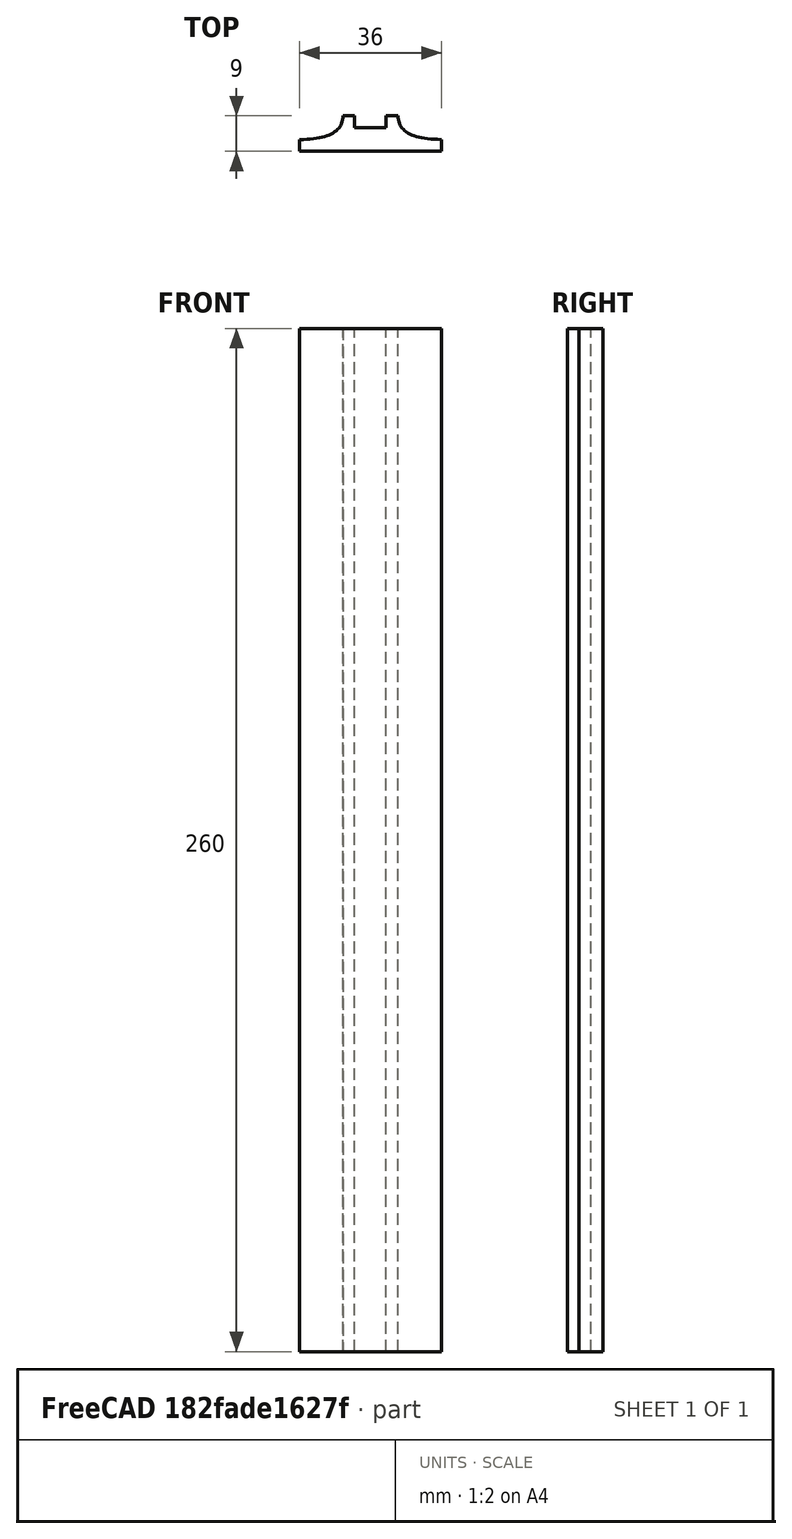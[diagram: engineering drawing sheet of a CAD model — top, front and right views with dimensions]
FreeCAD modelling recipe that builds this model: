
FCSTD DOCUMENT  (FreeCAD 0.19R0.19.2)
Label: laptopStand294.FCStd
License: All rights reserved
LicenseURL: http://en.wikipedia.org/wiki/All_rights_reserved
objects: Sketcher::SketchObject×10, Part::Extrusion×1
note: 11 computed .brp shape members not serialized (recipe doc carries the construction recipe); baked Part::Feature solids carry a one-line shape summary decoded from their .brp

FEATURE [Sketcher::SketchObject] Sketch001  label="legTop"
  FullyConstrained = false
  MapMode = 4
  Placement = pos=(0,0,0) rot=(0.57735,0.57735,0.57735;2.0944rad)
  sketch-geometry (59):
    g0: BSplineCurve PolesCount=3 KnotsCount=2 Degree=2 IsPeriodic=0
    g1: ArcOfCircle CenterX=73.1223 CenterY=-32.291 CenterZ=0 NormalX=0 NormalY=0 NormalZ=1 AngleXU=0 Radius=13 StartAngle=5.92268 EndAngle=9.06428
    g2: ArcOfCircle CenterX=66.7816 CenterY=-49.1439 CenterZ=0 NormalX=0 NormalY=0 NormalZ=1 AngleXU=0 Radius=13 StartAngle=2.78068 EndAngle=5.92131
    g3-g6: Circle x4 (B-spline internal-alignment scaffolding for g7; pole/knot coordinates omitted)
    g7: BSplineCurve PolesCount=4 KnotsCount=2 Degree=3 IsPeriodic=0
    g8: GeomPoint X=28.8094 Y=-19.0875 Z=0
    g9: GeomPoint X=47.0443 Y=-50.4712 Z=0
    g10: Circle CenterX=53.5586 CenterY=-23.2695 CenterZ=0 NormalX=0 NormalY=0 NormalZ=1 AngleXU=0 Radius=3.24518
    g11: LineSegment StartX=117.223 StartY=-19.0875 StartZ=0 EndX=117.223 EndY=-16.0875 EndZ=0
    g12: LineSegment StartX=117.223 StartY=-16.0875 StartZ=0 EndX=17.2232 EndY=-16.0875 EndZ=0
    g13: LineSegment StartX=17.2232 StartY=-16.0875 StartZ=0 EndX=17.2232 EndY=-19.0875 EndZ=0
    g14: LineSegment StartX=28.8094 StartY=-19.0875 StartZ=0 EndX=17.2232 EndY=-19.0875 EndZ=0
    g15: LineSegment StartX=85.2866 StartY=-36.8766 StartZ=0 EndX=78.9396 EndY=-53.7463 EndZ=0
    g16: LineSegment StartX=60.9579 StartY=-27.7053 StartZ=0 EndX=54.6191 EndY=-44.5532 EndZ=0
    g17: BSplineCurve PolesCount=3 KnotsCount=2 Degree=2 IsPeriodic=0
    g18: Circle CenterX=-199.665 CenterY=-138.314 CenterZ=0 NormalX=0 NormalY=0 NormalZ=1 AngleXU=0 Radius=1
    g19: GeomPoint X=-199.665 Y=-138.314 Z=0
    g20: LineSegment StartX=-199.665 StartY=-138.314 StartZ=0 EndX=-200.721 EndY=-141.122 EndZ=0
    g21: Circle CenterX=-17.0256 CenterY=-190.268 CenterZ=0 NormalX=0 NormalY=0 NormalZ=1 AngleXU=0 Radius=10.5072
    g22: Circle CenterX=-37.7758 CenterY=-187.672 CenterZ=0 NormalX=0 NormalY=0 NormalZ=1 AngleXU=0 Radius=5.64388
    g23: Circle CenterX=-51.4606 CenterY=-185.091 CenterZ=0 NormalX=0 NormalY=0 NormalZ=1 AngleXU=0 Radius=3.01653
    g24: Circle CenterX=-60.4835 CenterY=-182.688 CenterZ=0 NormalX=0 NormalY=0 NormalZ=1 AngleXU=0 Radius=2.12826
    g25: Circle CenterX=-3.29005 CenterY=-177.662 CenterZ=0 NormalX=0 NormalY=0 NormalZ=1 AngleXU=0 Radius=3.26661
    g26: ArcOfCircle CenterX=11.0205 CenterY=-198.019 CenterZ=0 NormalX=0 NormalY=0 NormalZ=1 AngleXU=0 Radius=13 StartAngle=2.78068 EndAngle=5.92131
    g27: LineSegment StartX=5.08312 StartY=-176.581 StartZ=0 EndX=-1.14188 EndY=-193.429 EndZ=0
    g28: LineSegment StartX=29.4118 StartY=-185.752 StartZ=0 EndX=23.1786 EndY=-202.622 EndZ=0
    g29: ArcOfCircle CenterX=17.2475 CenterY=-181.166 CenterZ=0 NormalX=0 NormalY=0 NormalZ=1 AngleXU=0 Radius=13 StartAngle=5.92268 EndAngle=9.06428
    g30: LineSegment StartX=38.8952 StartY=-231.233 StartZ=0 EndX=-200.721 EndY=-141.122 EndZ=0
    g31: LineSegment StartX=38.8952 StartY=-231.233 StartZ=0 EndX=39.9512 EndY=-228.425 EndZ=0
    g32: ArcOfCircle CenterX=46.9911 CenterY=-209.705 CenterZ=0 NormalX=0 NormalY=0 NormalZ=1 AngleXU=0 Radius=20 StartAngle=2.78766 EndAngle=4.35269
    g33: LineSegment StartX=23.7323 StartY=-126.969 StartZ=0 EndX=17.4091 EndY=-143.817 EndZ=0
    g34: ArcOfCircle CenterX=29.5716 CenterY=-148.408 CenterZ=0 NormalX=0 NormalY=0 NormalZ=1 AngleXU=0 Radius=13 StartAngle=2.78068 EndAngle=5.92131
    g35: ArcOfCircle CenterX=35.8967 CenterY=-131.555 CenterZ=0 NormalX=0 NormalY=0 NormalZ=1 AngleXU=0 Radius=13 StartAngle=5.92268 EndAngle=9.06428
    g36: ArcOfCircle CenterX=48.1805 CenterY=-98.7782 CenterZ=0 NormalX=0 NormalY=0 NormalZ=1 AngleXU=0 Radius=13 StartAngle=2.78068 EndAngle=5.92131
    g37: LineSegment StartX=42.354 StartY=-77.3391 StartZ=0 EndX=36.018 EndY=-94.1875 EndZ=0
    g38: ArcOfCircle CenterX=54.5183 CenterY=-81.9247 CenterZ=0 NormalX=0 NormalY=0 NormalZ=1 AngleXU=0 Radius=13 StartAngle=5.92268 EndAngle=9.06428
    g39: LineSegment StartX=66.6827 StartY=-86.5104 StartZ=0 EndX=60.3386 EndY=-103.381 EndZ=0
    g40: LineSegment StartX=48.061 StartY=-136.14 StartZ=0 EndX=41.7296 EndY=-153.01 EndZ=0
    g41: LineSegment StartX=28.2308 StartY=-202.773 StartZ=0 EndX=94.6579 EndY=-26.1359 EndZ=0
    g42: LineSegment StartX=47.0443 StartY=-50.4712 StartZ=0 EndX=8.65492 EndY=-152.553 EndZ=0
    g43: LineSegment StartX=23.1786 StartY=-202.622 StartZ=0 EndX=19.0195 EndY=-213.878 EndZ=0
    g44: ArcOfCircle CenterX=20.184 CenterY=-217.506 CenterZ=0 NormalX=0 NormalY=0 NormalZ=1 AngleXU=0 Radius=3.81084 StartAngle=1.88136 EndAngle=6.80465
    g45: LineSegment StartX=28.2308 StartY=-202.773 StartZ=0 EndX=23.4884 EndY=-215.608 EndZ=0
    g46: LineSegment StartX=41.2852 StartY=-117.017 StartZ=0 EndX=40.4092 EndY=-119.359 EndZ=0
    g47: LineSegment StartX=38.4753 StartY=-115.966 StartZ=0 EndX=41.2852 EndY=-117.017 EndZ=0
    g48: ArcOfCircle CenterX=36.3663 CenterY=-113.042 CenterZ=0 NormalX=0 NormalY=0 NormalZ=1 AngleXU=0 Radius=3.60555 StartAngle=0.230024 EndAngle=5.3372
    g49: LineSegment StartX=39.8769 StartY=-112.22 StartZ=0 EndX=42.6867 EndY=-113.271 EndZ=0
    g50: LineSegment StartX=42.6867 StartY=-113.271 StartZ=0 EndX=43.5628 EndY=-110.929 EndZ=0
    g51: LineSegment StartX=22.7134 StartY=-166.661 StartZ=0 EndX=21.8375 EndY=-169.003 EndZ=0
    g52: LineSegment StartX=19.9036 StartY=-165.61 StartZ=0 EndX=22.7134 EndY=-166.661 EndZ=0
    g53: ArcOfCircle CenterX=17.7945 CenterY=-162.686 CenterZ=0 NormalX=0 NormalY=0 NormalZ=1 AngleXU=0 Radius=3.60555 StartAngle=0.230024 EndAngle=5.3372
    g54: LineSegment StartX=21.3051 StartY=-161.864 StartZ=0 EndX=24.1149 EndY=-162.915 EndZ=0
    g55: LineSegment StartX=24.1149 StartY=-162.915 StartZ=0 EndX=24.991 EndY=-160.573 EndZ=0
    g56: LineSegment StartX=41.085 StartY=-66.3176 StartZ=0 EndX=46.0385 EndY=-62.5254 EndZ=0
    g57: LineSegment StartX=48.9563 StartY=-66.3367 StartZ=0 EndX=44.7488 EndY=-73.3482 EndZ=0
    g58: ArcOfCircle CenterX=49.8795 CenterY=-62.6074 CenterZ=0 NormalX=0 NormalY=0 NormalZ=1 AngleXU=0 Radius=3.84187 StartAngle=4.46973 EndAngle=9.40343
  constraints (101):
    c: Block(g0)
    c: Block(g1)
    c: Block(g2)
    c: Weight(g3) = 1
    c: Equal(g3,g4)
    c: Equal(g3,g5)
    c: Equal(g3,g6)
    c: InternalAlignment(g3-g6 -> g7) x4
    c: InternalAlignment(g8,g7)
    c: InternalAlignment(g9,g7)
    c: Block(g10)
    c: Block(g7)
    c: Coincident(g11,g0)
    c: Vertical(g11)
    c: Coincident(g12,g11)
    c: Horizontal(g12)
    c: Coincident(g13,g12)
    c: Vertical(g13)
    c: Block(g12)
    c: Coincident(g14,g7)
    c: Coincident(g14,g13)
    c: Horizontal(g14)
    c: Coincident(g15,g1)
    c: Coincident(g15,g2)
    c: Coincident(g16,g1)
    c: Coincident(g16,g2)
    c: Distance(g12) = 100
    c: Block(g26)
    c: Block(g29)
    c: InternalAlignment(g18,g17)
    c: InternalAlignment(g19,g17)
    c: Block(g17)
    c: Block(g21)
    c: Block(g25)
    c: Block(g22)
    c: Block(g23)
    c: Block(g24)
    c: Block(g32)
    c: Coincident(g31,g30)
    c: Coincident(g31,g32)
    c: Block(g31)
    c: Coincident(g20,g17)
    c: Coincident(g20,g30)
    c: Block(g30)
    c: Coincident(g27,g29)
    c: Coincident(g27,g26)
    c: Coincident(g28,g29)
    c: Coincident(g28,g26)
    c: Block(g34)
    c: Block(g35)
    c: Coincident(g33,g35)
    c: Coincident(g33,g34)
    c: Block(g36)
    c: Block(g38)
    c: Coincident(g37,g38)
    c: Coincident(g37,g36)
    c: Coincident(g39,g38)
    c: Coincident(g39,g36)
    c: Coincident(g40,g35)
    c: Coincident(g40,g34)
    c: Coincident(g41,g32)
    c: Coincident(g41,g0)
    c: Coincident(g42,g7)
    c: Coincident(g42,g17)
    c: Coincident(g43,g26)
    c: Parallel(g28,g43)
    c: Distance(g43) = 12
    c: Block(g28)
    c: Coincident(g44,g43)
    c: Block(g44)
    c: Coincident(g45,g32)
    c: Coincident(g45,g44)
    c: Tangent(g45,g32)
    c: Parallel(g45,g43)
    c: Block(g45)
    c: Block(g48)
    c: Coincident(g49,g48)
    c: Coincident(g47,g48)
    c: Parallel(g49,g47)
    c: Coincident(g46,g47)
    c: Coincident(g50,g49)
    c: Block(g50)
    c: Block(g46)
    c: Block(g47)
    c: Block(g49)
    c: Block(g53)
    c: Coincident(g54,g53)
    c: Coincident(g52,g53)
    c: Parallel(g54,g52)
    c: Coincident(g51,g52)
    c: Coincident(g55,g54)
    c: Block(g55)
    c: Block(g51)
    c: Block(g52)
    c: Block(g54)
    c: PointOnObject(g56,g42)
    c: Block(g56)
    c: PointOnObject(g57,g38)
    c: Coincident(g58,g56)
    c: Coincident(g58,g57)
    c: Block(g58)
FEATURE [Sketcher::SketchObject] Sketch002
  FullyConstrained = true
  sketch-geometry (20):
    g0: LineSegment StartX=-2.77179 StartY=-200.304 StartZ=0 EndX=5.22821 EndY=-200.304 EndZ=0
    g1: LineSegment StartX=5.22821 StartY=-200.304 StartZ=0 EndX=5.22821 EndY=-197.304 EndZ=0
    g2: LineSegment StartX=-2.77179 StartY=-200.304 StartZ=0 EndX=-2.77179 EndY=-197.304 EndZ=0
    g3: LineSegment StartX=5.22821 StartY=-197.304 StartZ=0 EndX=8.22821 EndY=-197.304 EndZ=0
    g4: LineSegment StartX=-2.77179 StartY=-197.304 StartZ=0 EndX=-5.77179 EndY=-197.304 EndZ=0
    g5: LineSegment StartX=19.2282 StartY=-203.304 StartZ=0 EndX=19.2282 EndY=-206.304 EndZ=0
    g6: LineSegment StartX=-16.7718 StartY=-203.304 StartZ=0 EndX=-16.7718 EndY=-206.304 EndZ=0
    g7: LineSegment StartX=-16.7718 StartY=-206.304 StartZ=0 EndX=19.2282 EndY=-206.304 EndZ=0
    g8: Circle CenterX=-16.7718 CenterY=-203.304 CenterZ=0 NormalX=0 NormalY=0 NormalZ=1 AngleXU=0 Radius=1
    g9: Circle CenterX=-5.77179 CenterY=-203.304 CenterZ=0 NormalX=0 NormalY=0 NormalZ=1 AngleXU=0 Radius=1
    g10: Circle CenterX=-5.77179 CenterY=-197.304 CenterZ=0 NormalX=0 NormalY=0 NormalZ=1 AngleXU=0 Radius=1
    g11: BSplineCurve PolesCount=3 KnotsCount=2 Degree=2 IsPeriodic=0
    g12: GeomPoint X=-16.7718 Y=-203.304 Z=0
    g13: GeomPoint X=-5.77179 Y=-197.304 Z=0
    g14: Circle CenterX=19.2282 CenterY=-203.304 CenterZ=0 NormalX=0 NormalY=0 NormalZ=1 AngleXU=0 Radius=1
    g15: Circle CenterX=8.22821 CenterY=-203.304 CenterZ=0 NormalX=0 NormalY=0 NormalZ=1 AngleXU=0 Radius=1
    g16: Circle CenterX=8.22821 CenterY=-197.304 CenterZ=0 NormalX=0 NormalY=0 NormalZ=1 AngleXU=0 Radius=1
    g17: BSplineCurve PolesCount=3 KnotsCount=2 Degree=2 IsPeriodic=0
    g18: GeomPoint X=19.2282 Y=-203.304 Z=0
    g19: GeomPoint X=8.22821 Y=-197.304 Z=0
  constraints (41):
    c: Horizontal(g0)
    c: Distance(g0) = 8
    c: Coincident(g1,g0)
    c: Vertical(g1)
    c: Distance(g1) = 3
    c: Coincident(g2,g0)
    c: Vertical(g2)
    c: Distance(g2) = 3
    c: Coincident(g3,g1)
    c: Horizontal(g3)
    c: Distance(g3) = 3
    c: Coincident(g4,g2)
    c: Horizontal(g4)
    c: Distance(g4) = 3
    c: Vertical(g5)
    c: Vertical(g6)
    c: Coincident(g7,g6)
    c: Coincident(g7,g5)
    c: Weight(g8) = 1
    c: Equal(g8,g9)
    c: Equal(g8,g10)
    c: Coincident(g11,g4)
    c: InternalAlignment(g8,g11)
    c: InternalAlignment(g9,g11)
    c: InternalAlignment(g10,g11)
    c: InternalAlignment(g12,g11)
    c: InternalAlignment(g13,g11)
    c: Coincident(g17,g5)
    c: Weight(g14) = 1
    c: Equal(g14,g15)
    c: Equal(g14,g16)
    c: Coincident(g17,g3)
    c: InternalAlignment(g14,g17)
    c: InternalAlignment(g15,g17)
    c: InternalAlignment(g16,g17)
    c: InternalAlignment(g18,g17)
    c: InternalAlignment(g19,g17)
    c: Block(g7)
    c: Block(g17)
    c: Block(g11)
    c: Block(g6)
FEATURE [Part::Extrusion] Extrude003
  Base = -> Sketch002
  Dir = (0,0,1)
  DirMode = 2
  FaceMakerClass = Part::FaceMakerBullseye
  LengthFwd = 260
  LengthRev = 0
  Solid = true
  Symmetric = false
FEATURE [Sketcher::SketchObject] Sketch003  label="original"
  FullyConstrained = false
  sketch-geometry (469):
    g0: LineSegment StartX=-42.9272 StartY=136.221 StartZ=0 EndX=-42.9272 EndY=-103.779 EndZ=0
    g1: LineSegment StartX=407.073 StartY=136.221 StartZ=0 EndX=407.073 EndY=-103.779 EndZ=0
    g2: ArcOfCircle CenterX=-26.9272 CenterY=-83.7794 CenterZ=0 NormalX=0 NormalY=0 NormalZ=1 AngleXU=0 Radius=8 StartAngle=3.14159 EndAngle=6.28319
    g3: ArcOfCircle CenterX=391.073 CenterY=-83.7794 CenterZ=0 NormalX=0 NormalY=0 NormalZ=1 AngleXU=0 Radius=8 StartAngle=3.14159 EndAngle=6.28319
    g4: Circle CenterX=175.022 CenterY=27.0628 CenterZ=0 NormalX=0 NormalY=0 NormalZ=1 AngleXU=0 Radius=1
    g5: Circle CenterX=179.022 CenterY=24.8665 CenterZ=0 NormalX=0 NormalY=0 NormalZ=1 AngleXU=0 Radius=1
    g6: Circle CenterX=179.022 CenterY=27.0628 CenterZ=0 NormalX=0 NormalY=0 NormalZ=1 AngleXU=0 Radius=1
    g7: BSplineCurve PolesCount=3 KnotsCount=2 Degree=2 IsPeriodic=0
    g8: GeomPoint X=175.022 Y=27.0628 Z=0
    g9: GeomPoint X=179.022 Y=27.0628 Z=0
    g10: Circle CenterX=189.124 CenterY=27.0628 CenterZ=0 NormalX=0 NormalY=0 NormalZ=1 AngleXU=0 Radius=1
    g11: Circle CenterX=185.124 CenterY=24.8665 CenterZ=0 NormalX=0 NormalY=0 NormalZ=1 AngleXU=0 Radius=1
    g12: Circle CenterX=185.124 CenterY=27.0628 CenterZ=0 NormalX=0 NormalY=0 NormalZ=1 AngleXU=0 Radius=1
    g13: BSplineCurve PolesCount=3 KnotsCount=2 Degree=2 IsPeriodic=0
    g14: GeomPoint X=189.124 Y=27.0628 Z=0
    g15: GeomPoint X=185.124 Y=27.0628 Z=0
    g16: Circle CenterX=175.022 CenterY=5.37834 CenterZ=0 NormalX=0 NormalY=0 NormalZ=1 AngleXU=0 Radius=1
    g17: Circle CenterX=179.022 CenterY=7.57463 CenterZ=0 NormalX=0 NormalY=0 NormalZ=1 AngleXU=0 Radius=1
    g18: Circle CenterX=179.022 CenterY=5.34704 CenterZ=0 NormalX=0 NormalY=0 NormalZ=1 AngleXU=0 Radius=1
    g19: BSplineCurve PolesCount=3 KnotsCount=2 Degree=2 IsPeriodic=0
    g20: GeomPoint X=175.022 Y=5.37834 Z=0
    g21: GeomPoint X=179.022 Y=5.34704 Z=0
    g22: Circle CenterX=189.124 CenterY=5.37834 CenterZ=0 NormalX=0 NormalY=0 NormalZ=1 AngleXU=0 Radius=1
    g23: Circle CenterX=185.124 CenterY=7.57463 CenterZ=0 NormalX=0 NormalY=0 NormalZ=1 AngleXU=0 Radius=1
    g24: Circle CenterX=185.124 CenterY=5.34704 CenterZ=0 NormalX=0 NormalY=0 NormalZ=1 AngleXU=0 Radius=1
    g25: BSplineCurve PolesCount=3 KnotsCount=2 Degree=2 IsPeriodic=0
    g26: GeomPoint X=189.124 Y=5.37834 Z=0
    g27: GeomPoint X=185.124 Y=5.34704 Z=0
    g28: Circle CenterX=165.871 CenterY=18.1458 CenterZ=0 NormalX=0 NormalY=0 NormalZ=1 AngleXU=0 Radius=1
    g29: Circle CenterX=169.377 CenterY=16.2206 CenterZ=0 NormalX=0 NormalY=0 NormalZ=1 AngleXU=0 Radius=1
    g30: Circle CenterX=165.871 CenterY=14.2956 CenterZ=0 NormalX=0 NormalY=0 NormalZ=1 AngleXU=0 Radius=1
    g31: BSplineCurve PolesCount=3 KnotsCount=2 Degree=2 IsPeriodic=0
    g32: GeomPoint X=165.871 Y=18.1458 Z=0
    g33: GeomPoint X=165.871 Y=14.2956 Z=0
    g34: Circle CenterX=198.275 CenterY=18.1318 CenterZ=0 NormalX=0 NormalY=0 NormalZ=1 AngleXU=0 Radius=1
    g35: Circle CenterX=194.768 CenterY=16.2206 CenterZ=0 NormalX=0 NormalY=0 NormalZ=1 AngleXU=0 Radius=1
    g36: Circle CenterX=198.264 CenterY=14.2963 CenterZ=0 NormalX=0 NormalY=0 NormalZ=1 AngleXU=0 Radius=1
    g37: BSplineCurve PolesCount=3 KnotsCount=2 Degree=2 IsPeriodic=0
    g38: GeomPoint X=198.275 Y=18.1318 Z=0
    g39: GeomPoint X=198.264 Y=14.2963 Z=0
    g40: LineSegment StartX=407.073 StartY=-103.779 StartZ=0 EndX=-42.9272 EndY=-103.779 EndZ=0
    g41: Circle CenterX=125.607 CenterY=54.1951 CenterZ=0 NormalX=0 NormalY=0 NormalZ=1 AngleXU=0 Radius=1
    g42: Circle CenterX=139.632 CenterY=46.4944 CenterZ=0 NormalX=0 NormalY=0 NormalZ=1 AngleXU=0 Radius=1
    g43: Circle CenterX=127.326 CenterY=56.7187 CenterZ=0 NormalX=0 NormalY=0 NormalZ=1 AngleXU=0 Radius=1
    g44: BSplineCurve PolesCount=3 KnotsCount=2 Degree=2 IsPeriodic=0
    g45: GeomPoint X=125.607 Y=54.1951 Z=0
    g46: GeomPoint X=127.326 Y=56.7187 Z=0
    g47: Circle CenterX=236.824 CenterY=56.7187 CenterZ=0 NormalX=0 NormalY=0 NormalZ=1 AngleXU=0 Radius=1
    g48: Circle CenterX=224.513 CenterY=46.4944 CenterZ=0 NormalX=0 NormalY=0 NormalZ=1 AngleXU=0 Radius=1
    g49: Circle CenterX=238.538 CenterY=54.1951 CenterZ=0 NormalX=0 NormalY=0 NormalZ=1 AngleXU=0 Radius=1
    g50: BSplineCurve PolesCount=3 KnotsCount=2 Degree=2 IsPeriodic=0
    g51: GeomPoint X=236.824 Y=56.7187 Z=0
    g52: GeomPoint X=238.538 Y=54.1951 Z=0
    g53: Circle CenterX=238.538 CenterY=-21.7516 CenterZ=0 NormalX=0 NormalY=0 NormalZ=1 AngleXU=0 Radius=1
    g54: Circle CenterX=224.513 CenterY=-14.0532 CenterZ=0 NormalX=0 NormalY=0 NormalZ=1 AngleXU=0 Radius=1
    g55: Circle CenterX=236.584 CenterY=-24.2775 CenterZ=0 NormalX=0 NormalY=0 NormalZ=1 AngleXU=0 Radius=1
    g56: BSplineCurve PolesCount=3 KnotsCount=2 Degree=2 IsPeriodic=0
    g57: GeomPoint X=238.538 Y=-21.7516 Z=0
    g58: GeomPoint X=236.584 Y=-24.2775 Z=0
    g59: Circle CenterX=125.607 CenterY=-21.7539 CenterZ=0 NormalX=0 NormalY=0 NormalZ=1 AngleXU=0 Radius=1
    g60: Circle CenterX=139.632 CenterY=-14.0532 CenterZ=0 NormalX=0 NormalY=0 NormalZ=1 AngleXU=0 Radius=1
    g61: Circle CenterX=127.325 CenterY=-24.2775 CenterZ=0 NormalX=0 NormalY=0 NormalZ=1 AngleXU=0 Radius=1
    g62: BSplineCurve PolesCount=3 KnotsCount=2 Degree=2 IsPeriodic=0
    g63: GeomPoint X=125.607 Y=-21.7539 Z=0
    g64: GeomPoint X=127.325 Y=-24.2775 Z=0
    g65: Circle CenterX=302.996 CenterY=111.695 CenterZ=0 NormalX=0 NormalY=0 NormalZ=1 AngleXU=0 Radius=1
    g66: Circle CenterX=306.073 CenterY=114.251 CenterZ=0 NormalX=0 NormalY=0 NormalZ=1 AngleXU=0 Radius=1
    g67: Circle CenterX=306.073 CenterY=110.251 CenterZ=0 NormalX=0 NormalY=0 NormalZ=1 AngleXU=0 Radius=1
    g68: BSplineCurve PolesCount=3 KnotsCount=2 Degree=2 IsPeriodic=0
    g69: GeomPoint X=302.996 Y=111.695 Z=0
    g70: GeomPoint X=306.073 Y=110.251 Z=0
    g71: Circle CenterX=306.073 CenterY=95.2763 CenterZ=0 NormalX=0 NormalY=0 NormalZ=1 AngleXU=0 Radius=1
    g72: Circle CenterX=306.073 CenterY=91.2763 CenterZ=0 NormalX=0 NormalY=0 NormalZ=1 AngleXU=0 Radius=1
    g73: Circle CenterX=302.567 CenterY=89.3511 CenterZ=0 NormalX=0 NormalY=0 NormalZ=1 AngleXU=0 Radius=1
    g74: BSplineCurve PolesCount=3 KnotsCount=2 Degree=2 IsPeriodic=0
    g75: GeomPoint X=306.073 Y=95.2763 Z=0
    g76: GeomPoint X=302.567 Y=89.3511 Z=0
    g77: LineSegment StartX=306.073 StartY=110.251 StartZ=0 EndX=306.073 EndY=95.2763 EndZ=0
    g78: LineSegment StartX=302.996 StartY=111.695 StartZ=0 EndX=236.824 EndY=56.7187 EndZ=0
    g79: LineSegment StartX=238.538 StartY=54.1951 StartZ=0 EndX=302.567 EndY=89.3511 EndZ=0
    g80: Circle CenterX=61.1496 CenterY=111.695 CenterZ=0 NormalX=0 NormalY=0 NormalZ=1 AngleXU=0 Radius=1
    g81: Circle CenterX=58.0728 CenterY=114.251 CenterZ=0 NormalX=0 NormalY=0 NormalZ=1 AngleXU=0 Radius=1
    g82: Circle CenterX=58.0728 CenterY=110.251 CenterZ=0 NormalX=0 NormalY=0 NormalZ=1 AngleXU=0 Radius=1
    g83: BSplineCurve PolesCount=3 KnotsCount=2 Degree=2 IsPeriodic=0
    g84: GeomPoint X=61.1496 Y=111.695 Z=0
    g85: GeomPoint X=58.0728 Y=110.251 Z=0
    g86: Circle CenterX=61.5791 CenterY=89.3511 CenterZ=0 NormalX=0 NormalY=0 NormalZ=1 AngleXU=0 Radius=1
    g87: Circle CenterX=58.0728 CenterY=91.2763 CenterZ=0 NormalX=0 NormalY=0 NormalZ=1 AngleXU=0 Radius=1
    g88: Circle CenterX=58.0728 CenterY=95.2763 CenterZ=0 NormalX=0 NormalY=0 NormalZ=1 AngleXU=0 Radius=1
    g89: BSplineCurve PolesCount=3 KnotsCount=2 Degree=2 IsPeriodic=0
    g90: GeomPoint X=61.5791 Y=89.3511 Z=0
    g91: GeomPoint X=58.0728 Y=95.2763 Z=0
    g92: LineSegment StartX=58.0728 StartY=110.251 StartZ=0 EndX=58.0728 EndY=95.2763 EndZ=0
    g93: LineSegment StartX=61.1496 StartY=111.695 StartZ=0 EndX=127.326 EndY=56.7187 EndZ=0
    g94: LineSegment StartX=125.607 StartY=54.1951 StartZ=0 EndX=61.5791 EndY=89.3511 EndZ=0
    g95: Circle CenterX=61.5791 CenterY=-56.9099 CenterZ=0 NormalX=0 NormalY=0 NormalZ=1 AngleXU=0 Radius=1
    g96: Circle CenterX=58.0728 CenterY=-58.8351 CenterZ=0 NormalX=0 NormalY=0 NormalZ=1 AngleXU=0 Radius=1
    g97: Circle CenterX=58.0728 CenterY=-62.8351 CenterZ=0 NormalX=0 NormalY=0 NormalZ=1 AngleXU=0 Radius=1
    g98: BSplineCurve PolesCount=3 KnotsCount=2 Degree=2 IsPeriodic=0
    g99: GeomPoint X=61.5791 Y=-56.9099 Z=0
    g100: GeomPoint X=58.0728 Y=-62.8351 Z=0
    g101: Circle CenterX=58.0728 CenterY=-77.8102 CenterZ=0 NormalX=0 NormalY=0 NormalZ=1 AngleXU=0 Radius=1
    g102: Circle CenterX=58.0728 CenterY=-81.8102 CenterZ=0 NormalX=0 NormalY=0 NormalZ=1 AngleXU=0 Radius=1
    g103: Circle CenterX=61.1496 CenterY=-79.2541 CenterZ=0 NormalX=0 NormalY=0 NormalZ=1 AngleXU=0 Radius=1
    g104: BSplineCurve PolesCount=3 KnotsCount=2 Degree=2 IsPeriodic=0
    g105: GeomPoint X=58.0728 Y=-77.8102 Z=0
    g106: GeomPoint X=61.1496 Y=-79.2541 Z=0
    g107: LineSegment StartX=58.0728 StartY=-62.8351 StartZ=0 EndX=58.0728 EndY=-77.8102 EndZ=0
    g108: LineSegment StartX=61.1496 StartY=-79.2541 StartZ=0 EndX=127.325 EndY=-24.2775 EndZ=0
    g109: LineSegment StartX=125.607 StartY=-21.7539 StartZ=0 EndX=61.5791 EndY=-56.9099 EndZ=0
    g110: Circle CenterX=302.567 CenterY=-56.9099 CenterZ=0 NormalX=0 NormalY=0 NormalZ=1 AngleXU=0 Radius=1
    g111: Circle CenterX=306.073 CenterY=-58.8351 CenterZ=0 NormalX=0 NormalY=0 NormalZ=1 AngleXU=0 Radius=1
    g112: Circle CenterX=306.073 CenterY=-62.8351 CenterZ=0 NormalX=0 NormalY=0 NormalZ=1 AngleXU=0 Radius=1
    g113: BSplineCurve PolesCount=3 KnotsCount=2 Degree=2 IsPeriodic=0
    g114: GeomPoint X=302.567 Y=-56.9099 Z=0
    g115: GeomPoint X=306.073 Y=-62.8351 Z=0
    g116: Circle CenterX=302.996 CenterY=-79.2541 CenterZ=0 NormalX=0 NormalY=0 NormalZ=1 AngleXU=0 Radius=1
    g117: Circle CenterX=306.073 CenterY=-81.8102 CenterZ=0 NormalX=0 NormalY=0 NormalZ=1 AngleXU=0 Radius=1
    g118: Circle CenterX=306.073 CenterY=-77.8102 CenterZ=0 NormalX=0 NormalY=0 NormalZ=1 AngleXU=0 Radius=1
    g119: BSplineCurve PolesCount=3 KnotsCount=2 Degree=2 IsPeriodic=0
    g120: GeomPoint X=302.996 Y=-79.2541 Z=0
    g121: GeomPoint X=306.073 Y=-77.8102 Z=0
    g122: LineSegment StartX=306.073 StartY=-62.8351 StartZ=0 EndX=306.073 EndY=-77.8102 EndZ=0
    g123: LineSegment StartX=302.996 StartY=-79.2541 StartZ=0 EndX=236.584 EndY=-24.2775 EndZ=0
    g124: LineSegment StartX=238.538 StartY=-21.7516 StartZ=0 EndX=302.567 EndY=-56.9099 EndZ=0
    g125: Circle CenterX=61.6457 CenterY=-88.8112 CenterZ=0 NormalX=0 NormalY=0 NormalZ=1 AngleXU=0 Radius=1
    g126: Circle CenterX=58.0728 CenterY=-91.7794 CenterZ=0 NormalX=0 NormalY=0 NormalZ=1 AngleXU=0 Radius=1
    g127: Circle CenterX=63.9135 CenterY=-91.7791 CenterZ=0 NormalX=0 NormalY=0 NormalZ=1 AngleXU=0 Radius=1
    g128: BSplineCurve PolesCount=3 KnotsCount=2 Degree=2 IsPeriodic=0
    g129: GeomPoint X=61.6457 Y=-88.8112 Z=0
    g130: GeomPoint X=63.9135 Y=-91.7791 Z=0
    g131: Circle CenterX=179.022 CenterY=-85.8163 CenterZ=0 NormalX=0 NormalY=0 NormalZ=1 AngleXU=0 Radius=1
    g132: Circle CenterX=179.022 CenterY=-91.7794 CenterZ=0 NormalX=0 NormalY=0 NormalZ=1 AngleXU=0 Radius=1
    g133: Circle CenterX=171.895 CenterY=-91.7791 CenterZ=0 NormalX=0 NormalY=0 NormalZ=1 AngleXU=0 Radius=1
    g134: BSplineCurve PolesCount=3 KnotsCount=2 Degree=2 IsPeriodic=0
    g135: GeomPoint X=179.022 Y=-85.8163 Z=0
    g136: GeomPoint X=171.895 Y=-91.7791 Z=0
    g137: Circle CenterX=185.124 CenterY=-86.2028 CenterZ=0 NormalX=0 NormalY=0 NormalZ=1 AngleXU=0 Radius=1
    g138: Circle CenterX=185.124 CenterY=-91.7794 CenterZ=0 NormalX=0 NormalY=0 NormalZ=1 AngleXU=0 Radius=1
    g139: Circle CenterX=191.747 CenterY=-91.7794 CenterZ=0 NormalX=0 NormalY=0 NormalZ=1 AngleXU=0 Radius=1
    g140: BSplineCurve PolesCount=3 KnotsCount=2 Degree=2 IsPeriodic=0
    g141: GeomPoint X=185.124 Y=-86.2028 Z=0
    g142: GeomPoint X=191.747 Y=-91.7794 Z=0
    g143: Circle CenterX=299.888 CenterY=-86.6413 CenterZ=0 NormalX=0 NormalY=0 NormalZ=1 AngleXU=0 Radius=1
    g144: Circle CenterX=306.073 CenterY=-91.7794 CenterZ=0 NormalX=0 NormalY=0 NormalZ=1 AngleXU=0 Radius=1
    g145: Circle CenterX=298.776 CenterY=-91.7794 CenterZ=0 NormalX=0 NormalY=0 NormalZ=1 AngleXU=0 Radius=1
    g146: BSplineCurve PolesCount=3 KnotsCount=2 Degree=2 IsPeriodic=0
    g147: GeomPoint X=299.888 Y=-86.6413 Z=0
    g148: GeomPoint X=298.776 Y=-91.7794 Z=0
    g149: LineSegment StartX=189.124 StartY=5.37834 StartZ=0 EndX=299.888 EndY=-86.6413 EndZ=0
    g150: LineSegment StartX=298.776 StartY=-91.7794 StartZ=0 EndX=191.747 EndY=-91.7794 EndZ=0
    g151: LineSegment StartX=185.124 StartY=-86.2028 StartZ=0 EndX=185.124 EndY=5.34704 EndZ=0
    g152: LineSegment StartX=179.022 StartY=5.34704 StartZ=0 EndX=179.022 EndY=-85.8163 EndZ=0
    g153: LineSegment StartX=171.895 StartY=-91.7791 StartZ=0 EndX=63.9135 EndY=-91.7791 EndZ=0
    g154: LineSegment StartX=61.6457 StartY=-88.8112 StartZ=0 EndX=175.022 EndY=5.37834 EndZ=0
    g155: Circle CenterX=302.073 CenterY=124.221 CenterZ=0 NormalX=0 NormalY=0 NormalZ=1 AngleXU=0 Radius=1
    g156: Circle CenterX=306.073 CenterY=124.221 CenterZ=0 NormalX=0 NormalY=0 NormalZ=1 AngleXU=0 Radius=1
    g157: Circle CenterX=302.996 CenterY=121.665 CenterZ=0 NormalX=0 NormalY=0 NormalZ=1 AngleXU=0 Radius=1
    g158: BSplineCurve PolesCount=3 KnotsCount=2 Degree=2 IsPeriodic=0
    g159: GeomPoint X=302.073 Y=124.221 Z=0
    g160: GeomPoint X=302.996 Y=121.665 Z=0
    g161: Circle CenterX=189.124 CenterY=124.221 CenterZ=0 NormalX=0 NormalY=0 NormalZ=1 AngleXU=0 Radius=1
    g162: Circle CenterX=185.124 CenterY=124.221 CenterZ=0 NormalX=0 NormalY=0 NormalZ=1 AngleXU=0 Radius=1
    g163: Circle CenterX=185.124 CenterY=120.221 CenterZ=0 NormalX=0 NormalY=0 NormalZ=1 AngleXU=0 Radius=1
    g164: BSplineCurve PolesCount=3 KnotsCount=2 Degree=2 IsPeriodic=0
    g165: GeomPoint X=189.124 Y=124.221 Z=0
    g166: GeomPoint X=185.124 Y=120.221 Z=0
    g167: Circle CenterX=175.022 CenterY=124.221 CenterZ=0 NormalX=0 NormalY=0 NormalZ=1 AngleXU=0 Radius=1
    g168: Circle CenterX=179.022 CenterY=124.221 CenterZ=0 NormalX=0 NormalY=0 NormalZ=1 AngleXU=0 Radius=1
    g169: Circle CenterX=179.022 CenterY=120.221 CenterZ=0 NormalX=0 NormalY=0 NormalZ=1 AngleXU=0 Radius=1
    g170: BSplineCurve PolesCount=3 KnotsCount=2 Degree=2 IsPeriodic=0
    g171: GeomPoint X=175.022 Y=124.221 Z=0
    g172: GeomPoint X=179.022 Y=120.221 Z=0
    g173: Circle CenterX=62.0728 CenterY=124.221 CenterZ=0 NormalX=0 NormalY=0 NormalZ=1 AngleXU=0 Radius=1
    g174: Circle CenterX=58.0728 CenterY=124.221 CenterZ=0 NormalX=0 NormalY=0 NormalZ=1 AngleXU=0 Radius=1
    g175: Circle CenterX=61.1496 CenterY=121.665 CenterZ=0 NormalX=0 NormalY=0 NormalZ=1 AngleXU=0 Radius=1
    g176: BSplineCurve PolesCount=3 KnotsCount=2 Degree=2 IsPeriodic=0
    g177: GeomPoint X=62.0728 Y=124.221 Z=0
    g178: GeomPoint X=61.1496 Y=121.665 Z=0
    g179: LineSegment StartX=179.022 StartY=120.221 StartZ=0 EndX=179.022 EndY=27.0628 EndZ=0
    g180: LineSegment StartX=185.124 StartY=27.0628 StartZ=0 EndX=185.124 EndY=120.221 EndZ=0
    g181: LineSegment StartX=302.996 StartY=121.665 StartZ=0 EndX=189.124 EndY=27.0628 EndZ=0
    g182: LineSegment StartX=175.022 StartY=27.0628 StartZ=0 EndX=61.1496 EndY=121.665 EndZ=0
    g183: Circle CenterX=61.5791 CenterY=75.4095 CenterZ=0 NormalX=0 NormalY=0 NormalZ=1 AngleXU=0 Radius=1
    g184: Circle CenterX=58.0728 CenterY=77.3346 CenterZ=0 NormalX=0 NormalY=0 NormalZ=1 AngleXU=0 Radius=1
    g185: Circle CenterX=58.0728 CenterY=73.3346 CenterZ=0 NormalX=0 NormalY=0 NormalZ=1 AngleXU=0 Radius=1
    g186: BSplineCurve PolesCount=3 KnotsCount=2 Degree=2 IsPeriodic=0
    g187: GeomPoint X=61.5791 Y=75.4095 Z=0
    g188: GeomPoint X=58.0728 Y=73.3346 Z=0
    g189: Circle CenterX=58.0728 CenterY=-40.8935 CenterZ=0 NormalX=0 NormalY=0 NormalZ=1 AngleXU=0 Radius=1
    g190: Circle CenterX=58.0728 CenterY=-44.8935 CenterZ=0 NormalX=0 NormalY=0 NormalZ=1 AngleXU=0 Radius=1
    g191: Circle CenterX=61.5791 CenterY=-42.9683 CenterZ=0 NormalX=0 NormalY=0 NormalZ=1 AngleXU=0 Radius=1
    g192: BSplineCurve PolesCount=3 KnotsCount=2 Degree=2 IsPeriodic=0
    g193: GeomPoint X=58.0728 Y=-40.8935 Z=0
    g194: GeomPoint X=61.5791 Y=-42.9683 Z=0
    g195: LineSegment StartX=61.5791 StartY=-42.9683 StartZ=0 EndX=165.871 EndY=14.2956 EndZ=0
    g196: LineSegment StartX=165.871 StartY=18.1458 StartZ=0 EndX=61.5791 EndY=75.4095 EndZ=0
    g197: LineSegment StartX=58.0728 StartY=73.3346 StartZ=0 EndX=58.0728 EndY=-40.8935 EndZ=0
    g198: Circle CenterX=302.567 CenterY=-42.9683 CenterZ=0 NormalX=0 NormalY=0 NormalZ=1 AngleXU=0 Radius=1
    g199: Circle CenterX=306.073 CenterY=-44.8935 CenterZ=0 NormalX=0 NormalY=0 NormalZ=1 AngleXU=0 Radius=1
    g200: Circle CenterX=306.073 CenterY=-40.8935 CenterZ=0 NormalX=0 NormalY=0 NormalZ=1 AngleXU=0 Radius=1
    g201: BSplineCurve PolesCount=3 KnotsCount=2 Degree=2 IsPeriodic=0
    g202: GeomPoint X=302.567 Y=-42.9683 Z=0
    g203: GeomPoint X=306.073 Y=-40.8935 Z=0
    g204: Circle CenterX=306.073 CenterY=73.3346 CenterZ=0 NormalX=0 NormalY=0 NormalZ=1 AngleXU=0 Radius=1
    g205: Circle CenterX=306.073 CenterY=77.3346 CenterZ=0 NormalX=0 NormalY=0 NormalZ=1 AngleXU=0 Radius=1
    g206: Circle CenterX=302.535 CenterY=75.4095 CenterZ=0 NormalX=0 NormalY=0 NormalZ=1 AngleXU=0 Radius=1
    g207: BSplineCurve PolesCount=3 KnotsCount=2 Degree=2 IsPeriodic=0
    g208: GeomPoint X=306.073 Y=73.3346 Z=0
    g209: GeomPoint X=302.535 Y=75.4095 Z=0
    g210: LineSegment StartX=302.567 StartY=-42.9683 StartZ=0 EndX=198.264 EndY=14.2963 EndZ=0
    g211: LineSegment StartX=198.275 StartY=18.1318 StartZ=0 EndX=302.535 EndY=75.4095 EndZ=0
    g212: LineSegment StartX=306.073 StartY=73.3346 StartZ=0 EndX=306.073 EndY=-40.8935 EndZ=0
    g213: LineSegment StartX=322.073 StartY=105.865 StartZ=0 EndX=328.643 EndY=105.865 EndZ=0
    g214: LineSegment StartX=318.073 StartY=120.221 StartZ=0 EndX=318.073 EndY=109.865 EndZ=0
    g215: LineSegment StartX=336.157 StartY=107.779 StartZ=0 EndX=362.567 EndY=122.294 EndZ=0
    g216: Circle CenterX=362.073 CenterY=124.221 CenterZ=0 NormalX=0 NormalY=0 NormalZ=1 AngleXU=0 Radius=1
    g217: Circle CenterX=366.073 CenterY=124.221 CenterZ=0 NormalX=0 NormalY=0 NormalZ=1 AngleXU=0 Radius=1
    g218: Circle CenterX=362.567 CenterY=122.294 CenterZ=0 NormalX=0 NormalY=0 NormalZ=1 AngleXU=0 Radius=1
    g219: BSplineCurve PolesCount=3 KnotsCount=2 Degree=2 IsPeriodic=0
    g220: GeomPoint X=362.073 Y=124.221 Z=0
    g221: GeomPoint X=362.567 Y=122.294 Z=0
    g222: Circle CenterX=322.073 CenterY=124.221 CenterZ=0 NormalX=0 NormalY=0 NormalZ=1 AngleXU=0 Radius=1
    g223: Circle CenterX=318.073 CenterY=124.221 CenterZ=0 NormalX=0 NormalY=0 NormalZ=1 AngleXU=0 Radius=1
    g224: Circle CenterX=318.073 CenterY=120.221 CenterZ=0 NormalX=0 NormalY=0 NormalZ=1 AngleXU=0 Radius=1
    g225: BSplineCurve PolesCount=3 KnotsCount=2 Degree=2 IsPeriodic=0
    g226: GeomPoint X=322.073 Y=124.221 Z=0
    g227: GeomPoint X=318.073 Y=120.221 Z=0
    g228: Circle CenterX=322.073 CenterY=105.865 CenterZ=0 NormalX=0 NormalY=0 NormalZ=1 AngleXU=0 Radius=1
    g229: Circle CenterX=318.073 CenterY=105.865 CenterZ=0 NormalX=0 NormalY=0 NormalZ=1 AngleXU=0 Radius=1
    g230: Circle CenterX=318.073 CenterY=109.865 CenterZ=0 NormalX=0 NormalY=0 NormalZ=1 AngleXU=0 Radius=1
    g231: BSplineCurve PolesCount=3 KnotsCount=2 Degree=2 IsPeriodic=0
    g232: GeomPoint X=322.073 Y=105.865 Z=0
    g233: GeomPoint X=318.073 Y=109.865 Z=0
    g234: Circle CenterX=336.157 CenterY=107.779 CenterZ=0 NormalX=0 NormalY=0 NormalZ=1 AngleXU=0 Radius=1
    g235: Circle CenterX=332.651 CenterY=105.853 CenterZ=0 NormalX=0 NormalY=0 NormalZ=1 AngleXU=0 Radius=1
    g236: Circle CenterX=328.643 CenterY=105.865 CenterZ=0 NormalX=0 NormalY=0 NormalZ=1 AngleXU=0 Radius=1
    g237: BSplineCurve PolesCount=3 KnotsCount=2 Degree=2 IsPeriodic=0
    g238: GeomPoint X=336.157 Y=107.779 Z=0
    g239: GeomPoint X=328.643 Y=105.865 Z=0
    g240: LineSegment StartX=322.073 StartY=124.221 StartZ=0 EndX=362.073 EndY=124.221 EndZ=0
    g241: Circle CenterX=371.567 CenterY=-80.8644 CenterZ=0 NormalX=0 NormalY=0 NormalZ=1 AngleXU=0 Radius=1
    g242: Circle CenterX=375.073 CenterY=-82.7896 CenterZ=0 NormalX=0 NormalY=0 NormalZ=1 AngleXU=0 Radius=1
    g243: Circle CenterX=375.073 CenterY=-78.7896 CenterZ=0 NormalX=0 NormalY=0 NormalZ=1 AngleXU=0 Radius=1
    g244: BSplineCurve PolesCount=3 KnotsCount=2 Degree=2 IsPeriodic=0
    g245: GeomPoint X=371.567 Y=-80.8644 Z=0
    g246: GeomPoint X=375.073 Y=-78.7896 Z=0
    g247: Circle CenterX=321.579 CenterY=-53.4075 CenterZ=0 NormalX=0 NormalY=0 NormalZ=1 AngleXU=0 Radius=1
    g248: Circle CenterX=318.073 CenterY=-51.4823 CenterZ=0 NormalX=0 NormalY=0 NormalZ=1 AngleXU=0 Radius=1
    g249: Circle CenterX=318.073 CenterY=-47.4805 CenterZ=0 NormalX=0 NormalY=0 NormalZ=1 AngleXU=0 Radius=1
    g250: BSplineCurve PolesCount=3 KnotsCount=2 Degree=2 IsPeriodic=0
    g251: GeomPoint X=321.579 Y=-53.4075 Z=0
    g252: GeomPoint X=318.073 Y=-47.4805 Z=0
    g253: LineSegment StartX=371.567 StartY=-80.8644 StartZ=0 EndX=321.579 EndY=-53.4075 EndZ=0
    g254: Circle CenterX=321.579 CenterY=-67.3492 CenterZ=0 NormalX=0 NormalY=0 NormalZ=1 AngleXU=0 Radius=1
    g255: Circle CenterX=318.073 CenterY=-65.424 CenterZ=0 NormalX=0 NormalY=0 NormalZ=1 AngleXU=0 Radius=1
    g256: Circle CenterX=318.073 CenterY=-69.424 CenterZ=0 NormalX=0 NormalY=0 NormalZ=1 AngleXU=0 Radius=1
    g257: BSplineCurve PolesCount=3 KnotsCount=2 Degree=2 IsPeriodic=0
    g258: GeomPoint X=321.579 Y=-67.3492 Z=0
    g259: GeomPoint X=318.073 Y=-69.424 Z=0
    g260: Circle CenterX=362.567 CenterY=-89.8542 CenterZ=0 NormalX=0 NormalY=0 NormalZ=1 AngleXU=0 Radius=1
    g261: Circle CenterX=366.073 CenterY=-91.7794 CenterZ=0 NormalX=0 NormalY=0 NormalZ=1 AngleXU=0 Radius=1
    g262: Circle CenterX=362.073 CenterY=-91.7794 CenterZ=0 NormalX=0 NormalY=0 NormalZ=1 AngleXU=0 Radius=1
    g263: BSplineCurve PolesCount=3 KnotsCount=2 Degree=2 IsPeriodic=0
    g264: GeomPoint X=362.567 Y=-89.8542 Z=0
    g265: GeomPoint X=362.073 Y=-91.7794 Z=0
    g266: Circle CenterX=322.073 CenterY=-91.7794 CenterZ=0 NormalX=0 NormalY=0 NormalZ=1 AngleXU=0 Radius=1
    g267: Circle CenterX=318.073 CenterY=-91.7794 CenterZ=0 NormalX=0 NormalY=0 NormalZ=1 AngleXU=0 Radius=1
    g268: Circle CenterX=318.073 CenterY=-87.7794 CenterZ=0 NormalX=0 NormalY=0 NormalZ=1 AngleXU=0 Radius=1
    g269: BSplineCurve PolesCount=3 KnotsCount=2 Degree=2 IsPeriodic=0
    g270: GeomPoint X=322.073 Y=-91.7794 Z=0
    g271: GeomPoint X=318.073 Y=-87.7794 Z=0
    g272: LineSegment StartX=362.567 StartY=-89.8542 StartZ=0 EndX=321.579 EndY=-67.3492 EndZ=0
    g273: LineSegment StartX=318.073 StartY=-69.424 StartZ=0 EndX=318.073 EndY=-87.7794 EndZ=0
    g274: LineSegment StartX=322.073 StartY=-91.7794 StartZ=0 EndX=362.073 EndY=-91.7794 EndZ=0
    g275: Circle CenterX=2.07281 CenterY=124.221 CenterZ=0 NormalX=0 NormalY=0 NormalZ=1 AngleXU=0 Radius=1
    g276: Circle CenterX=1.57905 CenterY=122.295 CenterZ=0 NormalX=0 NormalY=0 NormalZ=1 AngleXU=0 Radius=1
    g277: BSplineCurve PolesCount=3 KnotsCount=2 Degree=2 IsPeriodic=0
    g278: GeomPoint X=2.07281 Y=124.221 Z=0
    g279: GeomPoint X=1.57905 Y=122.295 Z=0
    g280: Circle CenterX=42.0728 CenterY=124.221 CenterZ=0 NormalX=0 NormalY=0 NormalZ=1 AngleXU=0 Radius=1
    g281: Circle CenterX=46.0728 CenterY=124.221 CenterZ=0 NormalX=0 NormalY=0 NormalZ=1 AngleXU=0 Radius=1
    g282: Circle CenterX=46.0728 CenterY=120.221 CenterZ=0 NormalX=0 NormalY=0 NormalZ=1 AngleXU=0 Radius=1
    g283: BSplineCurve PolesCount=3 KnotsCount=2 Degree=2 IsPeriodic=0
    g284: GeomPoint X=42.0728 Y=124.221 Z=0
    g285: GeomPoint X=46.0728 Y=120.221 Z=0
    g286: Circle CenterX=46.0728 CenterY=109.865 CenterZ=0 NormalX=0 NormalY=0 NormalZ=1 AngleXU=0 Radius=1
    g287: Circle CenterX=46.0728 CenterY=105.865 CenterZ=0 NormalX=0 NormalY=0 NormalZ=1 AngleXU=0 Radius=1
    g288: Circle CenterX=42.0728 CenterY=105.865 CenterZ=0 NormalX=0 NormalY=0 NormalZ=1 AngleXU=0 Radius=1
    g289: BSplineCurve PolesCount=3 KnotsCount=2 Degree=2 IsPeriodic=0
    g290: GeomPoint X=46.0728 Y=109.865 Z=0
    g291: GeomPoint X=42.0728 Y=105.865 Z=0
    g292: Circle CenterX=35.5028 CenterY=105.865 CenterZ=0 NormalX=0 NormalY=0 NormalZ=1 AngleXU=0 Radius=1
    g293: Circle CenterX=31.5028 CenterY=105.865 CenterZ=0 NormalX=0 NormalY=0 NormalZ=1 AngleXU=0 Radius=1
    g294: Circle CenterX=27.9965 CenterY=107.79 CenterZ=0 NormalX=0 NormalY=0 NormalZ=1 AngleXU=0 Radius=1
    g295: BSplineCurve PolesCount=3 KnotsCount=2 Degree=2 IsPeriodic=0
    g296: GeomPoint X=35.5028 Y=105.865 Z=0
    g297: GeomPoint X=27.9965 Y=107.79 Z=0
    g298: LineSegment StartX=2.07281 StartY=124.221 StartZ=0 EndX=42.0728 EndY=124.221 EndZ=0
    g299: LineSegment StartX=46.0728 StartY=120.221 StartZ=0 EndX=46.0728 EndY=109.865 EndZ=0
    g300: LineSegment StartX=42.0728 StartY=105.865 StartZ=0 EndX=35.5028 EndY=105.865 EndZ=0
    g301: LineSegment StartX=27.9965 StartY=107.79 StartZ=0 EndX=1.57905 EndY=122.295 EndZ=0
    g302: Circle CenterX=42.5666 CenterY=-67.3492 CenterZ=0 NormalX=0 NormalY=0 NormalZ=1 AngleXU=0 Radius=1
    g303: Circle CenterX=46.0728 CenterY=-65.424 CenterZ=0 NormalX=0 NormalY=0 NormalZ=1 AngleXU=0 Radius=1
    g304: Circle CenterX=46.0728 CenterY=-69.424 CenterZ=0 NormalX=0 NormalY=0 NormalZ=1 AngleXU=0 Radius=1
    g305: BSplineCurve PolesCount=3 KnotsCount=2 Degree=2 IsPeriodic=0
    g306: GeomPoint X=42.5666 Y=-67.3492 Z=0
    g307: GeomPoint X=46.0728 Y=-69.424 Z=0
    g308: Circle CenterX=46.0728 CenterY=-87.7794 CenterZ=0 NormalX=0 NormalY=0 NormalZ=1 AngleXU=0 Radius=1
    g309: Circle CenterX=46.0728 CenterY=-91.7794 CenterZ=0 NormalX=0 NormalY=0 NormalZ=1 AngleXU=0 Radius=1
    g310: Circle CenterX=42.0728 CenterY=-91.7794 CenterZ=0 NormalX=0 NormalY=0 NormalZ=1 AngleXU=0 Radius=1
    g311: BSplineCurve PolesCount=3 KnotsCount=2 Degree=2 IsPeriodic=0
    g312: GeomPoint X=46.0728 Y=-87.7794 Z=0
    g313: GeomPoint X=42.0728 Y=-91.7794 Z=0
    g314: Circle CenterX=2.07281 CenterY=-91.7794 CenterZ=0 NormalX=0 NormalY=0 NormalZ=1 AngleXU=0 Radius=1
    g315: Circle CenterX=-1.92719 CenterY=-91.7794 CenterZ=0 NormalX=0 NormalY=0 NormalZ=1 AngleXU=0 Radius=1
    g316: Circle CenterX=1.57905 CenterY=-89.8542 CenterZ=0 NormalX=0 NormalY=0 NormalZ=1 AngleXU=0 Radius=1
    g317: BSplineCurve PolesCount=3 KnotsCount=2 Degree=2 IsPeriodic=0
    g318: GeomPoint X=2.07281 Y=-91.7794 Z=0
    g319: GeomPoint X=1.57905 Y=-89.8542 Z=0
    g320: LineSegment StartX=2.07281 StartY=-91.7794 StartZ=0 EndX=42.0728 EndY=-91.7794 EndZ=0
    g321: LineSegment StartX=46.0728 StartY=-87.7794 StartZ=0 EndX=46.0728 EndY=-69.424 EndZ=0
    g322: LineSegment StartX=42.5666 StartY=-67.3492 StartZ=0 EndX=1.57905 EndY=-89.8542 EndZ=0
    g323: Circle CenterX=322.073 CenterY=76.4095 CenterZ=0 NormalX=0 NormalY=0 NormalZ=1 AngleXU=0 Radius=4
    g324: BSplineCurve PolesCount=3 KnotsCount=2 Degree=2 IsPeriodic=0
    g325: GeomPoint X=318.073 Y=72.4095 Z=0
    g326: GeomPoint X=322.073 Y=76.4095 Z=0
    g327: Circle CenterX=375.073 CenterY=72.4095 CenterZ=0 NormalX=0 NormalY=0 NormalZ=1 AngleXU=0 Radius=1
    g328: Circle CenterX=375.073 CenterY=76.4095 CenterZ=0 NormalX=0 NormalY=0 NormalZ=1 AngleXU=0 Radius=1
    g329: Circle CenterX=371.073 CenterY=76.4095 CenterZ=0 NormalX=0 NormalY=0 NormalZ=1 AngleXU=0 Radius=1
    g330: BSplineCurve PolesCount=3 KnotsCount=2 Degree=2 IsPeriodic=0
    g331: GeomPoint X=375.073 Y=72.4095 Z=0
    g332: GeomPoint X=371.073 Y=76.4095 Z=0
    g333: LineSegment StartX=322.073 StartY=76.4095 StartZ=0 EndX=371.073 EndY=76.4095 EndZ=0
    g334: LineSegment StartX=318.073 StartY=72.4095 StartZ=0 EndX=318.073 EndY=-47.4805 EndZ=0
    g335: LineSegment StartX=375.073 StartY=72.4095 StartZ=0 EndX=375.073 EndY=-78.7896 EndZ=0
    g336: ArcOfCircle CenterX=-26.9272 CenterY=22.1087 CenterZ=0 NormalX=0 NormalY=0 NormalZ=1 AngleXU=0 Radius=4 StartAngle=5e-16 EndAngle=3.14159
    g337: LineSegment StartX=-22.9272 StartY=22.1087 StartZ=0 EndX=-18.9272 EndY=-83.7794 EndZ=0
    g338: LineSegment StartX=-34.9272 StartY=-83.7794 StartZ=0 EndX=-30.9272 EndY=22.1087 EndZ=0
    g339: ArcOfCircle CenterX=391.073 CenterY=22.1087 CenterZ=0 NormalX=0 NormalY=0 NormalZ=1 AngleXU=0 Radius=4 StartAngle=0 EndAngle=3.14159
    g340: LineSegment StartX=387.073 StartY=22.1087 StartZ=0 EndX=383.073 EndY=-83.7794 EndZ=0
    g341: LineSegment StartX=395.073 StartY=22.1087 StartZ=0 EndX=399.073 EndY=-83.7794 EndZ=0
    g342: Circle CenterX=-10.9272 CenterY=-78.7794 CenterZ=0 NormalX=0 NormalY=0 NormalZ=1 AngleXU=0 Radius=1
    g343: Circle CenterX=-10.9272 CenterY=-82.7794 CenterZ=0 NormalX=0 NormalY=0 NormalZ=1 AngleXU=0 Radius=1
    g344: Circle CenterX=-7.42095 CenterY=-80.8542 CenterZ=0 NormalX=0 NormalY=0 NormalZ=1 AngleXU=0 Radius=1
    g345: BSplineCurve PolesCount=3 KnotsCount=2 Degree=2 IsPeriodic=0
    g346: GeomPoint X=-10.9272 Y=-78.7794 Z=0
    g347: GeomPoint X=-7.42095 Y=-80.8542 Z=0
    g348: Circle CenterX=42.5666 CenterY=-53.4075 CenterZ=0 NormalX=0 NormalY=0 NormalZ=1 AngleXU=0 Radius=1
    g349: Circle CenterX=46.0728 CenterY=-51.4823 CenterZ=0 NormalX=0 NormalY=0 NormalZ=1 AngleXU=0 Radius=1
    g350: Circle CenterX=46.0728 CenterY=-47.4823 CenterZ=0 NormalX=0 NormalY=0 NormalZ=1 AngleXU=0 Radius=1
    g351: BSplineCurve PolesCount=3 KnotsCount=2 Degree=2 IsPeriodic=0
    g352: GeomPoint X=42.5666 Y=-53.4075 Z=0
    g353: GeomPoint X=46.0728 Y=-47.4823 Z=0
    g354: Circle CenterX=46.0728 CenterY=72.4095 CenterZ=0 NormalX=0 NormalY=0 NormalZ=1 AngleXU=0 Radius=1
    g355: Circle CenterX=46.0728 CenterY=76.4095 CenterZ=0 NormalX=0 NormalY=0 NormalZ=1 AngleXU=0 Radius=1
    g356: Circle CenterX=42.0728 CenterY=76.4095 CenterZ=0 NormalX=0 NormalY=0 NormalZ=1 AngleXU=0 Radius=1
    g357: BSplineCurve PolesCount=3 KnotsCount=2 Degree=2 IsPeriodic=0
    g358: GeomPoint X=46.0728 Y=72.4095 Z=0
    g359: GeomPoint X=42.0728 Y=76.4095 Z=0
    g360: Circle CenterX=-6.92719 CenterY=76.4095 CenterZ=0 NormalX=0 NormalY=0 NormalZ=1 AngleXU=0 Radius=1
    g361: Circle CenterX=-10.9272 CenterY=76.4095 CenterZ=0 NormalX=0 NormalY=0 NormalZ=1 AngleXU=0 Radius=1
    g362: Circle CenterX=-10.9272 CenterY=72.4095 CenterZ=0 NormalX=0 NormalY=0 NormalZ=1 AngleXU=0 Radius=1
    g363: BSplineCurve PolesCount=3 KnotsCount=2 Degree=2 IsPeriodic=0
    g364: GeomPoint X=-6.92719 Y=76.4095 Z=0
    g365: GeomPoint X=-10.9272 Y=72.4095 Z=0
    g366: LineSegment StartX=-10.9272 StartY=72.4095 StartZ=0 EndX=-10.9272 EndY=-78.7794 EndZ=0
    g367: LineSegment StartX=-7.42095 StartY=-80.8542 StartZ=0 EndX=42.5666 EndY=-53.4075 EndZ=0
    g368: LineSegment StartX=46.0728 StartY=-47.4823 StartZ=0 EndX=46.0728 EndY=72.4095 EndZ=0
    g369: LineSegment StartX=42.0728 StartY=76.4095 StartZ=0 EndX=-6.92719 EndY=76.4095 EndZ=0
    g370: LineSegment StartX=-42.9272 StartY=136.221 StartZ=0 EndX=407.073 EndY=136.221 EndZ=0
    g371: LineSegment StartX=232.072 StartY=136.221 StartZ=0 EndX=220.072 EndY=136.221 EndZ=0
    g372: LineSegment StartX=232.072 StartY=136.221 StartZ=0 EndX=232.072 EndY=124.221 EndZ=0
    g373: LineSegment StartX=220.072 StartY=136.221 StartZ=0 EndX=220.072 EndY=124.221 EndZ=0
    g374: LineSegment StartX=220.072 StartY=136.221 StartZ=0 EndX=226.072 EndY=136.221 EndZ=0
    g375: LineSegment StartX=220.072 StartY=136.221 StartZ=0 EndX=220.072 EndY=130.221 EndZ=0
    g376: LineSegment StartX=220.072 StartY=124.221 StartZ=0 EndX=226.072 EndY=124.221 EndZ=0
    g377: LineSegment StartX=232.072 StartY=124.221 StartZ=0 EndX=232.072 EndY=127.221 EndZ=0
    g378: LineSegment StartX=232.072 StartY=136.221 StartZ=0 EndX=232.072 EndY=133.221 EndZ=0
    g379-g383: Circle x5 (B-spline internal-alignment scaffolding for g384; pole/knot coordinates omitted)
    g384: BSplineCurve PolesCount=5 KnotsCount=3 Degree=3 IsPeriodic=0
    g385: GeomPoint X=232.072 Y=133.221 Z=0
    g386: GeomPoint X=223.072 Y=130.221 Z=0
    g387: GeomPoint X=232.072 Y=127.221 Z=0
    g388: LineSegment StartX=189.124 StartY=124.221 StartZ=0 EndX=302.073 EndY=124.221 EndZ=0
    g389: LineSegment StartX=132.072 StartY=136.221 StartZ=0 EndX=132.072 EndY=124.221 EndZ=0
    g390: LineSegment StartX=132.072 StartY=136.221 StartZ=0 EndX=144.072 EndY=136.221 EndZ=0
    g391: LineSegment StartX=144.072 StartY=136.221 StartZ=0 EndX=144.072 EndY=124.221 EndZ=0
    g392: LineSegment StartX=144.072 StartY=136.221 StartZ=0 EndX=138.072 EndY=136.221 EndZ=0
    g393: LineSegment StartX=144.072 StartY=136.221 StartZ=0 EndX=144.072 EndY=130.221 EndZ=0
    g394: LineSegment StartX=132.072 StartY=136.221 StartZ=0 EndX=132.072 EndY=133.221 EndZ=0
    g395: LineSegment StartX=132.072 StartY=133.221 StartZ=0 EndX=132.072 EndY=127.221 EndZ=0
    g396-g400: Circle x5 (B-spline internal-alignment scaffolding for g401; pole/knot coordinates omitted)
    g401: BSplineCurve PolesCount=5 KnotsCount=3 Degree=3 IsPeriodic=0
    g402: GeomPoint X=132.072 Y=133.221 Z=0
    g403: GeomPoint X=141.072 Y=130.221 Z=0
    g404: GeomPoint X=132.072 Y=127.221 Z=0
    g405: LineSegment StartX=132.072 StartY=124.221 StartZ=0 EndX=175.022 EndY=124.221 EndZ=0
    g406: LineSegment StartX=62.0728 StartY=124.221 StartZ=0 EndX=132.072 EndY=124.221 EndZ=0
    g407: LineSegment StartX=132.072 StartY=136.221 StartZ=0 EndX=131.457 EndY=138.832 EndZ=0
    ... +61 more geometry lines
  constraints (808):
    c: Vertical(g0)
    c: Vertical(g1)
    c: Block(g1)
    c: Block(g0)
    c: Weight(g4) = 1
    c: Equal(g4,g5)
    c: Equal(g4,g6)
    c: InternalAlignment(g4,g7)
    c: InternalAlignment(g5,g7)
    c: InternalAlignment(g6,g7)
    c: InternalAlignment(g8,g7)
    c: InternalAlignment(g9,g7)
    c: Weight(g10) = 1
    c: Equal(g10,g11)
    c: Equal(g10,g12)
    c: InternalAlignment(g10,g13)
    c: InternalAlignment(g11,g13)
    c: InternalAlignment(g12,g13)
    c: InternalAlignment(g14,g13)
    c: InternalAlignment(g15,g13)
    c: Block(g13)
    c: Block(g7)
    c: Weight(g16) = 1
    c: Equal(g16,g17)
    c: Equal(g16,g18)
    c: InternalAlignment(g16,g19)
    c: InternalAlignment(g17,g19)
    c: InternalAlignment(g18,g19)
    c: InternalAlignment(g20,g19)
    c: InternalAlignment(g21,g19)
    c: Weight(g22) = 1
    c: Equal(g22,g23)
    c: Equal(g22,g24)
    c: InternalAlignment(g22,g25)
    c: InternalAlignment(g23,g25)
    c: InternalAlignment(g24,g25)
    c: InternalAlignment(g26,g25)
    c: InternalAlignment(g27,g25)
    c: Block(g25)
    c: Block(g19)
    c: Weight(g28) = 1
    c: Equal(g28,g29)
    c: Equal(g28,g30)
    c: InternalAlignment(g28,g31)
    c: InternalAlignment(g29,g31)
    c: InternalAlignment(g30,g31)
    c: InternalAlignment(g32,g31)
    c: InternalAlignment(g33,g31)
    c: Weight(g34) = 1
    c: Equal(g34,g35)
    c: Equal(g34,g36)
    c: InternalAlignment(g34,g37)
    c: InternalAlignment(g35,g37)
    c: InternalAlignment(g36,g37)
    c: InternalAlignment(g38,g37)
    c: InternalAlignment(g39,g37)
    c: Block(g31)
    c: Block(g37)
    c: Coincident(g40,g1)
    c: Coincident(g40,g0)
    c: Horizontal(g40)
    c: Distance(g40) = 450
    c: Weight(g41) = 1
    c: Equal(g41,g42)
    c: Equal(g41,g43)
    c: InternalAlignment(g41,g44)
    c: InternalAlignment(g42,g44)
    c: InternalAlignment(g43,g44)
    c: InternalAlignment(g45,g44)
    c: InternalAlignment(g46,g44)
    c: Block(g44)
    c: Weight(g47) = 1
    c: Equal(g47,g48)
    c: Equal(g47,g49)
    c: InternalAlignment(g47,g50)
    c: InternalAlignment(g48,g50)
    c: InternalAlignment(g49,g50)
    c: InternalAlignment(g51,g50)
    c: InternalAlignment(g52,g50)
    c: Block(g50)
    c: Weight(g53) = 1
    c: Equal(g53,g54)
    c: Equal(g53,g55)
    c: InternalAlignment(g53,g56)
    c: InternalAlignment(g54,g56)
    c: InternalAlignment(g55,g56)
    c: InternalAlignment(g57,g56)
    c: InternalAlignment(g58,g56)
    c: Block(g56)
    c: Weight(g59) = 1
    c: Equal(g59,g60)
    c: Equal(g59,g61)
    c: InternalAlignment(g59,g62)
    c: InternalAlignment(g60,g62)
    c: InternalAlignment(g61,g62)
    c: InternalAlignment(g63,g62)
    c: InternalAlignment(g64,g62)
    c: Block(g62)
    c: Weight(g65) = 1
    c: Equal(g65,g66)
    c: Equal(g65,g67)
    c: InternalAlignment(g65,g68)
    c: InternalAlignment(g66,g68)
    c: InternalAlignment(g67,g68)
    c: InternalAlignment(g69,g68)
    c: InternalAlignment(g70,g68)
    c: Weight(g71) = 1
    c: Equal(g71,g72)
    c: Equal(g71,g73)
    c: InternalAlignment(g71,g74)
    c: InternalAlignment(g72,g74)
    c: InternalAlignment(g73,g74)
    c: InternalAlignment(g75,g74)
    c: InternalAlignment(g76,g74)
    c: Block(g68)
    c: Block(g74)
    c: Coincident(g77,g68)
    c: Coincident(g77,g74)
    c: Vertical(g77)
    c: Coincident(g78,g68)
    c: Coincident(g78,g50)
    c: Coincident(g79,g50)
    c: Coincident(g79,g74)
    c: Weight(g80) = 1
    c: Equal(g80,g81)
    c: Equal(g80,g82)
    c: InternalAlignment(g80,g83)
    c: InternalAlignment(g81,g83)
    c: InternalAlignment(g82,g83)
    c: InternalAlignment(g84,g83)
    c: InternalAlignment(g85,g83)
    c: Weight(g86) = 1
    c: Equal(g86,g87)
    c: Equal(g86,g88)
    c: InternalAlignment(g86,g89)
    c: InternalAlignment(g87,g89)
    c: InternalAlignment(g88,g89)
    c: InternalAlignment(g90,g89)
    c: InternalAlignment(g91,g89)
    c: Block(g83)
    c: Block(g89)
    c: Coincident(g92,g83)
    c: Coincident(g92,g89)
    c: Vertical(g92)
    c: Coincident(g93,g83)
    c: Coincident(g93,g44)
    c: Coincident(g94,g44)
    c: Coincident(g94,g89)
    c: Weight(g95) = 1
    c: Equal(g95,g96)
    c: Equal(g95,g97)
    c: InternalAlignment(g95,g98)
    c: InternalAlignment(g96,g98)
    c: InternalAlignment(g97,g98)
    c: InternalAlignment(g99,g98)
    c: InternalAlignment(g100,g98)
    c: Weight(g101) = 1
    c: Equal(g101,g102)
    c: Equal(g101,g103)
    c: InternalAlignment(g101,g104)
    c: InternalAlignment(g102,g104)
    c: InternalAlignment(g103,g104)
    c: InternalAlignment(g105,g104)
    c: InternalAlignment(g106,g104)
    c: Block(g98)
    c: Block(g104)
    c: Coincident(g107,g98)
    c: Coincident(g107,g104)
    c: Vertical(g107)
    c: Coincident(g108,g104)
    c: Coincident(g108,g62)
    c: Coincident(g109,g62)
    c: Coincident(g109,g98)
    c: Weight(g110) = 1
    c: Equal(g110,g111)
    c: Equal(g110,g112)
    c: InternalAlignment(g110,g113)
    c: InternalAlignment(g111,g113)
    c: InternalAlignment(g112,g113)
    c: InternalAlignment(g114,g113)
    c: InternalAlignment(g115,g113)
    c: Weight(g116) = 1
    c: Equal(g116,g117)
    c: Equal(g116,g118)
    c: InternalAlignment(g116,g119)
    c: InternalAlignment(g117,g119)
    c: InternalAlignment(g118,g119)
    c: InternalAlignment(g120,g119)
    c: InternalAlignment(g121,g119)
    c: Block(g113)
    c: Block(g119)
    c: Coincident(g122,g113)
    c: Coincident(g122,g119)
    c: Vertical(g122)
    c: Coincident(g123,g119)
    c: Coincident(g123,g56)
    c: Coincident(g124,g56)
    c: Coincident(g124,g113)
    c: Weight(g125) = 1
    c: Equal(g125,g126)
    c: Equal(g125,g127)
    c: InternalAlignment(g125,g128)
    c: InternalAlignment(g126,g128)
    c: InternalAlignment(g127,g128)
    c: InternalAlignment(g129,g128)
    c: InternalAlignment(g130,g128)
    c: Weight(g131) = 1
    c: Equal(g131,g132)
    c: Equal(g131,g133)
    c: InternalAlignment(g131,g134)
    c: InternalAlignment(g132,g134)
    c: InternalAlignment(g133,g134)
    c: InternalAlignment(g135,g134)
    c: InternalAlignment(g136,g134)
    c: Weight(g137) = 1
    c: Equal(g137,g138)
    c: Equal(g137,g139)
    c: InternalAlignment(g137,g140)
    c: InternalAlignment(g138,g140)
    c: InternalAlignment(g139,g140)
    c: InternalAlignment(g141,g140)
    c: InternalAlignment(g142,g140)
    c: Weight(g143) = 1
    c: Equal(g143,g144)
    c: Equal(g143,g145)
    c: InternalAlignment(g143,g146)
    c: InternalAlignment(g144,g146)
    c: InternalAlignment(g145,g146)
    c: InternalAlignment(g147,g146)
    c: InternalAlignment(g148,g146)
    c: Block(g146)
    c: Block(g140)
    c: Block(g134)
    c: Block(g128)
    c: Coincident(g149,g25)
    c: Coincident(g149,g146)
    c: Coincident(g150,g146)
    c: Coincident(g150,g140)
    c: Horizontal(g150)
    c: Coincident(g151,g140)
    c: Coincident(g151,g25)
    c: Vertical(g151)
    c: Coincident(g152,g19)
    c: Coincident(g152,g134)
    c: Vertical(g152)
    c: Coincident(g153,g134)
    c: Coincident(g153,g128)
    c: Horizontal(g153)
    c: Coincident(g154,g128)
    c: Coincident(g154,g19)
    c: Weight(g155) = 1
    c: Equal(g155,g156)
    c: Equal(g155,g157)
    c: InternalAlignment(g155,g158)
    c: InternalAlignment(g156,g158)
    c: InternalAlignment(g157,g158)
    c: InternalAlignment(g159,g158)
    c: InternalAlignment(g160,g158)
    c: Weight(g161) = 1
    c: Equal(g161,g162)
    c: Equal(g161,g163)
    c: InternalAlignment(g161,g164)
    c: InternalAlignment(g162,g164)
    c: InternalAlignment(g163,g164)
    c: InternalAlignment(g165,g164)
    c: InternalAlignment(g166,g164)
    c: Weight(g167) = 1
    c: Equal(g167,g168)
    c: Equal(g167,g169)
    c: InternalAlignment(g167,g170)
    c: InternalAlignment(g168,g170)
    c: InternalAlignment(g169,g170)
    c: InternalAlignment(g171,g170)
    c: InternalAlignment(g172,g170)
    c: Weight(g173) = 1
    c: Equal(g173,g174)
    c: Equal(g173,g175)
    c: InternalAlignment(g173,g176)
    c: InternalAlignment(g174,g176)
    c: InternalAlignment(g175,g176)
    c: InternalAlignment(g177,g176)
    c: InternalAlignment(g178,g176)
    c: Block(g176)
    c: Block(g170)
    c: Block(g164)
    c: Block(g158)
    c: Coincident(g179,g170)
    c: Coincident(g179,g7)
    c: Vertical(g179)
    c: Coincident(g180,g13)
    c: Coincident(g180,g164)
    c: Vertical(g180)
    c: Coincident(g181,g158)
    c: Coincident(g181,g13)
    c: Coincident(g182,g7)
    c: Weight(g183) = 1
    c: Equal(g183,g184)
    c: Equal(g183,g185)
    c: InternalAlignment(g183,g186)
    c: InternalAlignment(g184,g186)
    c: InternalAlignment(g185,g186)
    c: InternalAlignment(g187,g186)
    c: InternalAlignment(g188,g186)
    c: Weight(g189) = 1
    c: Equal(g189,g190)
    c: Equal(g189,g191)
    c: InternalAlignment(g189,g192)
    c: InternalAlignment(g190,g192)
    c: InternalAlignment(g191,g192)
    c: InternalAlignment(g193,g192)
    c: InternalAlignment(g194,g192)
    c: Block(g192)
    c: Block(g186)
    c: Coincident(g195,g192)
    c: Coincident(g195,g31)
    c: Coincident(g196,g31)
    c: Coincident(g196,g186)
    c: Coincident(g197,g186)
    c: Coincident(g197,g192)
    c: Vertical(g197)
    c: Weight(g198) = 1
    c: Equal(g198,g199)
    c: Equal(g198,g200)
    c: InternalAlignment(g198,g201)
    c: InternalAlignment(g199,g201)
    c: InternalAlignment(g200,g201)
    c: InternalAlignment(g202,g201)
    c: InternalAlignment(g203,g201)
    c: Weight(g204) = 1
    c: Equal(g204,g205)
    c: Equal(g204,g206)
    c: InternalAlignment(g204,g207)
    c: InternalAlignment(g205,g207)
    c: InternalAlignment(g206,g207)
    c: InternalAlignment(g208,g207)
    c: InternalAlignment(g209,g207)
    c: Block(g207)
    c: Block(g201)
    c: Coincident(g210,g201)
    c: Coincident(g210,g37)
    c: Coincident(g211,g37)
    c: Coincident(g211,g207)
    c: Coincident(g212,g207)
    c: Coincident(g212,g201)
    c: Vertical(g212)
    c: Horizontal(g213)
    c: Block(g213)
    c: Vertical(g214)
    c: Block(g214)
    c: Block(g215)
    c: Weight(g216) = 1
    c: Equal(g216,g217)
    c: Equal(g216,g218)
    c: InternalAlignment(g216,g219)
    c: InternalAlignment(g217,g219)
    c: InternalAlignment(g218,g219)
    c: InternalAlignment(g220,g219)
    c: InternalAlignment(g221,g219)
    c: Weight(g222) = 1
    c: Equal(g222,g223)
    c: Equal(g222,g224)
    c: InternalAlignment(g222,g225)
    c: InternalAlignment(g223,g225)
    c: InternalAlignment(g224,g225)
    c: InternalAlignment(g226,g225)
    c: InternalAlignment(g227,g225)
    c: Weight(g228) = 1
    c: Equal(g228,g229)
    c: Equal(g228,g230)
    c: InternalAlignment(g228,g231)
    c: InternalAlignment(g229,g231)
    c: InternalAlignment(g230,g231)
    c: InternalAlignment(g232,g231)
    c: InternalAlignment(g233,g231)
    c: Weight(g234) = 1
    c: Equal(g234,g235)
    c: Equal(g234,g236)
    c: InternalAlignment(g234,g237)
    c: InternalAlignment(g235,g237)
    c: InternalAlignment(g236,g237)
    c: InternalAlignment(g238,g237)
    c: InternalAlignment(g239,g237)
    c: Block(g219)
    c: Block(g225)
    c: Block(g231)
    c: Block(g237)
    c: Coincident(g240,g225)
    c: Coincident(g240,g219)
    c: Horizontal(g240)
    c: Block(g182)
    c: Weight(g241) = 1
    c: Equal(g241,g242)
    c: Equal(g241,g243)
    c: InternalAlignment(g241,g244)
    c: InternalAlignment(g242,g244)
    c: InternalAlignment(g243,g244)
    c: InternalAlignment(g245,g244)
    c: InternalAlignment(g246,g244)
    c: Weight(g247) = 1
    c: Equal(g247,g248)
    c: Equal(g247,g249)
    c: InternalAlignment(g247,g250)
    c: InternalAlignment(g248,g250)
    c: InternalAlignment(g249,g250)
    c: InternalAlignment(g251,g250)
    c: InternalAlignment(g252,g250)
    c: Block(g244)
    c: Block(g250)
    c: Coincident(g253,g244)
    c: Coincident(g253,g250)
    c: Weight(g254) = 1
    c: Equal(g254,g255)
    c: Equal(g254,g256)
    c: InternalAlignment(g254,g257)
    c: InternalAlignment(g255,g257)
    c: InternalAlignment(g256,g257)
    c: InternalAlignment(g258,g257)
    c: InternalAlignment(g259,g257)
    c: Weight(g260) = 1
    c: Equal(g260,g261)
    c: Equal(g260,g262)
    c: InternalAlignment(g260,g263)
    c: InternalAlignment(g261,g263)
    c: InternalAlignment(g262,g263)
    c: InternalAlignment(g264,g263)
    c: InternalAlignment(g265,g263)
    c: Weight(g266) = 1
    c: Equal(g266,g267)
    c: Equal(g266,g268)
    c: InternalAlignment(g266,g269)
    c: InternalAlignment(g267,g269)
    c: InternalAlignment(g268,g269)
    c: InternalAlignment(g270,g269)
    c: InternalAlignment(g271,g269)
    c: Block(g269)
    c: Block(g263)
    c: Block(g257)
    c: Coincident(g272,g263)
    c: Coincident(g272,g257)
    c: Coincident(g273,g257)
    c: Coincident(g273,g269)
    c: Vertical(g273)
    c: Coincident(g274,g269)
    c: Coincident(g274,g263)
    c: Horizontal(g274)
    c: Weight(g275) = 1
    c: Equal(g275,g276)
    c: InternalAlignment(g275,g277)
    c: InternalAlignment(g276,g277)
    c: InternalAlignment(g278,g277)
    c: InternalAlignment(g279,g277)
    c: Weight(g280) = 1
    c: InternalAlignment(g281,g283)
    c: InternalAlignment(g282,g283)
    c: InternalAlignment(g284,g283)
    c: InternalAlignment(g285,g283)
    c: Weight(g286) = 1
    c: Equal(g286,g287)
    c: Equal(g286,g288)
    c: InternalAlignment(g286,g289)
    c: InternalAlignment(g287,g289)
    c: InternalAlignment(g288,g289)
    c: InternalAlignment(g290,g289)
    c: InternalAlignment(g291,g289)
    c: Equal(g292,g293)
    c: Equal(g292,g294)
    c: InternalAlignment(g292,g295)
    c: InternalAlignment(g293,g295)
    c: InternalAlignment(g294,g295)
    c: InternalAlignment(g296,g295)
    c: InternalAlignment(g297,g295)
    c: Block(g283)
    c: Block(g289)
    c: Block(g295)
    c: Block(g277)
    c: Coincident(g298,g277)
    c: Coincident(g298,g283)
    c: Horizontal(g298)
    c: Coincident(g299,g283)
    c: Coincident(g299,g289)
    c: Vertical(g299)
    c: Coincident(g300,g289)
    c: Coincident(g300,g295)
    c: Horizontal(g300)
    c: Coincident(g301,g295)
    c: Coincident(g301,g277)
    c: Weight(g302) = 1
    c: Equal(g302,g303)
    c: Equal(g302,g304)
    c: InternalAlignment(g302,g305)
    c: InternalAlignment(g303,g305)
    c: InternalAlignment(g304,g305)
    c: InternalAlignment(g306,g305)
    c: InternalAlignment(g307,g305)
    c: Weight(g308) = 1
    c: Equal(g308,g309)
    c: Equal(g308,g310)
    c: InternalAlignment(g308,g311)
    c: InternalAlignment(g309,g311)
    c: InternalAlignment(g310,g311)
    c: InternalAlignment(g312,g311)
    c: Weight(g314) = 1
    c: Equal(g314,g315)
    c: Equal(g314,g316)
    c: InternalAlignment(g314,g317)
    c: InternalAlignment(g315,g317)
    c: InternalAlignment(g316,g317)
    c: InternalAlignment(g318,g317)
    c: InternalAlignment(g319,g317)
    c: Block(g317)
    c: Block(g311)
    c: Block(g305)
    c: Coincident(g320,g317)
    c: Coincident(g320,g311)
    c: Horizontal(g320)
    c: Coincident(g321,g311)
    c: Coincident(g321,g305)
    c: Vertical(g321)
    c: Coincident(g322,g305)
    c: Coincident(g322,g317)
    c: InternalAlignment(g323,g324)
    c: InternalAlignment(g325,g324)
    c: InternalAlignment(g326,g324)
    c: Block(g324)
    c: Equal(g327,g328)
    c: Equal(g327,g329)
    c: InternalAlignment(g327,g330)
    c: InternalAlignment(g328,g330)
    c: InternalAlignment(g329,g330)
    c: InternalAlignment(g331,g330)
    c: InternalAlignment(g332,g330)
    c: Block(g330)
    c: Coincident(g333,g324)
    c: Horizontal(g333)
    c: Block(g333)
    c: Coincident(g334,g324)
    c: Coincident(g334,g250)
    c: Vertical(g334)
    c: Coincident(g335,g330)
    c: Coincident(g335,g244)
    c: Vertical(g335)
    c: Block(g336)
    c: Block(g2)
    c: Distance(g334) = 119.89
    c: Coincident(g337,g336)
    c: Coincident(g337,g2)
    c: Coincident(g338,g2)
    c: Coincident(g338,g336)
    c: Block(g3)
    c: Block(g339)
    c: Coincident(g340,g339)
    c: Coincident(g340,g3)
    c: Coincident(g341,g339)
    c: Coincident(g341,g3)
    c: Block(g341)
    c: Block(g340)
    c: Weight(g342) = 1
    c: Equal(g342,g344)
    c: InternalAlignment(g342,g345)
    c: InternalAlignment(g343,g345)
    c: InternalAlignment(g344,g345)
    c: InternalAlignment(g346,g345)
    c: InternalAlignment(g347,g345)
    c: InternalAlignment(g352,g351)
    c: InternalAlignment(g353,g351)
    c: InternalAlignment(g355,g357)
    c: Horizontal(g369)
    c: Coincident(g370,g0)
    c: Horizontal(g370)
    c: Block(g370)
    c: Distance(g370) = 450
    c: Horizontal(g371)
    c: Distance(g371) = 12
    c: Coincident(g373,g371)
    c: Vertical(g373)
    c: Horizontal(g374)
    c: Vertical(g375)
    c: Distance(g375) = 6
    c: Coincident(g375,g371)
    c: Coincident(g374,g371)
    c: Block(g373)
    c: Coincident(g376,g373)
    c: Horizontal(g376)
    c: Distance(g376) = 6
    c: Vertical(g377)
    c: Distance(g377) = 3
    c: Vertical(g378)
    c: Distance(g378) = 3
    c: Coincident(g372,g377)
    c: Coincident(g384,g378)
    c: Weight(g379) = 1
    c: Equal(g379,g380)
    c: Coincident(g380,g374)
    c: Equal(g379,g381)
    c: Coincident(g381,g375)
    c: Equal(g379,g382)
    c: Coincident(g382,g376)
    c: Equal(g379,g383)
    c: Coincident(g384,g377)
    c: InternalAlignment(g379-g383 -> g384) x5
    c: InternalAlignment(g385,g384)
    c: InternalAlignment(g386,g384)
    c: InternalAlignment(g387,g384)
    c: Coincident(g388,g164)
    c: Coincident(g388,g158)
    c: Coincident(g392,g390)
    c: Vertical(g393)
    c: Distance(g393) = 6
    c: Coincident(g393,g390)
    c: Vertical(g394)
    c: Distance(g394) = 3
    c: Vertical(g395)
    c: Distance(g395) = 6
    c: Coincident(g395,g394)
    c: Coincident(g401,g394)
    c: Weight(g396) = 1
    c: Equal(g396,g397)
    c: Coincident(g397,g392)
    c: Equal(g396,g398)
    c: Coincident(g398,g393)
    c: Equal(g396,g399)
    c: Equal(g396,g400)
    c: Coincident(g401,g395)
    c: InternalAlignment(g396-g400 -> g401) x5
    c: InternalAlignment(g402,g401)
    c: InternalAlignment(g403,g401)
    c: InternalAlignment(g404,g401)
    c: Coincident(g405,g389)
    c: Coincident(g405,g170)
    c: Horizontal(g405)
    c: Block(g401)
    c: Coincident(g406,g176)
    c: Coincident(g406,g389)
    c: Horizontal(g406)
    c: Block(g405)
    c: Coincident(g408,g389)
    c: PointOnObject(g408,g153)
    c: Vertical(g408)
    c: Block(g409)
    c: Coincident(g410,g409)
    c: Vertical(g410)
    c: PointOnObject(g410,g40)
    c: Block(g410)
    c: Coincident(g411,g409)
    c: Vertical(g411)
    c: Block(g411)
    c: Vertical(g412)
    c: Distance(g412) = 3
    c: Equal(g379,g415) = 1
    c: Equal(g415,g416)
    c: InternalAlignment(g415,g417)
    c: InternalAlignment(g416,g417)
    c: InternalAlignment(g413,g417)
    c: InternalAlignment(g414,g417)
    c: InternalAlignment(g418,g417)
    c: Block(g417)
    c: Coincident(g418,g412)
    c: Coincident(g419,g417)
    c: PointOnObject(g419,g150)
    c: Vertical(g419)
    c: Distance(g420) = 3
    c: Block(g420)
    c: Distance(g421) = 3
    c: Parallel(g421,g420)
    c: Coincident(g421,g420)
    c: Coincident(g422,g420)
    c: Perpendicular(g422,g420)
    c: Distance(g422) = 3
    c: Coincident(g423,g421)
    c: Perpendicular(g423,g421)
    c: Distance(g423) = 3
    c: Coincident(g424,g420)
    c: Perpendicular(g424,g421)
    c: Distance(g424) = 6
    c: Coincident(g425,g424)
    c: PointOnObject(g423,g425)
    c: Coincident(g426,g420)
    c: PointOnObject(g426,g79)
    c: Block(g426)
    c: Distance(g427) = 2.76
    c: Coincident(g428,g427)
    c: Parallel(g427,g428)
    c: PointOnObject(g428,g181)
    c: Distance(g428) = 2.41
    c: Block(g428)
    c: Coincident(g429,g427)
    c: Distance(g429) = 6.6
    c: Perpendicular(g429,g428)
    c: Distance(g430) = 6.6
    c: Coincident(g431,g429)
    c: Coincident(g431,g430)
    c: Block(g432)
    c: Coincident(g433,g432)
    c: Vertical(g433)
    c: Distance(g433) = 3.6
    c: Coincident(g434,g427)
    c: Parallel(g427,g434)
    c: PointOnObject(g434,g78)
    c: Block(g434)
    c: Coincident(g435,g421)
    c: Parallel(g435,g421)
    c: PointOnObject(g435,g211)
    c: Block(g435)
    c: Coincident(g436,g435)
    c: Vertical(g436)
    c: PointOnObject(g436,g210)
    c: Coincident(g437,g436)
    c: Perpendicular(g437,g210)
    c: Distance(g437) = 3
    c: Coincident(g438,g437)
    c: Block(g437)
    c: Distance(g438) = 3
    c: Parallel(g437,g438)
    c: Coincident(g439,g438)
    c: Distance(g439) = 3
    c: Parallel(g438,g439)
    c: Coincident(g440,g439)
    c: Parallel(g440,g437)
    c: PointOnObject(g440,g124)
    c: PointOnObject(g441,g53)
    c: Tangent(g440,g441)
    c: Coincident(g442,g439)
    c: Perpendicular(g442,g439)
    c: Coincident(g443,g437)
    c: Parallel(g443,g442)
    c: Distance(g443) = 3
    c: Distance(g442) = 3
    c: PointOnObject(g442,g444)
    c: Block(g444)
    c: PointOnObject(g445,g123)
    c: Perpendicular(g123,g445)
    c: Distance(g445) = 2.41
    c: Block(g445)
    c: Coincident(g446,g445)
    c: Perpendicular(g123,g446)
    c: Distance(g446) = 2.76
    c: Coincident(g447,g446)
    c: Perpendicular(g123,g447)
    c: PointOnObject(g447,g149)
    c: Coincident(g448,g445)
    c: Parallel(g123,g448)
    c: Distance(g448) = 6.6
    c: Coincident(g449,g446)
    c: Parallel(g123,g449)
    c: Coincident(g450,g448)
    c: Distance(g449) = 6.6
    c: Coincident(g449,g450)
    c: Block(g149)
    c: Block(g124)
    c: Block(g211)
    c: Block(g181)
    c: Block(g78)
    c: Block(g79)
    c: Block(g430)
    c: Coincident(g451,g447)
    c: Distance(g451) = 46
    c: Parallel(g149,g451)
    c: Coincident(g452,g451)
    c: Horizontal(g452)
    c: PointOnObject(g452,g154)
    c: Coincident(g453,g451)
    c: Vertical(g453)
    c: Distance(g453) = 9
    c: Block(g452)
    c: PointOnObject(g454,g93)
    c: Distance(g455) = 6.6
    c: Distance(g456) = 6.6
    c: Block(g454)
    c: Coincident(g457,g456)
    c: Coincident(g457,g455)
    c: Perpendicular(g457,g182)
    c: Coincident(g458,g455)
    c: Perpendicular(g458,g182)
    c: PointOnObject(g458,g182)
    c: Block(g458)
    c: Block(g457)
    c: Block(g456)
    c: PointOnObject(g459,g196)
    c: Perpendicular(g196,g459)
    c: Distance(g459) = 3
    c: Coincident(g460,g459)
    c: Perpendicular(g196,g460)
    c: Distance(g460) = 3
    c: Coincident(g461,g460)
    c: Perpendicular(g196,g461)
    c: Distance(g461) = 3
    c: Coincident(g462,g461)
    c: Tangent(g462,g41)
    c: PointOnObject(g462,g94)
    c: Block(g462)
    c: Block(g459)
    c: Coincident(g463,g459)
    c: Parallel(g196,g463)
    c: Distance(g463) = 3
    c: Coincident(g464,g461)
    c: Distance(g464) = 3
    c: Parallel(g196,g464)
    c: Coincident(g465,g460)
    c: Distance(g465) = 6
    c: Parallel(g465,g196)
    c: Coincident(g466,g465)
    c: PointOnObject(g464,g466)
    c: Block(g466)
    c: Coincident(g467,g458)
    c: Vertical(g467)
    c: PointOnObject(g467,g195)
    c: Coincident(g468,g467)
    c: Perpendicular(g195,g468)
FEATURE [Sketcher::SketchObject] Sketch004  label="rightSideBottom"
  FullyConstrained = false
  sketch-geometry (91):
    g0: ArcOfCircle CenterX=391.073 CenterY=-83.7794 CenterZ=0 NormalX=0 NormalY=0 NormalZ=1 AngleXU=0 Radius=8 StartAngle=3.14159 EndAngle=6.28319
    g1: Circle CenterX=306.073 CenterY=-81.8102 CenterZ=0 NormalX=0 NormalY=0 NormalZ=1 AngleXU=0 Radius=1
    g2: Circle CenterX=306.073 CenterY=-77.8102 CenterZ=0 NormalX=0 NormalY=0 NormalZ=1 AngleXU=0 Radius=1
    g3: Circle CenterX=302.567 CenterY=-42.9683 CenterZ=0 NormalX=0 NormalY=0 NormalZ=1 AngleXU=0 Radius=1
    g4: Circle CenterX=306.073 CenterY=-44.8935 CenterZ=0 NormalX=0 NormalY=0 NormalZ=1 AngleXU=0 Radius=1
    g5: Circle CenterX=306.073 CenterY=-40.8935 CenterZ=0 NormalX=0 NormalY=0 NormalZ=1 AngleXU=0 Radius=1
    g6: BSplineCurve PolesCount=3 KnotsCount=2 Degree=2 IsPeriodic=0
    g7: GeomPoint X=302.567 Y=-42.9683 Z=0
    g8: GeomPoint X=306.073 Y=-40.8935 Z=0
    g9: Circle CenterX=371.567 CenterY=-80.8644 CenterZ=0 NormalX=0 NormalY=0 NormalZ=1 AngleXU=0 Radius=1
    g10: Circle CenterX=375.073 CenterY=-82.7896 CenterZ=0 NormalX=0 NormalY=0 NormalZ=1 AngleXU=0 Radius=1
    g11: Circle CenterX=375.073 CenterY=-78.7896 CenterZ=0 NormalX=0 NormalY=0 NormalZ=1 AngleXU=0 Radius=1
    g12: GeomPoint X=371.567 Y=-80.8644 Z=0
    g13: GeomPoint X=375.073 Y=-78.7896 Z=0
    g14: Circle CenterX=318.073 CenterY=-51.4823 CenterZ=0 NormalX=0 NormalY=0 NormalZ=1 AngleXU=0 Radius=1
    g15: Circle CenterX=318.073 CenterY=-47.4805 CenterZ=0 NormalX=0 NormalY=0 NormalZ=1 AngleXU=0 Radius=1
    g16: GeomPoint X=321.579 Y=-53.4075 Z=0
    g17: GeomPoint X=318.073 Y=-47.4805 Z=0
    g18: Circle CenterX=321.579 CenterY=-67.3492 CenterZ=0 NormalX=0 NormalY=0 NormalZ=1 AngleXU=0 Radius=1
    g19: Circle CenterX=318.073 CenterY=-65.424 CenterZ=0 NormalX=0 NormalY=0 NormalZ=1 AngleXU=0 Radius=1
    g20: Circle CenterX=318.073 CenterY=-69.424 CenterZ=0 NormalX=0 NormalY=0 NormalZ=1 AngleXU=0 Radius=1
    g21: GeomPoint X=321.579 Y=-67.3492 Z=0
    g22: GeomPoint X=318.073 Y=-69.424 Z=0
    g23: Circle CenterX=362.567 CenterY=-89.8542 CenterZ=0 NormalX=0 NormalY=0 NormalZ=1 AngleXU=0 Radius=1
    g24: Circle CenterX=366.073 CenterY=-91.7794 CenterZ=0 NormalX=0 NormalY=0 NormalZ=1 AngleXU=0 Radius=1
    g25: Circle CenterX=362.073 CenterY=-91.7794 CenterZ=0 NormalX=0 NormalY=0 NormalZ=1 AngleXU=0 Radius=1
    g26: GeomPoint X=362.567 Y=-89.8542 Z=0
    g27: GeomPoint X=362.073 Y=-91.7794 Z=0
    g28: Circle CenterX=322.073 CenterY=-91.7794 CenterZ=0 NormalX=0 NormalY=0 NormalZ=1 AngleXU=0 Radius=1
    g29: Circle CenterX=318.073 CenterY=-91.7794 CenterZ=0 NormalX=0 NormalY=0 NormalZ=1 AngleXU=0 Radius=1
    g30: Circle CenterX=318.073 CenterY=-87.7794 CenterZ=0 NormalX=0 NormalY=0 NormalZ=1 AngleXU=0 Radius=1
    g31: GeomPoint X=322.073 Y=-91.7794 Z=0
    g32: GeomPoint X=318.073 Y=-87.7794 Z=0
    g33: ArcOfCircle CenterX=391.073 CenterY=22.1087 CenterZ=0 NormalX=0 NormalY=0 NormalZ=1 AngleXU=0 Radius=4 StartAngle=0 EndAngle=3.14159
    g34: LineSegment StartX=387.073 StartY=22.1087 StartZ=0 EndX=383.073 EndY=-83.7794 EndZ=0
    g35: LineSegment StartX=395.073 StartY=22.1087 StartZ=0 EndX=399.073 EndY=-83.7794 EndZ=0
    g36: LineSegment StartX=232.072 StartY=-103.779 StartZ=0 EndX=232.072 EndY=-100.779 EndZ=0
    g37: GeomPoint X=232.072 Y=-94.7794 Z=0
    g38: GeomPoint X=223.072 Y=-97.7794 Z=0
    g39: Circle CenterX=232.072 CenterY=-94.7794 CenterZ=0 NormalX=0 NormalY=0 NormalZ=1 AngleXU=0 Radius=1
    g40: Circle CenterX=232.072 CenterY=-100.779 CenterZ=0 NormalX=0 NormalY=0 NormalZ=1 AngleXU=0 Radius=1
    g41: BSplineCurve PolesCount=5 KnotsCount=3 Degree=3 IsPeriodic=0
    g42: GeomPoint X=232.072 Y=-100.779 Z=0
    g43: LineSegment StartX=232.072 StartY=-94.7794 StartZ=0 EndX=232.072 EndY=-91.7794 EndZ=0
    g44: LineSegment StartX=245.072 StartY=-31.3037 StartZ=0 EndX=243.535 EndY=-33.1602 EndZ=0
    g45: LineSegment StartX=241.775 StartY=-35.2862 StartZ=0 EndX=240.266 EndY=-37.1092 EndZ=0
    g46: LineSegment StartX=243.535 StartY=-33.1602 StartZ=0 EndX=248.619 EndY=-37.3688 EndZ=0
    g47: LineSegment StartX=241.775 StartY=-35.2862 StartZ=0 EndX=246.859 EndY=-39.4949 EndZ=0
    g48: LineSegment StartX=248.619 StartY=-37.3688 StartZ=0 EndX=246.859 EndY=-39.4949 EndZ=0
    g49: LineSegment StartX=232.072 StartY=-103.779 StartZ=0 EndX=407.073 EndY=-103.779 EndZ=0
    g50: LineSegment StartX=299.888 StartY=-86.6413 StartZ=0 EndX=240.266 EndY=-37.1092 EndZ=0
    g51: LineSegment StartX=245.072 StartY=-11.4025 StartZ=0 EndX=302.567 EndY=-42.9683 EndZ=0
    g52: BSplineCurve PolesCount=3 KnotsCount=2 Degree=2 IsPeriodic=0
    g53: BSplineCurve PolesCount=3 KnotsCount=2 Degree=2 IsPeriodic=0
    g54: LineSegment StartX=321.579 StartY=-53.4075 StartZ=0 EndX=371.567 EndY=-80.8644 EndZ=0
    g55: BSplineCurve PolesCount=3 KnotsCount=2 Degree=2 IsPeriodic=0
    g56: BSplineCurve PolesCount=3 KnotsCount=2 Degree=2 IsPeriodic=0
    g57: BSplineCurve PolesCount=3 KnotsCount=2 Degree=2 IsPeriodic=0
    g58: LineSegment StartX=318.073 StartY=-69.424 StartZ=0 EndX=318.073 EndY=-87.7794 EndZ=0
    g59: LineSegment StartX=321.579 StartY=-67.3492 StartZ=0 EndX=362.567 EndY=-89.8542 EndZ=0
    g60: LineSegment StartX=362.073 StartY=-91.7794 StartZ=0 EndX=322.073 EndY=-91.7794 EndZ=0
    g61: BSplineCurve PolesCount=3 KnotsCount=2 Degree=2 IsPeriodic=0
    g62: BSplineCurve PolesCount=3 KnotsCount=2 Degree=2 IsPeriodic=0
    g63: LineSegment StartX=245.072 StartY=-31.3037 StartZ=0 EndX=302.996 EndY=-79.2541 EndZ=0
    g64: LineSegment StartX=302.567 StartY=-56.9099 StartZ=0 EndX=239.193 EndY=-22.1109 EndZ=0
    g65: LineSegment StartX=306.073 StartY=-62.8351 StartZ=0 EndX=306.073 EndY=-77.8102 EndZ=0
    g66: BSplineCurve PolesCount=3 KnotsCount=2 Degree=2 IsPeriodic=0
    g67: LineSegment StartX=298.776 StartY=-91.7794 StartZ=0 EndX=232.072 EndY=-91.7794 EndZ=0
    g68: LineSegment StartX=245.072 StartY=-11.4025 StartZ=0 EndX=243.628 EndY=-14.0323 EndZ=0
    g69: LineSegment StartX=240.741 StartY=-19.2917 StartZ=0 EndX=239.193 EndY=-22.1109 EndZ=0
    g70: LineSegment StartX=243.628 StartY=-14.0323 StartZ=0 EndX=246.258 EndY=-15.476 EndZ=0
    g71: LineSegment StartX=240.741 StartY=-19.2917 StartZ=0 EndX=243.37 EndY=-20.7355 EndZ=0
    g72: ArcOfCircle CenterX=247.444 CenterY=-19.5495 CenterZ=0 NormalX=0 NormalY=0 NormalZ=1 AngleXU=0 Radius=4.24264 StartAngle=3.4249 EndAngle=8.13729
    g73: LineSegment StartX=407.073 StartY=-103.779 StartZ=0 EndX=407.073 EndY=48.2206 EndZ=0
    g74: LineSegment StartX=375.073 StartY=48.2206 StartZ=0 EndX=375.073 EndY=-78.7896 EndZ=0
    g75: LineSegment StartX=375.073 StartY=48.2206 StartZ=0 EndX=382.073 EndY=48.2206 EndZ=0
    g76: LineSegment StartX=407.073 StartY=48.2206 StartZ=0 EndX=400.073 EndY=48.2206 EndZ=0
    g77: LineSegment StartX=394.073 StartY=48.2206 StartZ=0 EndX=394.073 EndY=52.2206 EndZ=0
    g78: LineSegment StartX=388.073 StartY=48.2206 StartZ=0 EndX=388.073 EndY=58.2206 EndZ=0
    g79: ArcOfCircle CenterX=385.073 CenterY=61.2206 CenterZ=0 NormalX=0 NormalY=0 NormalZ=1 AngleXU=0 Radius=4.24264 StartAngle=5.49779 EndAngle=10.2102
    g80: ArcOfCircle CenterX=397.073 CenterY=55.2206 CenterZ=0 NormalX=0 NormalY=0 NormalZ=1 AngleXU=0 Radius=4.24264 StartAngle=5.49779 EndAngle=10.2102
    g81: LineSegment StartX=382.073 StartY=58.2206 StartZ=0 EndX=382.073 EndY=48.2206 EndZ=0
    g82: LineSegment StartX=400.073 StartY=52.2206 StartZ=0 EndX=400.073 EndY=48.2206 EndZ=0
    g83: LineSegment StartX=394.073 StartY=48.2206 StartZ=0 EndX=388.073 EndY=48.2206 EndZ=0
    g84: LineSegment StartX=306.073 StartY=-40.8935 StartZ=0 EndX=306.073 EndY=-27.5935 EndZ=0
    g85: LineSegment StartX=318.073 StartY=-27.5935 StartZ=0 EndX=318.073 EndY=-47.4805 EndZ=0
    g86: LineSegment StartX=306.073 StartY=-27.5935 StartZ=0 EndX=310.073 EndY=-27.5935 EndZ=0
    g87: LineSegment StartX=318.073 StartY=-27.5935 StartZ=0 EndX=314.073 EndY=-27.5935 EndZ=0
    g88: LineSegment StartX=310.073 StartY=-27.5935 StartZ=0 EndX=310.073 EndY=-31.5935 EndZ=0
    g89: LineSegment StartX=314.073 StartY=-27.5935 StartZ=0 EndX=314.073 EndY=-31.5935 EndZ=0
    g90: ArcOfCircle CenterX=312.073 CenterY=-33.5935 CenterZ=0 NormalX=0 NormalY=0 NormalZ=1 AngleXU=0 Radius=2.82843 StartAngle=2.35619 EndAngle=7.06858
  constraints (121):
    c: Distance(g44) = 2.41
    c: Block(g44)
    c: Coincident(g46,g44)
    c: Coincident(g49,g36)
    c: Horizontal(g49)
    c: Block(g49)
    c: Coincident(g50,g45)
    c: Block(g50)
    c: Coincident(g51,g6)
    c: Block(g51)
    c: Coincident(g54,g52)
    c: Coincident(g54,g53)
    c: Coincident(g58,g56)
    c: Coincident(g58,g57)
    c: Vertical(g58)
    c: Coincident(g59,g56)
    c: Coincident(g59,g55)
    c: Coincident(g60,g55)
    c: Coincident(g60,g57)
    c: Horizontal(g60)
    c: Block(g61)
    c: Block(g62)
    c: Coincident(g63,g44)
    c: Coincident(g63,g62)
    c: Coincident(g64,g61)
    c: Coincident(g65,g61)
    c: Coincident(g65,g62)
    c: Vertical(g65)
    c: Block(g66)
    c: Coincident(g66,g50)
    c: Coincident(g67,g66)
    c: Coincident(g67,g43)
    c: Horizontal(g67)
    c: Coincident(g68,g51)
    c: Perpendicular(g68,g51)
    c: Coincident(g69,g64)
    c: Coincident(g70,g68)
    c: Distance(g70) = 3
    c: Distance(g71) = 3
    c: Perpendicular(g68,g70)
    c: Coincident(g72,g70)
    c: Coincident(g72,g71)
    c: Block(g72)
    c: Block(g69)
    c: Block(g71)
    c: Block(g54)
    c: Block(g59)
    c: Block(g58)
    c: Block(g60)
    c: Block(g67)
    c: Block(g43)
    c: Block(g36)
    c: Block(g48)
    c: Block(g46)
    c: Block(g47)
    c: Block(g45)
    c: Block(g35)
    c: Block(g34)
    c: Block(g0)
    c: Block(g33)
    c: Block(g52)
    c: Block(g6)
    c: Block(g41)
    c: Block(g57)
    c: Block(g55)
    c: Block(g53)
    c: Block(g68)
    c: Distance(g48) = 2.76
    c: Distance(g47) = 6.6
    c: Distance(g45) = 2.36657
    c: Coincident(g73,g49)
    c: Vertical(g73)
    c: Distance(g73) = 152
    c: Coincident(g74,g53)
    c: Vertical(g74)
    c: Block(g74)
    c: Coincident(g75,g74)
    c: Horizontal(g75)
    c: Distance(g75) = 7
    c: Horizontal(g76)
    c: Distance(g76) = 7
    c: Coincident(g76,g73)
    c: Vertical(g77)
    c: Distance(g77) = 4
    c: Vertical(g78)
    c: Distance(g78) = 10
    c: Coincident(g79,g78)
    c: Coincident(g80,g77)
    c: Block(g80)
    c: Block(g79)
    c: Coincident(g81,g79)
    c: Coincident(g81,g75)
    c: Vertical(g81)
    c: Coincident(g82,g80)
    c: Coincident(g82,g76)
    c: Vertical(g82)
    c: Coincident(g83,g77)
    c: Coincident(g83,g78)
    c: Horizontal(g83)
    c: Coincident(g84,g6)
    c: Vertical(g84)
    c: Distance(g84) = 13.3
    c: Coincident(g85,g52)
    c: Vertical(g85)
    c: Block(g85)
    c: Coincident(g86,g84)
    c: Horizontal(g86)
    c: Distance(g86) = 4
    c: Coincident(g87,g85)
    c: Horizontal(g87)
    c: Distance(g87) = 4
    c: Coincident(g88,g86)
    c: Vertical(g88)
    c: Coincident(g89,g87)
    c: Vertical(g89)
    c: Distance(g88) = 4
    c: Distance(g89) = 4
    c: Coincident(g90,g88)
    c: Coincident(g90,g89)
    c: Block(g90)
    c: Block(g56)
FEATURE [Sketcher::SketchObject] Sketch005  label="middleTop"
  FullyConstrained = true
  sketch-geometry (133):
    g0: Circle CenterX=175.025 CenterY=27.0667 CenterZ=0 NormalX=0 NormalY=0 NormalZ=1 AngleXU=0 Radius=1
    g1: Circle CenterX=179.022 CenterY=24.8665 CenterZ=0 NormalX=0 NormalY=0 NormalZ=1 AngleXU=0 Radius=1
    g2: Circle CenterX=179.022 CenterY=27.0606 CenterZ=0 NormalX=0 NormalY=0 NormalZ=1 AngleXU=0 Radius=1
    g3: BSplineCurve PolesCount=3 KnotsCount=2 Degree=2 IsPeriodic=0
    g4: GeomPoint X=175.025 Y=27.0667 Z=0
    g5: GeomPoint X=179.022 Y=27.0606 Z=0
    g6: Circle CenterX=189.124 CenterY=27.0628 CenterZ=0 NormalX=0 NormalY=0 NormalZ=1 AngleXU=0 Radius=1
    g7: Circle CenterX=185.124 CenterY=24.8665 CenterZ=0 NormalX=0 NormalY=0 NormalZ=1 AngleXU=0 Radius=1
    g8: Circle CenterX=185.124 CenterY=27.0606 CenterZ=0 NormalX=0 NormalY=0 NormalZ=1 AngleXU=0 Radius=1
    g9: BSplineCurve PolesCount=3 KnotsCount=2 Degree=2 IsPeriodic=0
    g10: GeomPoint X=189.124 Y=27.0628 Z=0
    g11: GeomPoint X=185.124 Y=27.0606 Z=0
    g12: Circle CenterX=165.871 CenterY=18.1458 CenterZ=0 NormalX=0 NormalY=0 NormalZ=1 AngleXU=0 Radius=1
    g13: Circle CenterX=169.377 CenterY=16.2206 CenterZ=0 NormalX=0 NormalY=0 NormalZ=1 AngleXU=0 Radius=1
    g14: Circle CenterX=165.871 CenterY=14.2956 CenterZ=0 NormalX=0 NormalY=0 NormalZ=1 AngleXU=0 Radius=1
    g15: BSplineCurve PolesCount=3 KnotsCount=2 Degree=2 IsPeriodic=0
    g16: GeomPoint X=165.871 Y=18.1458 Z=0
    g17: GeomPoint X=165.871 Y=14.2956 Z=0
    g18: Circle CenterX=198.275 CenterY=18.1318 CenterZ=0 NormalX=0 NormalY=0 NormalZ=1 AngleXU=0 Radius=1
    g19: Circle CenterX=194.768 CenterY=16.2206 CenterZ=0 NormalX=0 NormalY=0 NormalZ=1 AngleXU=0 Radius=1
    g20: Circle CenterX=198.264 CenterY=14.2963 CenterZ=0 NormalX=0 NormalY=0 NormalZ=1 AngleXU=0 Radius=1
    g21: BSplineCurve PolesCount=3 KnotsCount=2 Degree=2 IsPeriodic=0
    g22: GeomPoint X=198.275 Y=18.1318 Z=0
    g23: GeomPoint X=198.264 Y=14.2963 Z=0
    g24: Circle CenterX=125.607 CenterY=54.1951 CenterZ=0 NormalX=0 NormalY=0 NormalZ=1 AngleXU=0 Radius=1
    g25: Circle CenterX=139.632 CenterY=46.4944 CenterZ=0 NormalX=0 NormalY=0 NormalZ=1 AngleXU=0 Radius=1
    g26: Circle CenterX=127.326 CenterY=56.7187 CenterZ=0 NormalX=0 NormalY=0 NormalZ=1 AngleXU=0 Radius=1
    g27: BSplineCurve PolesCount=3 KnotsCount=2 Degree=2 IsPeriodic=0
    g28: GeomPoint X=125.607 Y=54.1951 Z=0
    g29: GeomPoint X=127.326 Y=56.7187 Z=0
    g30: Circle CenterX=236.824 CenterY=56.7187 CenterZ=0 NormalX=0 NormalY=0 NormalZ=1 AngleXU=0 Radius=1
    g31: Circle CenterX=224.513 CenterY=46.4944 CenterZ=0 NormalX=0 NormalY=0 NormalZ=1 AngleXU=0 Radius=1
    g32: Circle CenterX=238.538 CenterY=54.1951 CenterZ=0 NormalX=0 NormalY=0 NormalZ=1 AngleXU=0 Radius=1
    g33: BSplineCurve PolesCount=3 KnotsCount=2 Degree=2 IsPeriodic=0
    g34: GeomPoint X=236.824 Y=56.7187 Z=0
    g35: GeomPoint X=238.538 Y=54.1951 Z=0
    g36: Circle CenterX=189.121 CenterY=124.221 CenterZ=0 NormalX=0 NormalY=0 NormalZ=1 AngleXU=0 Radius=1
    g37: Circle CenterX=185.124 CenterY=124.221 CenterZ=0 NormalX=0 NormalY=0 NormalZ=1 AngleXU=0 Radius=1
    g38: Circle CenterX=185.124 CenterY=120.221 CenterZ=0 NormalX=0 NormalY=0 NormalZ=1 AngleXU=0 Radius=1
    g39: BSplineCurve PolesCount=3 KnotsCount=2 Degree=2 IsPeriodic=0
    g40: GeomPoint X=189.121 Y=124.221 Z=0
    g41: GeomPoint X=185.124 Y=120.221 Z=0
    g42: Circle CenterX=175.022 CenterY=124.221 CenterZ=0 NormalX=0 NormalY=0 NormalZ=1 AngleXU=0 Radius=1
    g43: Circle CenterX=179.022 CenterY=124.221 CenterZ=0 NormalX=0 NormalY=0 NormalZ=1 AngleXU=0 Radius=1
    g44: Circle CenterX=179.022 CenterY=120.221 CenterZ=0 NormalX=0 NormalY=0 NormalZ=1 AngleXU=0 Radius=1
    g45: BSplineCurve PolesCount=3 KnotsCount=2 Degree=2 IsPeriodic=0
    g46: GeomPoint X=175.022 Y=124.221 Z=0
    g47: GeomPoint X=179.022 Y=120.221 Z=0
    g48: LineSegment StartX=232.071 StartY=124.221 StartZ=0 EndX=232.071 EndY=127.221 EndZ=0
    g49-g52: Circle x4 (B-spline internal-alignment scaffolding for g53; pole/knot coordinates omitted)
    g53: BSplineCurve PolesCount=5 KnotsCount=3 Degree=3 IsPeriodic=0
    g54: GeomPoint X=232.072 Y=133.221 Z=0
    g55: GeomPoint X=223.072 Y=130.221 Z=0
    g56: GeomPoint X=232.071 Y=127.221 Z=0
    g57-g61: Circle x5 (B-spline internal-alignment scaffolding for g62; pole/knot coordinates omitted)
    g62: BSplineCurve PolesCount=5 KnotsCount=3 Degree=3 IsPeriodic=0
    g63: GeomPoint X=132.072 Y=133.221 Z=0
    g64: GeomPoint X=141.072 Y=130.221 Z=0
    g65: GeomPoint X=132.072 Y=127.221 Z=0
    g66: ArcOfCircle CenterX=247.391 CenterY=52.0843 CenterZ=0 NormalX=0 NormalY=0 NormalZ=1 AngleXU=0 Radius=4.24264 StartAngle=4.42912 EndAngle=9.14151
    g67: LineSegment StartX=240.687 StartY=51.8263 StartZ=0 EndX=239.192 EndY=54.5542 EndZ=0
    g68: LineSegment StartX=243.575 StartY=46.5669 StartZ=0 EndX=245.072 EndY=43.8408 EndZ=0
    g69: LineSegment StartX=240.168 StartY=69.471 StartZ=0 EndX=241.708 EndY=67.6172 EndZ=0
    g70: LineSegment StartX=246.783 StartY=71.8328 StartZ=0 EndX=248.546 EndY=69.7098 EndZ=0
    g71: LineSegment StartX=245.073 StartY=63.5726 StartZ=0 EndX=243.476 EndY=65.4955 EndZ=0
    g72: LineSegment StartX=123.967 StartY=69.4706 StartZ=0 EndX=122.37 EndY=67.5474 EndZ=0
    g73: LineSegment StartX=232.072 StartY=133.221 StartZ=0 EndX=232.072 EndY=136.221 EndZ=0
    g74: LineSegment StartX=232.072 StartY=136.221 StartZ=0 EndX=132.072 EndY=136.221 EndZ=0
    g75: LineSegment StartX=132.072 StartY=136.221 StartZ=0 EndX=132.072 EndY=133.221 EndZ=0
    g76: LineSegment StartX=132.072 StartY=127.221 StartZ=0 EndX=132.072 EndY=124.221 EndZ=0
    g77: LineSegment StartX=132.072 StartY=124.221 StartZ=0 EndX=175.022 EndY=124.221 EndZ=0
    g78: LineSegment StartX=189.121 StartY=124.221 StartZ=0 EndX=232.071 EndY=124.221 EndZ=0
    g79: LineSegment StartX=185.124 StartY=120.221 StartZ=0 EndX=185.124 EndY=27.0606 EndZ=0
    g80: LineSegment StartX=189.124 StartY=27.0628 StartZ=0 EndX=240.168 EndY=69.471 EndZ=0
    g81: LineSegment StartX=241.708 StartY=67.6172 StartZ=0 EndX=246.783 EndY=71.8328 EndZ=0
    g82: LineSegment StartX=248.546 StartY=69.7098 StartZ=0 EndX=243.476 EndY=65.4955 EndZ=0
    g83: LineSegment StartX=245.073 StartY=63.5726 StartZ=0 EndX=236.824 EndY=56.7187 EndZ=0
    g84: LineSegment StartX=238.538 StartY=54.1951 StartZ=0 EndX=239.192 EndY=54.5542 EndZ=0
    g85: LineSegment StartX=240.687 StartY=51.8263 StartZ=0 EndX=243.317 EndY=53.2701 EndZ=0
    g86: LineSegment StartX=246.205 StartY=48.0108 StartZ=0 EndX=243.575 EndY=46.5669 EndZ=0
    g87: LineSegment StartX=245.072 StartY=43.8408 StartZ=0 EndX=198.275 EndY=18.1318 EndZ=0
    g88: LineSegment StartX=165.871 StartY=18.1458 StartZ=0 EndX=118.934 EndY=43.9178 EndZ=0
    g89: LineSegment StartX=118.934 StartY=43.9178 StartZ=0 EndX=120.377 EndY=46.5474 EndZ=0
    g90: LineSegment StartX=117.748 StartY=47.9913 StartZ=0 EndX=120.377 EndY=46.5474 EndZ=0
    g91: LineSegment StartX=120.635 StartY=53.2507 StartZ=0 EndX=123.265 EndY=51.8068 EndZ=0
    g92: LineSegment StartX=123.265 StartY=51.8068 StartZ=0 EndX=124.73 EndY=54.6766 EndZ=0
    g93: ArcOfCircle CenterX=116.562 CenterY=52.0649 CenterZ=0 NormalX=0 NormalY=0 NormalZ=1 AngleXU=0 Radius=4.24264 StartAngle=0.283267 EndAngle=4.99566
    g94: LineSegment StartX=124.73 StartY=54.6766 StartZ=0 EndX=125.607 EndY=54.1951 EndZ=0
    g95: LineSegment StartX=127.326 StartY=56.7187 StartZ=0 EndX=119.072 EndY=63.5741 EndZ=0
    g96: LineSegment StartX=119.072 StartY=63.5741 StartZ=0 EndX=120.669 EndY=65.4973 EndZ=0
    g97: LineSegment StartX=120.669 StartY=65.4973 StartZ=0 EndX=115.591 EndY=69.7147 EndZ=0
    g98: LineSegment StartX=115.591 StartY=69.7147 StartZ=0 EndX=117.293 EndY=71.7641 EndZ=0
    g99: LineSegment StartX=117.293 StartY=71.7641 StartZ=0 EndX=122.37 EndY=67.5474 EndZ=0
    g100: LineSegment StartX=123.967 StartY=69.4706 StartZ=0 EndX=175.025 EndY=27.0667 EndZ=0
    g101: LineSegment StartX=179.022 StartY=27.0606 StartZ=0 EndX=179.022 EndY=120.221 EndZ=0
    g102-g117: Circle x16 (B-spline internal-alignment scaffolding for g118; pole/knot coordinates omitted)
    g118: BSplineCurve PolesCount=16 KnotsCount=14 Degree=3 IsPeriodic=0
    g119-g132: GeomPoint x14 (B-spline internal-alignment scaffolding for g118; pole/knot coordinates omitted)
  constraints (180):
    c: Weight(g0) = 1
    c: Equal(g0,g1)
    c: Equal(g0,g2)
    c: InternalAlignment(g0,g3)
    c: InternalAlignment(g1,g3)
    c: InternalAlignment(g2,g3)
    c: InternalAlignment(g4,g3)
    c: InternalAlignment(g5,g3)
    c: Weight(g6) = 1
    c: Equal(g6,g7)
    c: Equal(g6,g8)
    c: InternalAlignment(g6,g9)
    c: InternalAlignment(g7,g9)
    c: InternalAlignment(g8,g9)
    c: InternalAlignment(g10,g9)
    c: InternalAlignment(g11,g9)
    c: Block(g9)
    c: Block(g3)
    c: Weight(g12) = 1
    c: Equal(g12,g13)
    c: Equal(g12,g14)
    c: InternalAlignment(g12,g15)
    c: InternalAlignment(g13,g15)
    c: InternalAlignment(g14,g15)
    c: InternalAlignment(g16,g15)
    c: InternalAlignment(g17,g15)
    c: Weight(g18) = 1
    c: Equal(g18,g19)
    c: Equal(g18,g20)
    c: InternalAlignment(g18,g21)
    c: InternalAlignment(g19,g21)
    c: InternalAlignment(g20,g21)
    c: InternalAlignment(g22,g21)
    c: InternalAlignment(g23,g21)
    c: Block(g15)
    c: Block(g21)
    c: Weight(g24) = 1
    c: Equal(g24,g25)
    c: Equal(g24,g26)
    c: InternalAlignment(g24,g27)
    c: InternalAlignment(g25,g27)
    c: InternalAlignment(g26,g27)
    c: InternalAlignment(g28,g27)
    c: InternalAlignment(g29,g27)
    c: Block(g27)
    c: Weight(g30) = 1
    c: Equal(g30,g31)
    c: Equal(g30,g32)
    c: InternalAlignment(g30,g33)
    c: InternalAlignment(g31,g33)
    c: InternalAlignment(g32,g33)
    c: InternalAlignment(g34,g33)
    c: InternalAlignment(g35,g33)
    c: Block(g33)
    c: Weight(g36) = 1
    c: Equal(g36,g37)
    c: Equal(g36,g38)
    c: InternalAlignment(g36,g39)
    c: InternalAlignment(g37,g39)
    c: InternalAlignment(g38,g39)
    c: InternalAlignment(g40,g39)
    c: InternalAlignment(g41,g39)
    c: Weight(g42) = 1
    c: Equal(g42,g43)
    c: Equal(g42,g44)
    c: InternalAlignment(g42,g45)
    c: InternalAlignment(g43,g45)
    c: InternalAlignment(g44,g45)
    c: InternalAlignment(g46,g45)
    c: InternalAlignment(g47,g45)
    c: Block(g45)
    c: Block(g39)
    c: Vertical(g48)
    c: Distance(g48) = 3
    c: Weight(g49) = 1
    c: Equal(g49,g50)
    c: Equal(g49,g51)
    c: Equal(g49,g52)
    c: Coincident(g53,g48)
    c: InternalAlignment(g49-g52 -> g53) x4
    c: InternalAlignment(g54,g53)
    c: InternalAlignment(g55,g53)
    c: InternalAlignment(g56,g53)
    c: Weight(g57) = 1
    c: Equal(g57, g58-g61) x4
    c: InternalAlignment(g57-g61 -> g62) x5
    c: InternalAlignment(g63,g62)
    c: InternalAlignment(g64,g62)
    c: InternalAlignment(g65,g62)
    c: Block(g62)
    c: Block(g67)
    c: Block(g68)
    c: Distance(g69) = 2.41
    c: Distance(g70) = 2.76
    c: Distance(g71) = 2.5
    c: Distance(g72) = 2.5
    c: Block(g66)
    c: Block(g48)
    c: Block(g53)
    c: Coincident(g73,g53)
    c: Vertical(g73)
    c: Distance(g73) = 3
    c: Coincident(g74,g73)
    c: Horizontal(g74)
    c: Distance(g74) = 100
    c: Coincident(g75,g74)
    c: Coincident(g75,g62)
    c: Vertical(g75)
    c: Distance(g75) = 3
    c: Coincident(g76,g62)
    c: Vertical(g76)
    c: Distance(g76) = 3
    c: Coincident(g77,g76)
    c: Coincident(g77,g45)
    c: Horizontal(g77)
    c: Distance(g77) = 42.95
    c: Coincident(g78,g39)
    c: Coincident(g78,g48)
    c: Horizontal(g78)
    c: Distance(g78) = 42.95
    c: Coincident(g79,g39)
    c: Coincident(g79,g9)
    c: Vertical(g79)
    c: Distance(g79) = 93.16
    c: Coincident(g80,g9)
    c: Coincident(g80,g69)
    c: Angle(g80) = 0.693245
    c: Block(g80)
    c: Coincident(g81,g69)
    c: Coincident(g81,g70)
    c: Block(g81)
    c: Coincident(g82,g70)
    c: Coincident(g82,g71)
    c: Block(g82)
    c: Coincident(g83,g71)
    c: Coincident(g83,g33)
    c: Block(g71)
    c: Coincident(g84,g33)
    c: Coincident(g84,g67)
    c: Coincident(g85,g67)
    c: Coincident(g85,g66)
    c: Coincident(g86,g66)
    c: Coincident(g86,g68)
    c: Coincident(g87,g68)
    c: Coincident(g87,g21)
    c: Coincident(g88,g15)
    c: Coincident(g89,g88)
    c: Block(g89)
    c: Coincident(g90,g89)
    c: Block(g90)
    c: Block(g91)
    c: Coincident(g92,g91)
    c: Block(g92)
    c: Coincident(g93,g91)
    c: Coincident(g93,g90)
    c: Block(g93)
    c: Coincident(g94,g92)
    c: Coincident(g94,g27)
    c: Coincident(g95,g27)
    c: Block(g95)
    c: Coincident(g96,g95)
    c: Coincident(g97,g96)
    c: Coincident(g98,g97)
    c: Coincident(g99,g98)
    c: Coincident(g99,g72)
    c: Block(g98)
    c: Block(g96)
    c: Block(g72)
    c: Coincident(g100,g72)
    c: Coincident(g100,g3)
    c: Coincident(g101,g3)
    c: Coincident(g101,g45)
    c: Vertical(g101)
    c: Coincident(g118,g21)
    c: Weight(g102) = 1
    c: Equal(g102, g103-g117) x15
    c: Coincident(g118,g15)
    c: InternalAlignment(g102-g117 -> g118) x16
    c: InternalAlignment(g119-g132 -> g118) x14
    c: Block(g118)
FEATURE [Sketcher::SketchObject] Sketch006  label="leftSideTop"
  FullyConstrained = true
  sketch-geometry (99):
    g0: Circle CenterX=61.1495 CenterY=111.695 CenterZ=0 NormalX=0 NormalY=0 NormalZ=1 AngleXU=0 Radius=1
    g1: Circle CenterX=58.0728 CenterY=114.251 CenterZ=0 NormalX=0 NormalY=0 NormalZ=1 AngleXU=0 Radius=1
    g2: Circle CenterX=58.0728 CenterY=110.251 CenterZ=0 NormalX=0 NormalY=0 NormalZ=1 AngleXU=0 Radius=1
    g3: BSplineCurve PolesCount=3 KnotsCount=2 Degree=2 IsPeriodic=0
    g4: GeomPoint X=61.1495 Y=111.695 Z=0
    g5: GeomPoint X=58.0728 Y=110.251 Z=0
    g6: Circle CenterX=61.5791 CenterY=89.3511 CenterZ=0 NormalX=0 NormalY=0 NormalZ=1 AngleXU=0 Radius=1
    g7: Circle CenterX=58.0728 CenterY=91.2763 CenterZ=0 NormalX=0 NormalY=0 NormalZ=1 AngleXU=0 Radius=1
    g8: Circle CenterX=58.0728 CenterY=95.2763 CenterZ=0 NormalX=0 NormalY=0 NormalZ=1 AngleXU=0 Radius=1
    g9: BSplineCurve PolesCount=3 KnotsCount=2 Degree=2 IsPeriodic=0
    g10: GeomPoint X=61.5791 Y=89.3511 Z=0
    g11: GeomPoint X=58.0728 Y=95.2763 Z=0
    g12: Circle CenterX=62.0728 CenterY=124.221 CenterZ=0 NormalX=0 NormalY=0 NormalZ=1 AngleXU=0 Radius=1
    g13: Circle CenterX=58.0728 CenterY=124.221 CenterZ=0 NormalX=0 NormalY=0 NormalZ=1 AngleXU=0 Radius=1
    g14: Circle CenterX=61.1496 CenterY=121.665 CenterZ=0 NormalX=0 NormalY=0 NormalZ=1 AngleXU=0 Radius=1
    g15: BSplineCurve PolesCount=3 KnotsCount=2 Degree=2 IsPeriodic=0
    g16: GeomPoint X=62.0728 Y=124.221 Z=0
    g17: GeomPoint X=61.1496 Y=121.665 Z=0
    g18: Circle CenterX=61.5791 CenterY=75.4095 CenterZ=0 NormalX=0 NormalY=0 NormalZ=1 AngleXU=0 Radius=1
    g19: Circle CenterX=58.0728 CenterY=77.3346 CenterZ=0 NormalX=0 NormalY=0 NormalZ=1 AngleXU=0 Radius=1
    g20: Circle CenterX=58.0728 CenterY=73.3346 CenterZ=0 NormalX=0 NormalY=0 NormalZ=1 AngleXU=0 Radius=1
    g21: BSplineCurve PolesCount=3 KnotsCount=2 Degree=2 IsPeriodic=0
    g22: GeomPoint X=61.5791 Y=75.4095 Z=0
    g23: GeomPoint X=58.0728 Y=73.3346 Z=0
    g24: Circle CenterX=2.07281 CenterY=124.221 CenterZ=0 NormalX=0 NormalY=0 NormalZ=1 AngleXU=0 Radius=1
    g25: Circle CenterX=1.57905 CenterY=122.295 CenterZ=0 NormalX=0 NormalY=0 NormalZ=1 AngleXU=0 Radius=1
    g26: BSplineCurve PolesCount=3 KnotsCount=2 Degree=2 IsPeriodic=0
    g27: GeomPoint X=2.07281 Y=124.221 Z=0
    g28: GeomPoint X=1.57905 Y=122.295 Z=0
    g29: Circle CenterX=46.0728 CenterY=124.221 CenterZ=0 NormalX=0 NormalY=0 NormalZ=1 AngleXU=0 Radius=1
    g30: Circle CenterX=46.0728 CenterY=120.221 CenterZ=0 NormalX=0 NormalY=0 NormalZ=1 AngleXU=0 Radius=1
    g31: BSplineCurve PolesCount=3 KnotsCount=2 Degree=2 IsPeriodic=0
    g32: GeomPoint X=42.0728 Y=124.221 Z=0
    g33: GeomPoint X=46.0728 Y=120.221 Z=0
    g34: Circle CenterX=46.0728 CenterY=109.865 CenterZ=0 NormalX=0 NormalY=0 NormalZ=1 AngleXU=0 Radius=1
    g35: Circle CenterX=46.0728 CenterY=105.865 CenterZ=0 NormalX=0 NormalY=0 NormalZ=1 AngleXU=0 Radius=1
    g36: Circle CenterX=42.0728 CenterY=105.865 CenterZ=0 NormalX=0 NormalY=0 NormalZ=1 AngleXU=0 Radius=1
    g37: BSplineCurve PolesCount=3 KnotsCount=2 Degree=2 IsPeriodic=0
    g38: GeomPoint X=46.0728 Y=109.865 Z=0
    g39: GeomPoint X=42.0728 Y=105.865 Z=0
    g40: Circle CenterX=35.5028 CenterY=105.865 CenterZ=0 NormalX=0 NormalY=0 NormalZ=1 AngleXU=0 Radius=1
    g41: Circle CenterX=31.5028 CenterY=105.865 CenterZ=0 NormalX=0 NormalY=0 NormalZ=1 AngleXU=0 Radius=1
    g42: Circle CenterX=27.9965 CenterY=107.79 CenterZ=0 NormalX=0 NormalY=0 NormalZ=1 AngleXU=0 Radius=1
    g43: BSplineCurve PolesCount=3 KnotsCount=2 Degree=2 IsPeriodic=0
    g44: GeomPoint X=35.5028 Y=105.865 Z=0
    g45: GeomPoint X=27.9965 Y=107.79 Z=0
    g46-g50: Circle x5 (B-spline internal-alignment scaffolding for g51; pole/knot coordinates omitted)
    g51: BSplineCurve PolesCount=5 KnotsCount=3 Degree=3 IsPeriodic=0
    g52: GeomPoint X=132.072 Y=133.221 Z=0
    g53: GeomPoint X=141.072 Y=130.221 Z=0
    g54: GeomPoint X=132.072 Y=127.221 Z=0
    g55: ArcOfCircle CenterX=116.562 CenterY=52.0649 CenterZ=0 NormalX=0 NormalY=0 NormalZ=1 AngleXU=0 Radius=4.24264 StartAngle=0.283268 EndAngle=4.99566
    g56: LineSegment StartX=123.967 StartY=69.4706 StartZ=0 EndX=122.37 EndY=67.5474 EndZ=0
    g57: LineSegment StartX=117.293 StartY=71.7641 StartZ=0 EndX=115.591 EndY=69.7147 EndZ=0
    g58: LineSegment StartX=120.669 StartY=65.4973 StartZ=0 EndX=119.072 EndY=63.5741 EndZ=0
    g59: LineSegment StartX=124.73 StartY=54.6766 StartZ=0 EndX=123.265 EndY=51.8068 EndZ=0
    g60: LineSegment StartX=120.377 StartY=46.5474 StartZ=0 EndX=118.934 EndY=43.9178 EndZ=0
    g61: BSplineCurve PolesCount=3 KnotsCount=2 Degree=2 IsPeriodic=0
    g62: BSplineCurve PolesCount=3 KnotsCount=2 Degree=2 IsPeriodic=0
    g63: LineSegment StartX=61.5791 StartY=75.4095 StartZ=0 EndX=118.934 EndY=43.9178 EndZ=0
    g64: LineSegment StartX=117.748 StartY=47.9913 StartZ=0 EndX=120.377 EndY=46.5474 EndZ=0
    g65: LineSegment StartX=120.635 StartY=53.2507 StartZ=0 EndX=123.265 EndY=51.8068 EndZ=0
    g66: LineSegment StartX=124.73 StartY=54.6766 StartZ=0 EndX=61.5791 EndY=89.3511 EndZ=0
    g67: LineSegment StartX=58.0728 StartY=95.2763 StartZ=0 EndX=58.0728 EndY=110.251 EndZ=0
    g68: LineSegment StartX=61.1495 StartY=111.695 StartZ=0 EndX=119.072 EndY=63.5741 EndZ=0
    g69: LineSegment StartX=120.669 StartY=65.4973 StartZ=0 EndX=115.591 EndY=69.7147 EndZ=0
    g70: LineSegment StartX=117.293 StartY=71.7641 StartZ=0 EndX=122.37 EndY=67.5474 EndZ=0
    g71: LineSegment StartX=123.967 StartY=69.4706 StartZ=0 EndX=61.1496 EndY=121.665 EndZ=0
    g72: LineSegment StartX=62.0728 StartY=124.221 StartZ=0 EndX=132.072 EndY=124.221 EndZ=0
    g73: LineSegment StartX=132.072 StartY=127.221 StartZ=0 EndX=132.072 EndY=124.221 EndZ=0
    g74: LineSegment StartX=132.072 StartY=133.221 StartZ=0 EndX=132.072 EndY=136.221 EndZ=0
    g75: LineSegment StartX=132.072 StartY=136.221 StartZ=0 EndX=-42.9272 EndY=136.221 EndZ=0
    g76: LineSegment StartX=2.07281 StartY=124.221 StartZ=0 EndX=42.0728 EndY=124.221 EndZ=0
    g77: LineSegment StartX=46.0728 StartY=120.221 StartZ=0 EndX=46.0728 EndY=109.865 EndZ=0
    g78: LineSegment StartX=42.0728 StartY=105.865 StartZ=0 EndX=35.5028 EndY=105.865 EndZ=0
    g79: LineSegment StartX=27.9965 StartY=107.79 StartZ=0 EndX=1.57905 EndY=122.295 EndZ=0
    g80: LineSegment StartX=-6.92718 StartY=76.4095 StartZ=0 EndX=42.0728 EndY=76.4095 EndZ=0
    g81: LineSegment StartX=-17.9272 StartY=48.2206 StartZ=0 EndX=-17.9272 EndY=58.2206 EndZ=0
    g82: LineSegment StartX=-35.9272 StartY=48.2206 StartZ=0 EndX=-35.9272 EndY=52.2206 EndZ=0
    g83: LineSegment StartX=-29.9272 StartY=48.2206 StartZ=0 EndX=-29.9272 EndY=52.2206 EndZ=0
    g84: LineSegment StartX=-23.9272 StartY=48.2206 StartZ=0 EndX=-23.9272 EndY=58.2206 EndZ=0
    g85: ArcOfCircle CenterX=-32.9272 CenterY=55.2206 CenterZ=0 NormalX=0 NormalY=0 NormalZ=1 AngleXU=0 Radius=4.24264 StartAngle=5.49779 EndAngle=10.2102
    g86: ArcOfCircle CenterX=-20.9272 CenterY=61.2206 CenterZ=0 NormalX=0 NormalY=0 NormalZ=1 AngleXU=0 Radius=4.24264 StartAngle=5.49779 EndAngle=10.2102
    g87: LineSegment StartX=-10.9272 StartY=48.2206 StartZ=0 EndX=-10.9272 EndY=72.4095 EndZ=0
    g88: LineSegment StartX=-42.9272 StartY=48.2206 StartZ=0 EndX=-42.9272 EndY=136.221 EndZ=0
    g89: LineSegment StartX=46.0728 StartY=72.4095 StartZ=0 EndX=46.0728 EndY=-27.5905 EndZ=0
    g90: LineSegment StartX=58.0728 StartY=-27.5905 StartZ=0 EndX=58.0728 EndY=73.3346 EndZ=0
    g91: LineSegment StartX=50.0728 StartY=-27.5905 StartZ=0 EndX=50.0728 EndY=-31.5905 EndZ=0
    g92: LineSegment StartX=54.0728 StartY=-27.5905 StartZ=0 EndX=54.0728 EndY=-31.5905 EndZ=0
    g93: ArcOfCircle CenterX=52.0728 CenterY=-33.5905 CenterZ=0 NormalX=0 NormalY=0 NormalZ=1 AngleXU=0 Radius=2.82843 StartAngle=2.35619 EndAngle=7.06858
    g94: LineSegment StartX=46.0728 StartY=-27.5905 StartZ=0 EndX=50.0728 EndY=-27.5905 EndZ=0
    g95: LineSegment StartX=54.0728 StartY=-27.5905 StartZ=0 EndX=58.0728 EndY=-27.5905 EndZ=0
    g96: LineSegment StartX=-17.9272 StartY=48.2206 StartZ=0 EndX=-10.9272 EndY=48.2206 EndZ=0
    g97: LineSegment StartX=-29.9272 StartY=48.2206 StartZ=0 EndX=-23.9272 EndY=48.2206 EndZ=0
    g98: LineSegment StartX=-42.9272 StartY=48.2206 StartZ=0 EndX=-35.9272 EndY=48.2206 EndZ=0
  constraints (172):
    c: Weight(g0) = 1
    c: Equal(g0,g1)
    c: Equal(g0,g2)
    c: InternalAlignment(g0,g3)
    c: InternalAlignment(g1,g3)
    c: InternalAlignment(g2,g3)
    c: InternalAlignment(g4,g3)
    c: InternalAlignment(g5,g3)
    c: Weight(g6) = 1
    c: Equal(g6,g7)
    c: Equal(g6,g8)
    c: InternalAlignment(g6,g9)
    c: InternalAlignment(g7,g9)
    c: InternalAlignment(g8,g9)
    c: InternalAlignment(g10,g9)
    c: InternalAlignment(g11,g9)
    c: Block(g3)
    c: Block(g9)
    c: Weight(g12) = 1
    c: Equal(g12,g13)
    c: Equal(g12,g14)
    c: InternalAlignment(g12,g15)
    c: InternalAlignment(g13,g15)
    c: InternalAlignment(g14,g15)
    c: InternalAlignment(g16,g15)
    c: InternalAlignment(g17,g15)
    c: Block(g15)
    c: Weight(g18) = 1
    c: Equal(g18,g19)
    c: Equal(g18,g20)
    c: InternalAlignment(g18,g21)
    c: InternalAlignment(g19,g21)
    c: InternalAlignment(g20,g21)
    c: InternalAlignment(g22,g21)
    c: InternalAlignment(g23,g21)
    c: Block(g21)
    c: Weight(g24) = 1
    c: Equal(g24,g25)
    c: InternalAlignment(g24,g26)
    c: InternalAlignment(g25,g26)
    c: InternalAlignment(g27,g26)
    c: InternalAlignment(g28,g26)
    c: InternalAlignment(g29,g31)
    c: InternalAlignment(g30,g31)
    c: InternalAlignment(g32,g31)
    c: InternalAlignment(g33,g31)
    c: Weight(g34) = 1
    c: Equal(g34,g35)
    c: Equal(g34,g36)
    c: InternalAlignment(g34,g37)
    c: InternalAlignment(g35,g37)
    c: InternalAlignment(g36,g37)
    c: InternalAlignment(g38,g37)
    c: InternalAlignment(g39,g37)
    c: Equal(g40,g41)
    c: Equal(g40,g42)
    c: InternalAlignment(g40,g43)
    c: InternalAlignment(g41,g43)
    c: InternalAlignment(g42,g43)
    c: InternalAlignment(g44,g43)
    c: InternalAlignment(g45,g43)
    c: Block(g31)
    c: Block(g37)
    c: Block(g43)
    c: Block(g26)
    c: Weight(g46) = 1
    c: Equal(g46, g47-g50) x4
    c: InternalAlignment(g46-g50 -> g51) x5
    c: InternalAlignment(g52,g51)
    c: InternalAlignment(g53,g51)
    c: InternalAlignment(g54,g51)
    c: Block(g51)
    c: Block(g55)
    c: Block(g56)
    c: Block(g57)
    c: Block(g58)
    c: Block(g59)
    c: Block(g60)
    c: Block(g61)
    c: Block(g62)
    c: Coincident(g90,g21)
    c: Coincident(g63,g21)
    c: Coincident(g63,g60)
    c: Coincident(g64,g55)
    c: Coincident(g64,g60)
    c: Coincident(g65,g55)
    c: Coincident(g65,g59)
    c: Coincident(g66,g59)
    c: Coincident(g66,g9)
    c: Coincident(g67,g9)
    c: Coincident(g67,g3)
    c: Vertical(g67)
    c: Coincident(g68,g3)
    c: Coincident(g68,g58)
    c: Coincident(g69,g58)
    c: Coincident(g69,g57)
    c: Coincident(g70,g57)
    c: Coincident(g70,g56)
    c: Coincident(g71,g56)
    c: Coincident(g71,g15)
    c: Coincident(g72,g15)
    c: Horizontal(g72)
    c: Coincident(g73,g51)
    c: Coincident(g73,g72)
    c: Vertical(g73)
    c: Coincident(g74,g51)
    c: Vertical(g74)
    c: Coincident(g75,g74)
    c: Horizontal(g75)
    c: Coincident(g76,g26)
    c: Coincident(g76,g31)
    c: Horizontal(g76)
    c: Coincident(g77,g31)
    c: Coincident(g77,g37)
    c: Vertical(g77)
    c: Coincident(g78,g37)
    c: Coincident(g78,g43)
    c: Horizontal(g78)
    c: Coincident(g79,g43)
    c: Coincident(g79,g26)
    c: Coincident(g80,g62)
    c: Coincident(g80,g61)
    c: Horizontal(g80)
    c: Vertical(g81)
    c: Distance(g81) = 10
    c: Vertical(g82)
    c: Distance(g82) = 4
    c: Vertical(g83)
    c: Distance(g83) = 4
    c: Vertical(g84)
    c: Distance(g84) = 10
    c: Coincident(g85,g83)
    c: Coincident(g85,g82)
    c: Block(g85)
    c: Coincident(g86,g84)
    c: Coincident(g86,g81)
    c: Block(g86)
    c: Coincident(g87,g62)
    c: Vertical(g87)
    c: Coincident(g88,g75)
    c: Vertical(g88)
    c: Block(g75)
    c: Coincident(g89,g61)
    c: Vertical(g89)
    c: Distance(g89) = 100
    c: Block(g90)
    c: Vertical(g91)
    c: Distance(g91) = 4
    c: Vertical(g92)
    c: Distance(g92) = 4
    c: Coincident(g93,g91)
    c: Coincident(g93,g92)
    c: Block(g93)
    c: Coincident(g94,g89)
    c: Coincident(g94,g91)
    c: Horizontal(g94)
    c: Distance(g94) = 4
    c: Coincident(g95,g92)
    c: Coincident(g95,g90)
    c: Horizontal(g95)
    c: Distance(g95) = 4
    c: Block(g87)
    c: Block(g88)
    c: Coincident(g96,g81)
    c: Coincident(g96,g87)
    c: Horizontal(g96)
    c: Coincident(g97,g83)
    c: Coincident(g97,g84)
    c: Horizontal(g97)
    c: Coincident(g98,g88)
    c: Coincident(g98,g82)
    c: Horizontal(g98)
FEATURE [Sketcher::SketchObject] Sketch007  label="leftSideBottom"
  FullyConstrained = true
  sketch-geometry (92):
    g0: ArcOfCircle CenterX=-26.9272 CenterY=-83.7794 CenterZ=0 NormalX=0 NormalY=0 NormalZ=1 AngleXU=0 Radius=8 StartAngle=3.14159 EndAngle=6.28319
    g1: Circle CenterX=61.5791 CenterY=-56.9099 CenterZ=0 NormalX=0 NormalY=0 NormalZ=1 AngleXU=0 Radius=1
    g2: Circle CenterX=58.0728 CenterY=-58.8351 CenterZ=0 NormalX=0 NormalY=0 NormalZ=1 AngleXU=0 Radius=1
    g3: Circle CenterX=58.0728 CenterY=-62.8351 CenterZ=0 NormalX=0 NormalY=0 NormalZ=1 AngleXU=0 Radius=1
    g4: BSplineCurve PolesCount=3 KnotsCount=2 Degree=2 IsPeriodic=0
    g5: GeomPoint X=61.5791 Y=-56.9099 Z=0
    g6: GeomPoint X=58.0728 Y=-62.8351 Z=0
    g7: Circle CenterX=58.0728 CenterY=-77.8102 CenterZ=0 NormalX=0 NormalY=0 NormalZ=1 AngleXU=0 Radius=1
    g8: Circle CenterX=58.0728 CenterY=-81.8102 CenterZ=0 NormalX=0 NormalY=0 NormalZ=1 AngleXU=0 Radius=1
    g9: Circle CenterX=61.1496 CenterY=-79.2541 CenterZ=0 NormalX=0 NormalY=0 NormalZ=1 AngleXU=0 Radius=1
    g10: BSplineCurve PolesCount=3 KnotsCount=2 Degree=2 IsPeriodic=0
    g11: GeomPoint X=58.0728 Y=-77.8102 Z=0
    g12: GeomPoint X=61.1496 Y=-79.2541 Z=0
    g13: Circle CenterX=61.6457 CenterY=-88.8112 CenterZ=0 NormalX=0 NormalY=0 NormalZ=1 AngleXU=0 Radius=1
    g14: Circle CenterX=58.0728 CenterY=-91.7794 CenterZ=0 NormalX=0 NormalY=0 NormalZ=1 AngleXU=0 Radius=1
    g15: Circle CenterX=63.9135 CenterY=-91.8014 CenterZ=0 NormalX=0 NormalY=0 NormalZ=1 AngleXU=0 Radius=1
    g16: BSplineCurve PolesCount=3 KnotsCount=2 Degree=2 IsPeriodic=0
    g17: GeomPoint X=61.6457 Y=-88.8112 Z=0
    g18: GeomPoint X=63.9135 Y=-91.8014 Z=0
    g19: Circle CenterX=58.0728 CenterY=-40.8935 CenterZ=0 NormalX=0 NormalY=0 NormalZ=1 AngleXU=0 Radius=1
    g20: Circle CenterX=58.0728 CenterY=-44.8935 CenterZ=0 NormalX=0 NormalY=0 NormalZ=1 AngleXU=0 Radius=1
    g21: Circle CenterX=61.5791 CenterY=-42.9683 CenterZ=0 NormalX=0 NormalY=0 NormalZ=1 AngleXU=0 Radius=1
    g22: BSplineCurve PolesCount=3 KnotsCount=2 Degree=2 IsPeriodic=0
    g23: GeomPoint X=58.0728 Y=-40.8935 Z=0
    g24: GeomPoint X=61.5791 Y=-42.9683 Z=0
    g25: Circle CenterX=42.5666 CenterY=-67.3492 CenterZ=0 NormalX=0 NormalY=0 NormalZ=1 AngleXU=0 Radius=1
    g26: Circle CenterX=46.0728 CenterY=-65.424 CenterZ=0 NormalX=0 NormalY=0 NormalZ=1 AngleXU=0 Radius=1
    g27: Circle CenterX=46.0728 CenterY=-69.424 CenterZ=0 NormalX=0 NormalY=0 NormalZ=1 AngleXU=0 Radius=1
    g28: BSplineCurve PolesCount=3 KnotsCount=2 Degree=2 IsPeriodic=0
    g29: GeomPoint X=42.5666 Y=-67.3492 Z=0
    g30: GeomPoint X=46.0728 Y=-69.424 Z=0
    g31: Circle CenterX=2.07281 CenterY=-91.7794 CenterZ=0 NormalX=0 NormalY=0 NormalZ=1 AngleXU=0 Radius=1
    g32: Circle CenterX=-1.92719 CenterY=-91.7794 CenterZ=0 NormalX=0 NormalY=0 NormalZ=1 AngleXU=0 Radius=1
    g33: Circle CenterX=1.57905 CenterY=-89.8542 CenterZ=0 NormalX=0 NormalY=0 NormalZ=1 AngleXU=0 Radius=1
    g34: BSplineCurve PolesCount=3 KnotsCount=2 Degree=2 IsPeriodic=0
    g35: GeomPoint X=2.07281 Y=-91.7794 Z=0
    g36: GeomPoint X=1.57905 Y=-89.8542 Z=0
    g37: ArcOfCircle CenterX=-26.9272 CenterY=22.1087 CenterZ=0 NormalX=0 NormalY=0 NormalZ=1 AngleXU=0 Radius=4 StartAngle=5e-16 EndAngle=3.14159
    g38: Circle CenterX=-10.9272 CenterY=-78.7794 CenterZ=0 NormalX=0 NormalY=0 NormalZ=1 AngleXU=0 Radius=1
    g39: Circle CenterX=-10.9272 CenterY=-82.7794 CenterZ=0 NormalX=0 NormalY=0 NormalZ=1 AngleXU=0 Radius=1
    g40: Circle CenterX=-7.42095 CenterY=-80.8542 CenterZ=0 NormalX=0 NormalY=0 NormalZ=1 AngleXU=0 Radius=1
    g41: BSplineCurve PolesCount=3 KnotsCount=2 Degree=2 IsPeriodic=0
    g42: GeomPoint X=-10.9272 Y=-78.7794 Z=0
    g43: GeomPoint X=-7.42095 Y=-80.8542 Z=0
    g44: BSplineCurve PolesCount=3 KnotsCount=2 Degree=2 IsPeriodic=0
    g45: GeomPoint X=42.5666 Y=-53.4075 Z=0
    g46: GeomPoint X=46.0728 Y=-47.4823 Z=0
    g47: BSplineCurve PolesCount=5 KnotsCount=3 Degree=3 IsPeriodic=0
    g48: LineSegment StartX=124.814 StartY=-22.1885 StartZ=0 EndX=123.265 EndY=-19.3655 EndZ=0
    g49: ArcOfCircle CenterX=116.562 CenterY=-19.6236 CenterZ=0 NormalX=0 NormalY=0 NormalZ=1 AngleXU=0 Radius=4.24264 StartAngle=1.28753 EndAngle=6.00037
    g50: LineSegment StartX=-30.9272 StartY=22.1087 StartZ=0 EndX=-34.9272 EndY=-83.7794 EndZ=0
    g51: LineSegment StartX=-22.9272 StartY=22.1087 StartZ=0 EndX=-18.9272 EndY=-83.7794 EndZ=0
    g52: LineSegment StartX=118.934 StartY=-11.4765 StartZ=0 EndX=120.377 EndY=-14.1062 EndZ=0
    g53: LineSegment StartX=118.86 StartY=-31.3104 StartZ=0 EndX=120.377 EndY=-33.1447 EndZ=0
    g54: LineSegment StartX=115.291 StartY=-37.3514 StartZ=0 EndX=117.05 EndY=-39.4781 EndZ=0
    g55: LineSegment StartX=122.136 StartY=-35.2714 StartZ=0 EndX=123.656 EndY=-37.1092 EndZ=0
    g56: BSplineCurve PolesCount=3 KnotsCount=2 Degree=2 IsPeriodic=0
    g57: LineSegment StartX=132.072 StartY=-100.779 StartZ=0 EndX=132.072 EndY=-103.779 EndZ=0
    g58: LineSegment StartX=132.072 StartY=-91.8014 StartZ=0 EndX=132.072 EndY=-94.7791 EndZ=0
    g59: LineSegment StartX=63.9135 StartY=-91.8014 StartZ=0 EndX=132.072 EndY=-91.8014 EndZ=0
    g60: LineSegment StartX=61.6457 StartY=-88.8112 StartZ=0 EndX=123.656 EndY=-37.1092 EndZ=0
    g61: LineSegment StartX=122.136 StartY=-35.2714 StartZ=0 EndX=117.05 EndY=-39.4781 EndZ=0
    g62: LineSegment StartX=115.291 StartY=-37.3514 StartZ=0 EndX=120.377 EndY=-33.1447 EndZ=0
    g63: LineSegment StartX=118.86 StartY=-31.3104 StartZ=0 EndX=61.1496 EndY=-79.2541 EndZ=0
    g64: LineSegment StartX=58.0728 StartY=-77.8102 StartZ=0 EndX=58.0728 EndY=-62.8351 EndZ=0
    g65: LineSegment StartX=61.5791 StartY=-56.9099 StartZ=0 EndX=124.814 EndY=-22.1885 EndZ=0
    g66: LineSegment StartX=120.636 StartY=-20.8076 StartZ=0 EndX=123.265 EndY=-19.3655 EndZ=0
    g67: LineSegment StartX=117.748 StartY=-15.55 StartZ=0 EndX=120.377 EndY=-14.1062 EndZ=0
    g68: LineSegment StartX=118.934 StartY=-11.4765 StartZ=0 EndX=61.5791 EndY=-42.9683 EndZ=0
    g69: LineSegment StartX=-42.9272 StartY=-103.779 StartZ=0 EndX=132.072 EndY=-103.779 EndZ=0
    g70: LineSegment StartX=42.5666 StartY=-53.4075 StartZ=0 EndX=-7.42095 EndY=-80.8542 EndZ=0
    g71: LineSegment StartX=-10.9272 StartY=-78.7794 StartZ=0 EndX=-10.9272 EndY=48.2206 EndZ=0
    g72: LineSegment StartX=2.07281 StartY=-91.7794 StartZ=0 EndX=42.0728 EndY=-91.7794 EndZ=0
    g73: LineSegment StartX=46.0728 StartY=-87.7794 StartZ=0 EndX=46.0728 EndY=-69.424 EndZ=0
    g74: LineSegment StartX=42.5666 StartY=-67.3492 StartZ=0 EndX=1.57905 EndY=-89.8542 EndZ=0
    g75: LineSegment StartX=-42.9272 StartY=-103.779 StartZ=0 EndX=-42.9272 EndY=48.2206 EndZ=0
    g76: LineSegment StartX=-17.9272 StartY=48.2206 StartZ=0 EndX=-17.9272 EndY=58.2206 EndZ=0
    g77: LineSegment StartX=-35.9272 StartY=48.2206 StartZ=0 EndX=-35.9272 EndY=52.2206 EndZ=0
    g78: LineSegment StartX=-29.9272 StartY=48.2206 StartZ=0 EndX=-29.9272 EndY=52.2206 EndZ=0
    g79: LineSegment StartX=-23.9272 StartY=48.2206 StartZ=0 EndX=-23.9272 EndY=58.2206 EndZ=0
    g80: ArcOfCircle CenterX=-32.9272 CenterY=55.2206 CenterZ=0 NormalX=0 NormalY=0 NormalZ=1 AngleXU=0 Radius=4.24264 StartAngle=5.49779 EndAngle=10.2102
    g81: ArcOfCircle CenterX=-20.9272 CenterY=61.2206 CenterZ=0 NormalX=0 NormalY=0 NormalZ=1 AngleXU=0 Radius=4.24264 StartAngle=5.49779 EndAngle=10.2102
    g82: LineSegment StartX=-17.9272 StartY=48.2206 StartZ=0 EndX=-10.9272 EndY=48.2206 EndZ=0
    g83: LineSegment StartX=-42.9272 StartY=48.2206 StartZ=0 EndX=-35.9272 EndY=48.2206 EndZ=0
    g84: LineSegment StartX=50.0728 StartY=-27.5905 StartZ=0 EndX=50.0728 EndY=-31.5905 EndZ=0
    g85: LineSegment StartX=54.0728 StartY=-27.5905 StartZ=0 EndX=54.0728 EndY=-31.5905 EndZ=0
    g86: ArcOfCircle CenterX=52.0728 CenterY=-33.5905 CenterZ=0 NormalX=0 NormalY=0 NormalZ=1 AngleXU=0 Radius=2.82843 StartAngle=2.35619 EndAngle=7.06858
    g87: LineSegment StartX=46.0728 StartY=-27.5905 StartZ=0 EndX=50.0728 EndY=-27.5905 EndZ=0
    g88: LineSegment StartX=54.0728 StartY=-27.5905 StartZ=0 EndX=58.0728 EndY=-27.5905 EndZ=0
    g89: LineSegment StartX=46.0728 StartY=-27.5905 StartZ=0 EndX=46.0728 EndY=-47.4823 EndZ=0
    g90: LineSegment StartX=58.0728 StartY=-27.5905 StartZ=0 EndX=58.0728 EndY=-40.8935 EndZ=0
    g91: LineSegment StartX=-29.9272 StartY=48.2206 StartZ=0 EndX=-23.9272 EndY=48.2206 EndZ=0
  constraints (170):
    c: Weight(g1) = 1
    c: Equal(g1,g2)
    c: Equal(g1,g3)
    c: InternalAlignment(g1,g4)
    c: InternalAlignment(g2,g4)
    c: InternalAlignment(g3,g4)
    c: InternalAlignment(g5,g4)
    c: InternalAlignment(g6,g4)
    c: Weight(g7) = 1
    c: Equal(g7,g8)
    c: Equal(g7,g9)
    c: InternalAlignment(g7,g10)
    c: InternalAlignment(g8,g10)
    c: InternalAlignment(g9,g10)
    c: InternalAlignment(g11,g10)
    c: InternalAlignment(g12,g10)
    c: Block(g4)
    c: Block(g10)
    c: Weight(g13) = 1
    c: Equal(g13,g14)
    c: Equal(g13,g15)
    c: InternalAlignment(g13,g16)
    c: InternalAlignment(g14,g16)
    c: InternalAlignment(g15,g16)
    c: InternalAlignment(g17,g16)
    c: InternalAlignment(g18,g16)
    c: Block(g16)
    c: Weight(g19) = 1
    c: Equal(g19,g20)
    c: Equal(g19,g21)
    c: InternalAlignment(g19,g22)
    c: InternalAlignment(g20,g22)
    c: InternalAlignment(g21,g22)
    c: InternalAlignment(g23,g22)
    c: InternalAlignment(g24,g22)
    c: Block(g22)
    c: Weight(g25) = 1
    c: Equal(g25,g26)
    c: Equal(g25,g27)
    c: InternalAlignment(g25,g28)
    c: InternalAlignment(g26,g28)
    c: InternalAlignment(g27,g28)
    c: InternalAlignment(g29,g28)
    c: InternalAlignment(g30,g28)
    c: Weight(g31) = 1
    c: Equal(g31,g32)
    c: Equal(g31,g33)
    c: InternalAlignment(g31,g34)
    c: InternalAlignment(g32,g34)
    c: InternalAlignment(g33,g34)
    c: InternalAlignment(g35,g34)
    c: InternalAlignment(g36,g34)
    c: Block(g34)
    c: Block(g28)
    c: Block(g37)
    c: Block(g0)
    c: Weight(g38) = 1
    c: Equal(g38,g40)
    c: InternalAlignment(g38,g41)
    c: InternalAlignment(g39,g41)
    c: InternalAlignment(g40,g41)
    c: InternalAlignment(g42,g41)
    c: InternalAlignment(g43,g41)
    c: InternalAlignment(g45,g44)
    c: InternalAlignment(g46,g44)
    c: Block(g47)
    c: Block(g44)
    c: Block(g41)
    c: Block(g48)
    c: Block(g49)
    c: Coincident(g50,g37)
    c: Coincident(g50,g0)
    c: Coincident(g51,g37)
    c: Coincident(g51,g0)
    c: Block(g51)
    c: Block(g50)
    c: Block(g52)
    c: Block(g53)
    c: Block(g54)
    c: Block(g55)
    c: Block(g56)
    c: Coincident(g57,g47)
    c: Vertical(g57)
    c: Coincident(g58,g47)
    c: Vertical(g58)
    c: Coincident(g59,g16)
    c: Coincident(g59,g58)
    c: Horizontal(g59)
    c: Coincident(g60,g16)
    c: Coincident(g60,g55)
    c: Coincident(g61,g55)
    c: Coincident(g61,g54)
    c: Coincident(g62,g54)
    c: Coincident(g62,g53)
    c: Coincident(g63,g53)
    c: Coincident(g63,g10)
    c: Coincident(g64,g10)
    c: Coincident(g64,g4)
    c: Vertical(g64)
    c: Coincident(g65,g4)
    c: Coincident(g65,g48)
    c: Coincident(g66,g49)
    c: Coincident(g66,g48)
    c: Coincident(g67,g49)
    c: Coincident(g67,g52)
    c: Coincident(g68,g52)
    c: Coincident(g68,g22)
    c: Coincident(g69,g57)
    c: Horizontal(g69)
    c: Coincident(g70,g44)
    c: Coincident(g70,g41)
    c: Coincident(g71,g41)
    c: Vertical(g71)
    c: Coincident(g72,g34)
    c: Coincident(g72,g56)
    c: Horizontal(g72)
    c: Coincident(g73,g56)
    c: Coincident(g73,g28)
    c: Vertical(g73)
    c: Coincident(g74,g28)
    c: Coincident(g74,g34)
    c: Block(g69)
    c: Coincident(g75,g69)
    c: Vertical(g75)
    c: Distance(g75) = 152
    c: Block(g71)
    c: Vertical(g76)
    c: Distance(g76) = 10
    c: Vertical(g77)
    c: Distance(g77) = 4
    c: Vertical(g78)
    c: Distance(g78) = 4
    c: Vertical(g79)
    c: Distance(g79) = 10
    c: Coincident(g80,g78)
    c: Coincident(g80,g77)
    c: Block(g80)
    c: Coincident(g81,g79)
    c: Coincident(g81,g76)
    c: Block(g81)
    c: Coincident(g82,g76)
    c: Coincident(g82,g71)
    c: Horizontal(g82)
    c: Coincident(g83,g75)
    c: Coincident(g83,g77)
    c: Horizontal(g83)
    c: Distance(g83) = 7
    c: Distance(g82) = 7
    c: Vertical(g84)
    c: Distance(g84) = 4
    c: Vertical(g85)
    c: Distance(g85) = 4
    c: Coincident(g86,g84)
    c: Coincident(g86,g85)
    c: Block(g86)
    c: Coincident(g87,g84)
    c: Horizontal(g87)
    c: Distance(g87) = 4
    c: Coincident(g88,g85)
    c: Horizontal(g88)
    c: Distance(g88) = 4
    c: Coincident(g89,g87)
    c: Coincident(g89,g44)
    c: Vertical(g89)
    c: Coincident(g90,g88)
    c: Coincident(g90,g22)
    c: Vertical(g90)
    c: Coincident(g91,g78)
    c: Coincident(g91,g79)
    c: Horizontal(g91)
FEATURE [Sketcher::SketchObject] Sketch008  label="rightSideTop"
  FullyConstrained = false
  sketch-geometry (108):
    g0: Circle CenterX=302.996 CenterY=111.695 CenterZ=0 NormalX=0 NormalY=0 NormalZ=1 AngleXU=0 Radius=1
    g1: Circle CenterX=306.073 CenterY=114.251 CenterZ=0 NormalX=0 NormalY=0 NormalZ=1 AngleXU=0 Radius=1
    g2: Circle CenterX=306.073 CenterY=110.251 CenterZ=0 NormalX=0 NormalY=0 NormalZ=1 AngleXU=0 Radius=1
    g3: BSplineCurve PolesCount=3 KnotsCount=2 Degree=2 IsPeriodic=0
    g4: GeomPoint X=302.996 Y=111.695 Z=0
    g5: GeomPoint X=306.073 Y=110.251 Z=0
    g6: Circle CenterX=306.073 CenterY=95.2763 CenterZ=0 NormalX=0 NormalY=0 NormalZ=1 AngleXU=0 Radius=1
    g7: Circle CenterX=306.073 CenterY=91.2763 CenterZ=0 NormalX=0 NormalY=0 NormalZ=1 AngleXU=0 Radius=1
    g8: Circle CenterX=302.567 CenterY=89.3511 CenterZ=0 NormalX=0 NormalY=0 NormalZ=1 AngleXU=0 Radius=1
    g9: BSplineCurve PolesCount=3 KnotsCount=2 Degree=2 IsPeriodic=0
    g10: GeomPoint X=306.073 Y=95.2763 Z=0
    g11: GeomPoint X=302.567 Y=89.3511 Z=0
    g12: LineSegment StartX=306.073 StartY=110.251 StartZ=0 EndX=306.073 EndY=95.2763 EndZ=0
    g13: Circle CenterX=302.073 CenterY=124.221 CenterZ=0 NormalX=0 NormalY=0 NormalZ=1 AngleXU=0 Radius=1
    g14: Circle CenterX=306.073 CenterY=124.221 CenterZ=0 NormalX=0 NormalY=0 NormalZ=1 AngleXU=0 Radius=1
    g15: Circle CenterX=302.996 CenterY=121.665 CenterZ=0 NormalX=0 NormalY=0 NormalZ=1 AngleXU=0 Radius=1
    g16: BSplineCurve PolesCount=3 KnotsCount=2 Degree=2 IsPeriodic=0
    g17: GeomPoint X=302.073 Y=124.221 Z=0
    g18: GeomPoint X=302.996 Y=121.665 Z=0
    g19: Circle CenterX=306.073 CenterY=73.3346 CenterZ=0 NormalX=0 NormalY=0 NormalZ=1 AngleXU=0 Radius=1
    g20: Circle CenterX=306.073 CenterY=77.3346 CenterZ=0 NormalX=0 NormalY=0 NormalZ=1 AngleXU=0 Radius=1
    g21: Circle CenterX=302.535 CenterY=75.4095 CenterZ=0 NormalX=0 NormalY=0 NormalZ=1 AngleXU=0 Radius=1
    g22: BSplineCurve PolesCount=3 KnotsCount=2 Degree=2 IsPeriodic=0
    g23: GeomPoint X=306.073 Y=73.3346 Z=0
    g24: GeomPoint X=302.535 Y=75.4095 Z=0
    g25: Circle CenterX=362.073 CenterY=124.221 CenterZ=0 NormalX=0 NormalY=0 NormalZ=1 AngleXU=0 Radius=1
    g26: Circle CenterX=366.073 CenterY=124.221 CenterZ=0 NormalX=0 NormalY=0 NormalZ=1 AngleXU=0 Radius=1
    g27: Circle CenterX=362.567 CenterY=122.294 CenterZ=0 NormalX=0 NormalY=0 NormalZ=1 AngleXU=0 Radius=1
    g28: BSplineCurve PolesCount=3 KnotsCount=2 Degree=2 IsPeriodic=0
    g29: GeomPoint X=362.073 Y=124.221 Z=0
    g30: GeomPoint X=362.567 Y=122.294 Z=0
    g31: Circle CenterX=322.073 CenterY=124.221 CenterZ=0 NormalX=0 NormalY=0 NormalZ=1 AngleXU=0 Radius=1
    g32: Circle CenterX=318.073 CenterY=124.221 CenterZ=0 NormalX=0 NormalY=0 NormalZ=1 AngleXU=0 Radius=1
    g33: Circle CenterX=318.073 CenterY=120.221 CenterZ=0 NormalX=0 NormalY=0 NormalZ=1 AngleXU=0 Radius=1
    g34: BSplineCurve PolesCount=3 KnotsCount=2 Degree=2 IsPeriodic=0
    g35: GeomPoint X=322.073 Y=124.221 Z=0
    g36: GeomPoint X=318.073 Y=120.221 Z=0
    g37: Circle CenterX=322.073 CenterY=105.865 CenterZ=0 NormalX=0 NormalY=0 NormalZ=1 AngleXU=0 Radius=1
    g38: Circle CenterX=318.073 CenterY=105.865 CenterZ=0 NormalX=0 NormalY=0 NormalZ=1 AngleXU=0 Radius=1
    g39: Circle CenterX=318.073 CenterY=109.865 CenterZ=0 NormalX=0 NormalY=0 NormalZ=1 AngleXU=0 Radius=1
    g40: BSplineCurve PolesCount=3 KnotsCount=2 Degree=2 IsPeriodic=0
    g41: GeomPoint X=322.073 Y=105.865 Z=0
    g42: GeomPoint X=318.073 Y=109.865 Z=0
    g43: Circle CenterX=336.157 CenterY=107.779 CenterZ=0 NormalX=0 NormalY=0 NormalZ=1 AngleXU=0 Radius=1
    g44: Circle CenterX=332.651 CenterY=105.853 CenterZ=0 NormalX=0 NormalY=0 NormalZ=1 AngleXU=0 Radius=1
    g45: Circle CenterX=328.643 CenterY=105.865 CenterZ=0 NormalX=0 NormalY=0 NormalZ=1 AngleXU=0 Radius=1
    g46: BSplineCurve PolesCount=3 KnotsCount=2 Degree=2 IsPeriodic=0
    g47: GeomPoint X=336.157 Y=107.779 Z=0
    g48: GeomPoint X=328.643 Y=105.865 Z=0
    g49: Circle CenterX=322.073 CenterY=76.4095 CenterZ=0 NormalX=0 NormalY=0 NormalZ=1 AngleXU=0 Radius=4
    g50: BSplineCurve PolesCount=3 KnotsCount=2 Degree=2 IsPeriodic=0
    g51: GeomPoint X=318.073 Y=72.4095 Z=0
    g52: GeomPoint X=322.073 Y=76.4095 Z=0
    g53: Circle CenterX=375.073 CenterY=72.4095 CenterZ=0 NormalX=0 NormalY=0 NormalZ=1 AngleXU=0 Radius=1
    g54: Circle CenterX=375.073 CenterY=76.4095 CenterZ=0 NormalX=0 NormalY=0 NormalZ=1 AngleXU=0 Radius=1
    g55: Circle CenterX=371.073 CenterY=76.4095 CenterZ=0 NormalX=0 NormalY=0 NormalZ=1 AngleXU=0 Radius=1
    g56: BSplineCurve PolesCount=3 KnotsCount=2 Degree=2 IsPeriodic=0
    g57: GeomPoint X=375.073 Y=72.4095 Z=0
    g58: GeomPoint X=371.073 Y=76.4095 Z=0
    g59: LineSegment StartX=322.073 StartY=76.4095 StartZ=0 EndX=371.073 EndY=76.4095 EndZ=0
    g60: Circle CenterX=232.072 CenterY=133.221 CenterZ=0 NormalX=0 NormalY=0 NormalZ=1 AngleXU=0 Radius=1
    g61: Circle CenterX=226.072 CenterY=136.221 CenterZ=0 NormalX=0 NormalY=0 NormalZ=1 AngleXU=0 Radius=1
    g62: Circle CenterX=226.072 CenterY=124.221 CenterZ=0 NormalX=0 NormalY=0 NormalZ=1 AngleXU=0 Radius=1
    g63: Circle CenterX=232.072 CenterY=127.221 CenterZ=0 NormalX=0 NormalY=0 NormalZ=1 AngleXU=0 Radius=1
    g64: BSplineCurve PolesCount=5 KnotsCount=3 Degree=3 IsPeriodic=0
    g65: GeomPoint X=232.072 Y=133.221 Z=0
    g66: GeomPoint X=223.072 Y=130.221 Z=0
    g67: GeomPoint X=232.072 Y=127.221 Z=0
    g68: LineSegment StartX=240.687 StartY=51.8263 StartZ=0 EndX=243.317 EndY=53.2701 EndZ=0
    g69: LineSegment StartX=243.575 StartY=46.5669 StartZ=0 EndX=246.205 EndY=48.0108 EndZ=0
    g70: ArcOfCircle CenterX=247.391 CenterY=52.0843 CenterZ=0 NormalX=0 NormalY=0 NormalZ=1 AngleXU=0 Radius=4.24264 StartAngle=4.42912 EndAngle=9.14151
    g71: LineSegment StartX=243.475 StartY=65.4951 StartZ=0 EndX=245.073 EndY=63.5726 EndZ=0
    g72: LineSegment StartX=243.575 StartY=46.5669 StartZ=0 EndX=245.072 EndY=43.8408 EndZ=0
    g73: LineSegment StartX=245.072 StartY=43.8408 StartZ=0 EndX=302.535 EndY=75.4095 EndZ=0
    g74: LineSegment StartX=239.192 StartY=54.5542 StartZ=0 EndX=302.567 EndY=89.3511 EndZ=0
    g75: LineSegment StartX=232.072 StartY=127.221 StartZ=0 EndX=232.072 EndY=124.221 EndZ=0
    g76: LineSegment StartX=232.072 StartY=136.221 StartZ=0 EndX=232.072 EndY=133.221 EndZ=0
    g77: LineSegment StartX=232.072 StartY=136.221 StartZ=0 EndX=407.073 EndY=136.221 EndZ=0
    g78: LineSegment StartX=322.073 StartY=124.221 StartZ=0 EndX=362.073 EndY=124.221 EndZ=0
    g79: LineSegment StartX=362.567 StartY=122.294 StartZ=0 EndX=336.157 EndY=107.779 EndZ=0
    g80: LineSegment StartX=322.073 StartY=105.865 StartZ=0 EndX=328.643 EndY=105.865 EndZ=0
    g81: LineSegment StartX=318.073 StartY=120.221 StartZ=0 EndX=318.073 EndY=109.865 EndZ=0
    g82: LineSegment StartX=232.072 StartY=124.221 StartZ=0 EndX=302.073 EndY=124.221 EndZ=0
    g83: LineSegment StartX=302.996 StartY=121.665 StartZ=0 EndX=240.171 EndY=69.471 EndZ=0
    g84: LineSegment StartX=240.171 StartY=69.471 StartZ=0 EndX=241.711 EndY=67.6177 EndZ=0
    g85: LineSegment StartX=241.711 StartY=67.6177 StartZ=0 EndX=246.787 EndY=71.8365 EndZ=0
    g86: LineSegment StartX=246.787 StartY=71.8365 StartZ=0 EndX=248.551 EndY=69.712 EndZ=0
    g87: LineSegment StartX=248.551 StartY=69.712 StartZ=0 EndX=243.475 EndY=65.4951 EndZ=0
    g88: LineSegment StartX=245.073 StartY=63.5726 StartZ=0 EndX=302.996 EndY=111.695 EndZ=0
    g89: LineSegment StartX=239.192 StartY=54.5542 StartZ=0 EndX=240.687 EndY=51.8263 EndZ=0
    g90: LineSegment StartX=375.073 StartY=48.2206 StartZ=0 EndX=382.073 EndY=48.2206 EndZ=0
    g91: LineSegment StartX=407.073 StartY=48.2206 StartZ=0 EndX=400.073 EndY=48.2206 EndZ=0
    g92: LineSegment StartX=394.073 StartY=48.2206 StartZ=0 EndX=394.073 EndY=52.2206 EndZ=0
    g93: LineSegment StartX=388.073 StartY=48.2206 StartZ=0 EndX=388.073 EndY=58.2206 EndZ=0
    g94: ArcOfCircle CenterX=385.073 CenterY=61.2206 CenterZ=0 NormalX=0 NormalY=0 NormalZ=1 AngleXU=0 Radius=4.24264 StartAngle=5.49779 EndAngle=10.2102
    g95: ArcOfCircle CenterX=397.073 CenterY=55.2206 CenterZ=0 NormalX=0 NormalY=0 NormalZ=1 AngleXU=0 Radius=4.24264 StartAngle=5.49779 EndAngle=10.2102
    g96: LineSegment StartX=382.073 StartY=58.2206 StartZ=0 EndX=382.073 EndY=48.2206 EndZ=0
    g97: LineSegment StartX=400.073 StartY=52.2206 StartZ=0 EndX=400.073 EndY=48.2206 EndZ=0
    g98: LineSegment StartX=394.073 StartY=48.2206 StartZ=0 EndX=388.073 EndY=48.2206 EndZ=0
    g99: LineSegment StartX=306.073 StartY=-27.5935 StartZ=0 EndX=310.073 EndY=-27.5935 EndZ=0
    g100: LineSegment StartX=318.073 StartY=-27.5935 StartZ=0 EndX=314.073 EndY=-27.5935 EndZ=0
    g101: LineSegment StartX=310.073 StartY=-27.5935 StartZ=0 EndX=310.073 EndY=-31.5935 EndZ=0
    g102: LineSegment StartX=314.073 StartY=-27.5935 StartZ=0 EndX=314.073 EndY=-31.5935 EndZ=0
    g103: ArcOfCircle CenterX=312.073 CenterY=-33.5935 CenterZ=0 NormalX=0 NormalY=0 NormalZ=1 AngleXU=0 Radius=2.82843 StartAngle=2.35619 EndAngle=7.06858
    g104: LineSegment StartX=375.073 StartY=72.4095 StartZ=0 EndX=375.073 EndY=48.2206 EndZ=0
    g105: LineSegment StartX=407.073 StartY=48.2206 StartZ=0 EndX=407.073 EndY=136.221 EndZ=0
    g106: LineSegment StartX=318.073 StartY=-27.5935 StartZ=0 EndX=318.073 EndY=72.4095 EndZ=0
    g107: LineSegment StartX=306.073 StartY=73.3346 StartZ=0 EndX=306.073 EndY=-27.5935 EndZ=0
  constraints (136):
    c: Weight(g0) = 1
    c: Equal(g0,g1)
    c: Equal(g0,g2)
    c: InternalAlignment(g0,g3)
    c: InternalAlignment(g1,g3)
    c: InternalAlignment(g2,g3)
    c: InternalAlignment(g4,g3)
    c: InternalAlignment(g5,g3)
    c: Weight(g6) = 1
    c: Equal(g6,g7)
    c: Equal(g6,g8)
    c: InternalAlignment(g6,g9)
    c: InternalAlignment(g7,g9)
    c: InternalAlignment(g8,g9)
    c: InternalAlignment(g10,g9)
    c: InternalAlignment(g11,g9)
    c: Block(g3)
    c: Block(g9)
    c: Coincident(g12,g3)
    c: Coincident(g12,g9)
    c: Vertical(g12)
    c: Weight(g13) = 1
    c: Equal(g13,g14)
    c: Equal(g13,g15)
    c: InternalAlignment(g14,g16)
    c: InternalAlignment(g15,g16)
    c: InternalAlignment(g17,g16)
    c: InternalAlignment(g18,g16)
    c: Block(g71)
    c: Block(g72)
    c: Coincident(g73,g72)
    c: Coincident(g73,g22)
    c: Block(g73)
    c: Coincident(g70,g69)
    c: Coincident(g70,g68)
    c: Coincident(g74,g9)
    c: Block(g74)
    c: Distance(g71) = 2.5
    c: Block(g64)
    c: Block(g46)
    c: Block(g59)
    c: Coincident(g75,g64)
    c: Vertical(g75)
    c: Coincident(g76,g64)
    c: Vertical(g76)
    c: Coincident(g77,g76)
    c: Horizontal(g77)
    c: Coincident(g78,g34)
    c: Coincident(g78,g28)
    c: Horizontal(g78)
    c: Coincident(g79,g28)
    c: Coincident(g79,g46)
    c: Coincident(g80,g40)
    c: Coincident(g80,g46)
    c: Horizontal(g80)
    c: Coincident(g81,g34)
    c: Coincident(g81,g40)
    c: Vertical(g81)
    c: Block(g34)
    c: Block(g40)
    c: Block(g28)
    c: Coincident(g82,g75)
    c: Coincident(g82,g16)
    c: Horizontal(g82)
    c: Coincident(g83,g16)
    c: Block(g82)
    c: Block(g83)
    c: Block(g16)
    c: Coincident(g84,g83)
    c: Block(g84)
    c: Coincident(g85,g84)
    c: Block(g85)
    c: Coincident(g86,g85)
    c: Coincident(g87,g86)
    c: Coincident(g87,g71)
    c: Block(g87)
    c: Coincident(g88,g71)
    c: Coincident(g88,g3)
    c: Block(g88)
    c: Coincident(g89,g74)
    c: Coincident(g89,g68)
    c: Block(g70)
    c: Block(g68)
    c: Block(g69)
    c: Block(g22)
    c: Block(g50)
    c: Block(g56)
    c: Horizontal(g90)
    c: Distance(g90) = 7
    c: Horizontal(g91)
    c: Distance(g91) = 7
    c: Vertical(g92)
    c: Distance(g92) = 4
    c: Vertical(g93)
    c: Distance(g93) = 10
    c: Coincident(g94,g93)
    c: Coincident(g95,g92)
    c: Block(g95)
    c: Block(g94)
    c: Coincident(g96,g94)
    c: Coincident(g96,g90)
    c: Vertical(g96)
    c: Coincident(g97,g95)
    c: Coincident(g97,g91)
    c: Vertical(g97)
    c: Coincident(g98,g92)
    c: Coincident(g98,g93)
    c: Horizontal(g98)
    c: Horizontal(g99)
    c: Distance(g99) = 4
    c: Horizontal(g100)
    c: Distance(g100) = 4
    c: Coincident(g101,g99)
    c: Vertical(g101)
    c: Coincident(g102,g100)
    c: Vertical(g102)
    c: Distance(g101) = 4
    c: Distance(g102) = 4
    c: Coincident(g103,g101)
    c: Coincident(g103,g102)
    c: Block(g103)
    c: Coincident(g104,g56)
    c: Coincident(g104,g90)
    c: Vertical(g104)
    c: Block(g104)
    c: Coincident(g105,g91)
    c: Coincident(g105,g77)
    c: Vertical(g105)
    c: Block(g77)
    c: Block(g105)
    c: Coincident(g106,g100)
    c: Coincident(g106,g50)
    c: Vertical(g106)
    c: Coincident(g107,g22)
    c: Coincident(g107,g99)
    c: Vertical(g107)
FEATURE [Sketcher::SketchObject] Sketch009  label="middleBottom"
  FullyConstrained = true
  sketch-geometry (109):
    g0: Circle CenterX=175.022 CenterY=5.37834 CenterZ=0 NormalX=0 NormalY=0 NormalZ=1 AngleXU=0 Radius=1
    g1: Circle CenterX=179.022 CenterY=7.57463 CenterZ=0 NormalX=0 NormalY=0 NormalZ=1 AngleXU=0 Radius=1
    g2: Circle CenterX=179.022 CenterY=5.34704 CenterZ=0 NormalX=0 NormalY=0 NormalZ=1 AngleXU=0 Radius=1
    g3: BSplineCurve PolesCount=3 KnotsCount=2 Degree=2 IsPeriodic=0
    g4: GeomPoint X=175.022 Y=5.37834 Z=0
    g5: GeomPoint X=179.022 Y=5.34704 Z=0
    g6: Circle CenterX=189.124 CenterY=5.37834 CenterZ=0 NormalX=0 NormalY=0 NormalZ=1 AngleXU=0 Radius=1
    g7: Circle CenterX=185.124 CenterY=7.57463 CenterZ=0 NormalX=0 NormalY=0 NormalZ=1 AngleXU=0 Radius=1
    g8: Circle CenterX=185.124 CenterY=5.34704 CenterZ=0 NormalX=0 NormalY=0 NormalZ=1 AngleXU=0 Radius=1
    g9: BSplineCurve PolesCount=3 KnotsCount=2 Degree=2 IsPeriodic=0
    g10: GeomPoint X=189.124 Y=5.37834 Z=0
    g11: GeomPoint X=185.124 Y=5.34704 Z=0
    g12: Circle CenterX=224.513 CenterY=-14.0532 CenterZ=0 NormalX=0 NormalY=0 NormalZ=1 AngleXU=0 Radius=1
    g13: Circle CenterX=236.584 CenterY=-24.2775 CenterZ=0 NormalX=0 NormalY=0 NormalZ=1 AngleXU=0 Radius=1
    g14: BSplineCurve PolesCount=3 KnotsCount=2 Degree=2 IsPeriodic=0
    g15: GeomPoint X=236.584 Y=-24.2775 Z=0
    g16: Circle CenterX=125.607 CenterY=-21.7539 CenterZ=0 NormalX=0 NormalY=0 NormalZ=1 AngleXU=0 Radius=1
    g17: Circle CenterX=139.632 CenterY=-14.0532 CenterZ=0 NormalX=0 NormalY=0 NormalZ=1 AngleXU=0 Radius=1
    g18: Circle CenterX=127.325 CenterY=-24.2775 CenterZ=0 NormalX=0 NormalY=0 NormalZ=1 AngleXU=0 Radius=1
    g19: BSplineCurve PolesCount=3 KnotsCount=2 Degree=2 IsPeriodic=0
    g20: GeomPoint X=125.607 Y=-21.7539 Z=0
    g21: GeomPoint X=127.325 Y=-24.2775 Z=0
    g22: Circle CenterX=179.022 CenterY=-85.8163 CenterZ=0 NormalX=0 NormalY=0 NormalZ=1 AngleXU=0 Radius=1
    g23: Circle CenterX=179.022 CenterY=-91.7794 CenterZ=0 NormalX=0 NormalY=0 NormalZ=1 AngleXU=0 Radius=1
    g24: Circle CenterX=171.895 CenterY=-91.8014 CenterZ=0 NormalX=0 NormalY=0 NormalZ=1 AngleXU=0 Radius=1
    g25: BSplineCurve PolesCount=3 KnotsCount=2 Degree=2 IsPeriodic=0
    g26: GeomPoint X=179.022 Y=-85.8163 Z=0
    g27: GeomPoint X=171.895 Y=-91.8014 Z=0
    g28: Circle CenterX=185.124 CenterY=-86.2028 CenterZ=0 NormalX=0 NormalY=0 NormalZ=1 AngleXU=0 Radius=1
    g29: Circle CenterX=185.124 CenterY=-91.7794 CenterZ=0 NormalX=0 NormalY=0 NormalZ=1 AngleXU=0 Radius=1
    g30: Circle CenterX=191.747 CenterY=-91.7794 CenterZ=0 NormalX=0 NormalY=0 NormalZ=1 AngleXU=0 Radius=1
    g31: BSplineCurve PolesCount=3 KnotsCount=2 Degree=2 IsPeriodic=0
    g32: GeomPoint X=185.124 Y=-86.2028 Z=0
    g33: GeomPoint X=191.747 Y=-91.7794 Z=0
    g34: BSplineCurve PolesCount=5 KnotsCount=3 Degree=3 IsPeriodic=0
    g35: LineSegment StartX=132.072 StartY=-100.779 StartZ=0 EndX=132.072 EndY=-103.779 EndZ=0
    g36: GeomPoint X=232.072 Y=-94.7794 Z=0
    g37: GeomPoint X=223.072 Y=-97.7794 Z=0
    g38: Circle CenterX=232.072 CenterY=-94.7794 CenterZ=0 NormalX=0 NormalY=0 NormalZ=1 AngleXU=0 Radius=1
    g39: Circle CenterX=232.072 CenterY=-100.779 CenterZ=0 NormalX=0 NormalY=0 NormalZ=1 AngleXU=0 Radius=1
    g40: BSplineCurve PolesCount=5 KnotsCount=3 Degree=3 IsPeriodic=0
    g41: GeomPoint X=232.072 Y=-100.779 Z=0
    g42: LineSegment StartX=123.656 StartY=-37.1092 StartZ=0 EndX=122.136 EndY=-35.2714 EndZ=0
    g43: LineSegment StartX=117.05 StartY=-39.4781 StartZ=0 EndX=115.291 EndY=-37.3514 EndZ=0
    g44: LineSegment StartX=120.377 StartY=-33.1447 StartZ=0 EndX=118.86 EndY=-31.3104 EndZ=0
    g45: ArcOfCircle CenterX=116.562 CenterY=-19.6236 CenterZ=0 NormalX=0 NormalY=0 NormalZ=1 AngleXU=0 Radius=4.24264 StartAngle=1.28753 EndAngle=5.99992
    g46: LineSegment StartX=240.266 StartY=-37.1092 StartZ=0 EndX=189.124 EndY=5.37834 EndZ=0
    g47: LineSegment StartX=191.747 StartY=-91.7794 StartZ=0 EndX=232.072 EndY=-91.7794 EndZ=0
    g48: LineSegment StartX=232.072 StartY=-91.7794 StartZ=0 EndX=232.072 EndY=-94.7794 EndZ=0
    g49: LineSegment StartX=232.072 StartY=-100.779 StartZ=0 EndX=232.072 EndY=-103.779 EndZ=0
    g50: LineSegment StartX=132.072 StartY=-103.779 StartZ=0 EndX=232.072 EndY=-103.779 EndZ=0
    g51: LineSegment StartX=132.072 StartY=-91.8014 StartZ=0 EndX=132.072 EndY=-94.7791 EndZ=0
    g52: LineSegment StartX=132.072 StartY=-91.8014 StartZ=0 EndX=171.895 EndY=-91.8014 EndZ=0
    g53: LineSegment StartX=179.022 StartY=-85.8163 StartZ=0 EndX=179.022 EndY=5.34704 EndZ=0
    g54: LineSegment StartX=175.022 StartY=5.37834 StartZ=0 EndX=123.656 EndY=-37.1092 EndZ=0
    g55: LineSegment StartX=185.124 StartY=5.34704 StartZ=0 EndX=185.124 EndY=-86.2028 EndZ=0
    g56: LineSegment StartX=122.136 StartY=-35.2714 StartZ=0 EndX=117.05 EndY=-39.4781 EndZ=0
    g57: LineSegment StartX=115.291 StartY=-37.3514 StartZ=0 EndX=120.377 EndY=-33.1447 EndZ=0
    g58: LineSegment StartX=118.86 StartY=-31.3104 StartZ=0 EndX=127.325 EndY=-24.2775 EndZ=0
    g59: LineSegment StartX=125.607 StartY=-21.7539 StartZ=0 EndX=124.815 EndY=-22.1887 EndZ=0
    g60: LineSegment StartX=123.265 StartY=-19.3655 StartZ=0 EndX=124.815 EndY=-22.1887 EndZ=0
    g61: LineSegment StartX=120.636 StartY=-20.8094 StartZ=0 EndX=123.265 EndY=-19.3655 EndZ=0
    g62: LineSegment StartX=117.748 StartY=-15.55 StartZ=0 EndX=120.377 EndY=-14.1062 EndZ=0
    g63: LineSegment StartX=120.377 StartY=-14.1062 StartZ=0 EndX=118.934 EndY=-11.4765 EndZ=0
    g64: LineSegment StartX=236.584 StartY=-24.2775 StartZ=0 EndX=245.072 EndY=-31.3037 EndZ=0
    g65: LineSegment StartX=245.072 StartY=-31.3037 StartZ=0 EndX=243.535 EndY=-33.1602 EndZ=0
    g66: LineSegment StartX=243.535 StartY=-33.1602 StartZ=0 EndX=248.619 EndY=-37.3688 EndZ=0
    g67: LineSegment StartX=248.619 StartY=-37.3688 StartZ=0 EndX=246.855 EndY=-39.5064 EndZ=0
    g68: LineSegment StartX=246.855 StartY=-39.5064 StartZ=0 EndX=241.778 EndY=-35.2889 EndZ=0
    g69: LineSegment StartX=241.778 StartY=-35.2889 StartZ=0 EndX=240.266 EndY=-37.1092 EndZ=0
    g70: LineSegment StartX=243.628 StartY=-14.0323 StartZ=0 EndX=246.258 EndY=-15.476 EndZ=0
    g71: LineSegment StartX=240.741 StartY=-19.2917 StartZ=0 EndX=243.37 EndY=-20.7355 EndZ=0
    g72: ArcOfCircle CenterX=247.444 CenterY=-19.5496 CenterZ=0 NormalX=0 NormalY=0 NormalZ=1 AngleXU=0 Radius=4.24264 StartAngle=3.4249 EndAngle=8.13729
    g73: LineSegment StartX=240.741 StartY=-19.2917 StartZ=0 EndX=239.201 EndY=-22.0968 EndZ=0
    g74: LineSegment StartX=238.538 StartY=-21.7516 StartZ=0 EndX=239.201 EndY=-22.0968 EndZ=0
    g75: LineSegment StartX=245.072 StartY=-11.4025 StartZ=0 EndX=243.628 EndY=-14.0323 EndZ=0
    g76-g91: Circle x16 (B-spline internal-alignment scaffolding for g92; pole/knot coordinates omitted)
    g92: BSplineCurve PolesCount=16 KnotsCount=14 Degree=3 IsPeriodic=0
    g93-g106: GeomPoint x14 (B-spline internal-alignment scaffolding for g92; pole/knot coordinates omitted)
    g107: LineSegment StartX=165.871 StartY=14.2956 StartZ=0 EndX=118.934 EndY=-11.4765 EndZ=0
    g108: LineSegment StartX=198.264 StartY=14.2963 StartZ=0 EndX=245.072 EndY=-11.4025 EndZ=0
  constraints (146):
    c: Weight(g0) = 1
    c: Equal(g0,g1)
    c: Equal(g0,g2)
    c: InternalAlignment(g0,g3)
    c: InternalAlignment(g1,g3)
    c: InternalAlignment(g2,g3)
    c: InternalAlignment(g4,g3)
    c: InternalAlignment(g5,g3)
    c: Weight(g6) = 1
    c: Equal(g6,g7)
    c: Equal(g6,g8)
    c: InternalAlignment(g6,g9)
    c: InternalAlignment(g7,g9)
    c: InternalAlignment(g8,g9)
    c: InternalAlignment(g10,g9)
    c: InternalAlignment(g11,g9)
    c: Block(g9)
    c: Block(g3)
    c: InternalAlignment(g12,g14)
    c: InternalAlignment(g13,g14)
    c: InternalAlignment(g15,g14)
    c: Block(g14)
    c: Weight(g16) = 1
    c: Equal(g16,g17)
    c: Equal(g16,g18)
    c: InternalAlignment(g16,g19)
    c: InternalAlignment(g17,g19)
    c: InternalAlignment(g18,g19)
    c: InternalAlignment(g20,g19)
    c: InternalAlignment(g21,g19)
    c: Block(g19)
    c: Weight(g22) = 1
    c: Equal(g22,g23)
    c: Equal(g22,g24)
    c: InternalAlignment(g22,g25)
    c: InternalAlignment(g23,g25)
    c: InternalAlignment(g24,g25)
    c: InternalAlignment(g26,g25)
    c: InternalAlignment(g27,g25)
    c: Weight(g28) = 1
    c: Equal(g28,g29)
    c: Equal(g28,g30)
    c: InternalAlignment(g28,g31)
    c: InternalAlignment(g29,g31)
    c: InternalAlignment(g30,g31)
    c: InternalAlignment(g32,g31)
    c: InternalAlignment(g33,g31)
    c: Block(g31)
    c: Block(g25)
    c: Block(g34)
    c: Coincident(g35,g34)
    c: Vertical(g35)
    c: Block(g35)
    c: Equal(g38,g39)
    c: InternalAlignment(g38,g40)
    c: InternalAlignment(g39,g40)
    c: InternalAlignment(g36,g40)
    c: InternalAlignment(g37,g40)
    c: InternalAlignment(g41,g40)
    c: Block(g40)
    c: Distance(g42) = 2.385
    c: Distance(g43) = 2.76
    c: Parallel(g42,g44)
    c: Block(g45)
    c: Coincident(g46,g9)
    c: Coincident(g47,g31)
    c: Horizontal(g47)
    c: Block(g47)
    c: Coincident(g48,g47)
    c: Coincident(g48,g40)
    c: Vertical(g48)
    c: Block(g48)
    c: Coincident(g49,g40)
    c: Vertical(g49)
    c: Block(g49)
    c: Coincident(g50,g35)
    c: Coincident(g50,g49)
    c: Horizontal(g50)
    c: Block(g50)
    c: Coincident(g51,g34)
    c: Vertical(g51)
    c: Coincident(g52,g51)
    c: Coincident(g52,g25)
    c: Horizontal(g52)
    c: Coincident(g53,g25)
    c: Coincident(g53,g3)
    c: Vertical(g53)
    c: Coincident(g54,g3)
    c: Coincident(g54,g42)
    c: Coincident(g55,g9)
    c: Coincident(g55,g31)
    c: Vertical(g55)
    c: Block(g42)
    c: Coincident(g56,g42)
    c: Coincident(g56,g43)
    c: Coincident(g57,g43)
    c: Coincident(g57,g44)
    c: Block(g57)
    c: Block(g56)
    c: Coincident(g58,g44)
    c: Coincident(g58,g19)
    c: Block(g58)
    c: Coincident(g59,g19)
    c: Block(g59)
    c: Coincident(g60,g59)
    c: Block(g60)
    c: Coincident(g61,g45)
    c: Coincident(g61,g60)
    c: Coincident(g62,g45)
    c: Coincident(g63,g62)
    c: Block(g63)
    c: Coincident(g64,g14)
    c: Block(g64)
    c: Coincident(g65,g64)
    c: Coincident(g66,g65)
    c: Coincident(g67,g66)
    c: Coincident(g68,g67)
    c: Coincident(g69,g68)
    c: Coincident(g69,g46)
    c: Block(g46)
    c: Block(g68)
    c: Block(g66)
    c: Distance(g70) = 3
    c: Distance(g71) = 3
    c: Coincident(g72,g70)
    c: Coincident(g72,g71)
    c: Block(g72)
    c: Coincident(g73,g71)
    c: Distance(g73) = 3.2
    c: Coincident(g74,g14)
    c: Coincident(g74,g73)
    c: Coincident(g75,g70)
    c: Block(g75)
    c: Block(g73)
    c: Distance(g63) = 3
    c: Distance(g60) = 3.22077
    c: Weight(g76) = 1
    c: Equal(g76, g77-g91) x15
    c: InternalAlignment(g76-g91 -> g92) x16
    c: InternalAlignment(g93-g106 -> g92) x14
    c: Coincident(g107,g92)
    c: Coincident(g107,g63)
    c: Block(g107)
    c: Block(g92)
    c: Coincident(g108,g92)
    c: Coincident(g108,g75)
FEATURE [Sketcher::SketchObject] Sketch010  label="legBottom"
  FullyConstrained = true
  MapMode = 4
  Placement = pos=(0,0,0) rot=(0.57735,0.57735,0.57735;2.0944rad)
  sketch-geometry (38):
    g0: BSplineCurve PolesCount=3 KnotsCount=2 Degree=2 IsPeriodic=0
    g1: Circle CenterX=-199.665 CenterY=-138.314 CenterZ=0 NormalX=0 NormalY=0 NormalZ=1 AngleXU=0 Radius=1
    g2: GeomPoint X=-199.665 Y=-138.314 Z=0
    g3: LineSegment StartX=-199.665 StartY=-138.314 StartZ=0 EndX=-200.721 EndY=-141.122 EndZ=0
    g4: Circle CenterX=-17.0256 CenterY=-190.268 CenterZ=0 NormalX=0 NormalY=0 NormalZ=1 AngleXU=0 Radius=10.5072
    g5: Circle CenterX=-37.7758 CenterY=-187.672 CenterZ=0 NormalX=0 NormalY=0 NormalZ=1 AngleXU=0 Radius=5.64388
    g6: Circle CenterX=-51.4606 CenterY=-185.091 CenterZ=0 NormalX=0 NormalY=0 NormalZ=1 AngleXU=0 Radius=3.01653
    g7: Circle CenterX=-60.4835 CenterY=-182.688 CenterZ=0 NormalX=0 NormalY=0 NormalZ=1 AngleXU=0 Radius=2.12826
    g8: Circle CenterX=-3.29005 CenterY=-177.662 CenterZ=0 NormalX=0 NormalY=0 NormalZ=1 AngleXU=0 Radius=3.26661
    g9: ArcOfCircle CenterX=11.0205 CenterY=-198.019 CenterZ=0 NormalX=0 NormalY=0 NormalZ=1 AngleXU=0 Radius=13 StartAngle=2.78068 EndAngle=5.92131
    g10: LineSegment StartX=5.08312 StartY=-176.581 StartZ=0 EndX=-1.14188 EndY=-193.429 EndZ=0
    g11: ArcOfCircle CenterX=17.2475 CenterY=-181.166 CenterZ=0 NormalX=0 NormalY=0 NormalZ=1 AngleXU=0 Radius=13 StartAngle=1.21042 EndAngle=2.78109
    g12: LineSegment StartX=38.8952 StartY=-231.233 StartZ=0 EndX=-200.721 EndY=-141.122 EndZ=0
    g13: LineSegment StartX=38.8952 StartY=-231.233 StartZ=0 EndX=39.9512 EndY=-228.425 EndZ=0
    g14: ArcOfCircle CenterX=46.9911 CenterY=-209.705 CenterZ=0 NormalX=0 NormalY=0 NormalZ=1 AngleXU=0 Radius=20 StartAngle=2.78766 EndAngle=4.35269
    g15: LineSegment StartX=23.7323 StartY=-126.969 StartZ=0 EndX=17.4091 EndY=-143.817 EndZ=0
    g16: ArcOfCircle CenterX=29.5716 CenterY=-148.408 CenterZ=0 NormalX=0 NormalY=0 NormalZ=1 AngleXU=0 Radius=13 StartAngle=2.78068 EndAngle=4.35262
    g17: ArcOfCircle CenterX=35.8967 CenterY=-131.555 CenterZ=0 NormalX=0 NormalY=0 NormalZ=1 AngleXU=0 Radius=13 StartAngle=1.21584 EndAngle=2.78109
    g18: ArcOfCircle CenterX=48.1805 CenterY=-98.7782 CenterZ=0 NormalX=0 NormalY=0 NormalZ=1 AngleXU=0 Radius=13 StartAngle=2.78068 EndAngle=4.35005
    g19: LineSegment StartX=42.354 StartY=-77.3391 StartZ=0 EndX=36.018 EndY=-94.1875 EndZ=0
    g20: ArcOfCircle CenterX=54.5183 CenterY=-81.9247 CenterZ=0 NormalX=0 NormalY=0 NormalZ=1 AngleXU=0 Radius=13 StartAngle=2.42113 EndAngle=2.78109
    g21: ArcOfCircle CenterX=20.184 CenterY=-217.506 CenterZ=0 NormalX=0 NormalY=0 NormalZ=1 AngleXU=0 Radius=3.81084 StartAngle=1.88136 EndAngle=6.80465
    g22: LineSegment StartX=38.4753 StartY=-115.966 StartZ=0 EndX=41.2852 EndY=-117.017 EndZ=0
    g23: ArcOfCircle CenterX=36.3663 CenterY=-113.042 CenterZ=0 NormalX=0 NormalY=0 NormalZ=1 AngleXU=0 Radius=3.60555 StartAngle=0.230024 EndAngle=5.3372
    g24: LineSegment StartX=39.8769 StartY=-112.22 StartZ=0 EndX=42.6867 EndY=-113.271 EndZ=0
    g25: LineSegment StartX=19.9036 StartY=-165.61 StartZ=0 EndX=22.7134 EndY=-166.661 EndZ=0
    g26: ArcOfCircle CenterX=17.7945 CenterY=-162.686 CenterZ=0 NormalX=0 NormalY=0 NormalZ=1 AngleXU=0 Radius=3.60555 StartAngle=0.230024 EndAngle=5.3372
    g27: LineSegment StartX=21.3051 StartY=-161.864 StartZ=0 EndX=24.1149 EndY=-162.915 EndZ=0
    g28: LineSegment StartX=41.085 StartY=-66.3176 StartZ=0 EndX=46.0385 EndY=-62.5254 EndZ=0
    g29: LineSegment StartX=48.9563 StartY=-66.3367 StartZ=0 EndX=44.7488 EndY=-73.3482 EndZ=0
    g30: ArcOfCircle CenterX=49.8795 CenterY=-62.6074 CenterZ=0 NormalX=0 NormalY=0 NormalZ=1 AngleXU=0 Radius=3.84187 StartAngle=4.46973 EndAngle=9.40343
    g31: LineSegment StartX=41.085 StartY=-66.3176 StartZ=0 EndX=8.65492 EndY=-152.553 EndZ=0
    g32: LineSegment StartX=43.5724 StartY=-110.934 StartZ=0 EndX=42.6867 EndY=-113.271 EndZ=0
    g33: LineSegment StartX=40.4148 StartY=-119.365 StartZ=0 EndX=41.2852 EndY=-117.017 EndZ=0
    g34: LineSegment StartX=21.8316 StartY=-169.001 StartZ=0 EndX=22.7134 EndY=-166.661 EndZ=0
    g35: LineSegment StartX=24.9948 StartY=-160.575 StartZ=0 EndX=24.1149 EndY=-162.915 EndZ=0
    g36: LineSegment StartX=23.1786 StartY=-202.622 StartZ=0 EndX=19.0195 EndY=-213.878 EndZ=0
    g37: LineSegment StartX=28.2308 StartY=-202.773 StartZ=0 EndX=23.4884 EndY=-215.608 EndZ=0
  constraints (65):
    c: Block(g9)
    c: Block(g11)
    c: InternalAlignment(g1,g0)
    c: InternalAlignment(g2,g0)
    c: Block(g0)
    c: Block(g4)
    c: Block(g8)
    c: Block(g5)
    c: Block(g6)
    c: Block(g7)
    c: Block(g14)
    c: Coincident(g13,g12)
    c: Coincident(g13,g14)
    c: Block(g13)
    c: Coincident(g3,g0)
    c: Coincident(g3,g12)
    c: Block(g12)
    c: Coincident(g10,g11)
    c: Coincident(g10,g9)
    c: Block(g16)
    c: Block(g17)
    c: Coincident(g15,g17)
    c: Coincident(g15,g16)
    c: Block(g18)
    c: Block(g20)
    c: Coincident(g19,g20)
    c: Coincident(g19,g18)
    c: Block(g21)
    c: Block(g23)
    c: Coincident(g24,g23)
    c: Coincident(g22,g23)
    c: Parallel(g24,g22)
    c: Block(g22)
    c: Block(g24)
    c: Block(g26)
    c: Coincident(g27,g26)
    c: Coincident(g25,g26)
    c: Parallel(g27,g25)
    c: Block(g25)
    c: Block(g27)
    c: Block(g28)
    c: Coincident(g30,g28)
    c: Coincident(g30,g29)
    c: Block(g30)
    c: Coincident(g31,g28)
    c: Coincident(g31,g0)
    c: Block(g29)
    c: Coincident(g32,g24)
    c: Block(g32)
    c: Coincident(g33,g22)
    c: Block(g33)
    c: Coincident(g34,g25)
    c: Coincident(g35,g27)
    c: Block(g35)
    c: Block(g34)
    c: Coincident(g36,g9)
    c: Coincident(g36,g21)
    c: Block(g36)
    c: Coincident(g11,g34)
    c: Coincident(g16,g35)
    c: Coincident(g17,g33)
    c: Coincident(g18,g32)
    c: Coincident(g20,g29)
    c: Coincident(g37,g14)
    c: Coincident(g37,g21)
